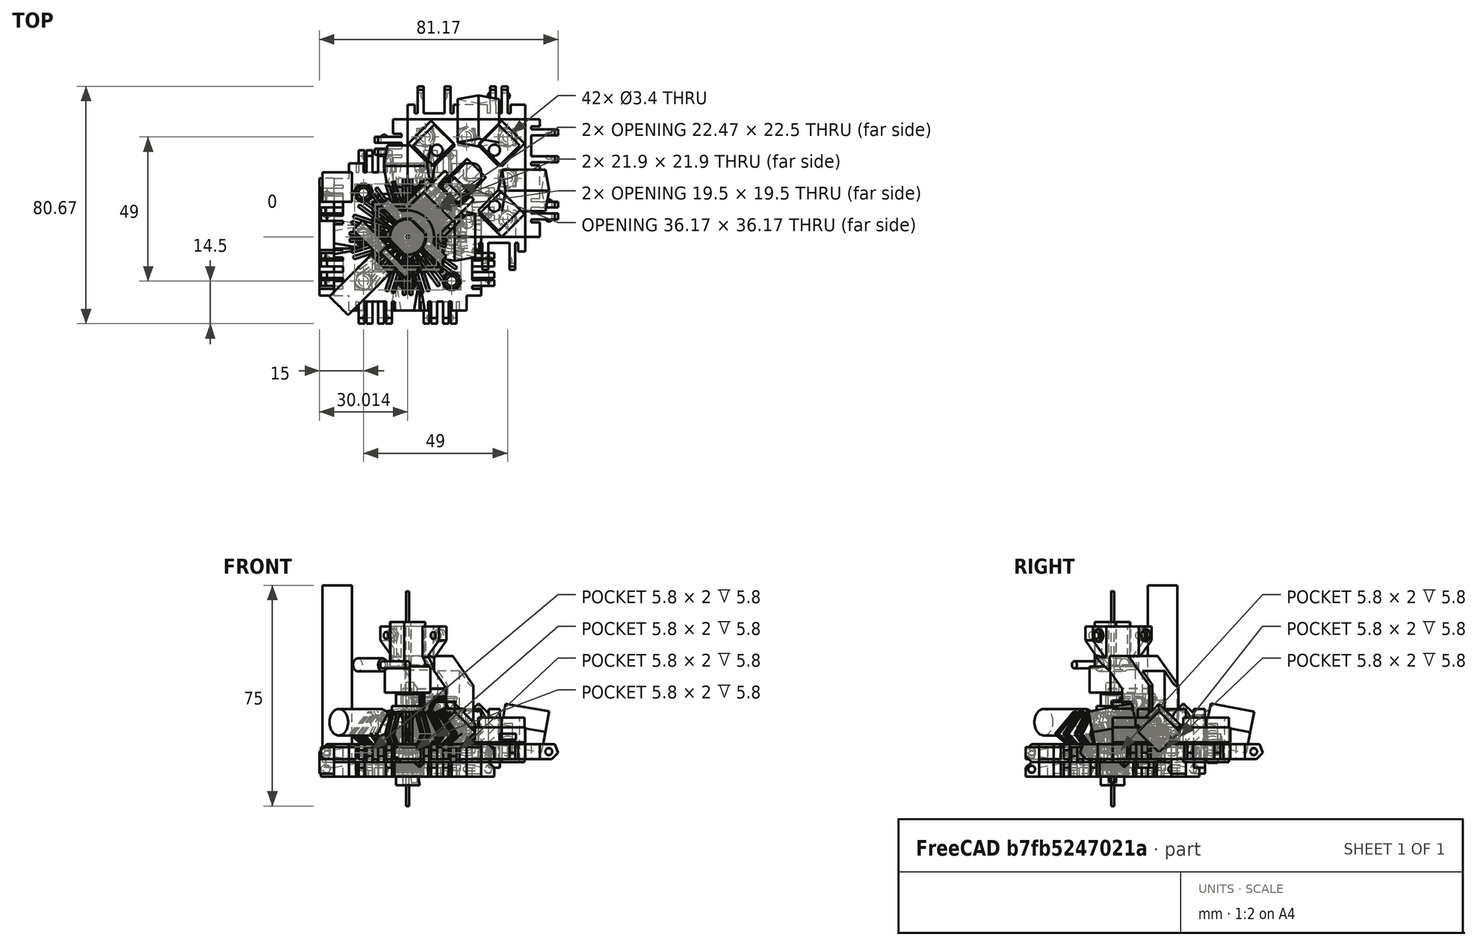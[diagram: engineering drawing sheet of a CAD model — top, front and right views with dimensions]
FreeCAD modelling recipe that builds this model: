
FCSTD DOCUMENT  (FreeCAD 0.18.4R)
Label: Robot-0.6
License: All rights reserved
LicenseURL: http://en.wikipedia.org/wiki/All_rights_reserved
objects: Part::Box×364, Part::Cut×152, Part::Sphere×107, Part::MultiFuse×104, Part::Cylinder×93, Part::Fuse×47, Part::Feature×40, Part::Chamfer×31, Drawing::FeatureViewAnnotation×17, App::DocumentObjectGroup×6, Part::Cone×6, Part::MultiCommon×6, Part::Fillet×5, Part::FeaturePython×4, Part::Mirroring×2, Drawing::FeaturePage×2
note: 961 computed .brp shape members not serialized (recipe doc carries the construction recipe); baked Part::Feature solids carry a one-line shape summary decoded from their .brp

FEATURE [Part::Box] Box  label="Cube"
  AttacherType = Attacher::AttachEngine3D
  Height = 5
  Length = 40
  Placement = pos=(-20,-20,-2) rot=(0,0,1;0rad)
  Width = 40
FEATURE [Part::Sphere] Sphere003  label="Mag Hole 3"
  Angle1 = -90
  Angle2 = 90
  Angle3 = 360
  AttacherType = Attacher::AttachEngine3D
  Placement = pos=(-15,15,1.7) rot=(0,0,1;0rad)
  Radius = 2.83
FEATURE [Part::Sphere] Sphere005  label="Mag Hole 2"
  Angle1 = -90
  Angle2 = 90
  Angle3 = 360
  AttacherType = Attacher::AttachEngine3D
  Placement = pos=(15,0,1.7) rot=(0,0,1;0rad)
  Radius = 2.825
FEATURE [Part::Sphere] Sphere  label="Mag Hole"
  Angle1 = -90
  Angle2 = 90
  Angle3 = 360
  AttacherType = Attacher::AttachEngine3D
  Placement = pos=(-15,-15,1.7) rot=(0,0,1;0rad)
  Radius = 2.83
FEATURE [Part::MultiFuse] Fusion004  label="Ball Holes"
  Shapes = -> [Sphere,Sphere005,Sphere003]
FEATURE [Part::Cut] Cut003
  Base = -> Box
  Tool = -> Fusion004
FEATURE [Part::Box] Box001  label="Cube001"
  AttacherType = Attacher::AttachEngine3D
  Height = 7
  Length = 5
  Placement = pos=(-5,0,-2) rot=(0,0,1;0rad)
  Width = 40
FEATURE [Part::Box] Box002  label="Cube002"
  AttacherType = Attacher::AttachEngine3D
  Height = 7
  Length = 10
  Placement = pos=(-15,6,-2) rot=(0,0,1;0rad)
  Width = 2
FEATURE [Part::Box] Box003  label="Cube003"
  AttacherType = Attacher::AttachEngine3D
  Height = 7
  Length = 10
  Placement = pos=(-15,10,-2) rot=(0,0,1;0rad)
  Width = 2
FEATURE [Part::Box] Box004  label="Cube004"
  AttacherType = Attacher::AttachEngine3D
  Height = 7
  Length = 10
  Placement = pos=(-15,25.4,-2) rot=(0,0,1;0rad)
  Width = 2
FEATURE [Part::Box] Box005  label="Cube005"
  AttacherType = Attacher::AttachEngine3D
  Height = 7
  Length = 10
  Placement = pos=(-15,34.6,-2) rot=(0,0,1;0rad)
  Width = 2
FEATURE [Part::Sphere] Sphere008
  Angle1 = -90
  Angle2 = 90
  Angle3 = 360
  AttacherType = Attacher::AttachEngine3D
  Placement = pos=(-7.5,6.5,0.5) rot=(0,0,1;0rad)
  Radius = 1.25
FEATURE [Part::Box] Box006  label="Chamfer Cube"
  AttacherType = Attacher::AttachEngine3D
  Height = 10
  Length = 13
  Placement = pos=(-11.69,0,-1.19) rot=(0,-1,0;0.785398rad)
  Width = 40
FEATURE [Part::Sphere] Sphere009
  Angle1 = -90
  Angle2 = 90
  Angle3 = 360
  AttacherType = Attacher::AttachEngine3D
  Placement = pos=(-7.5,11.5,0.5) rot=(0,0,1;0rad)
  Radius = 1.25
FEATURE [Part::Sphere] Sphere010
  Angle1 = -90
  Angle2 = 90
  Angle3 = 360
  AttacherType = Attacher::AttachEngine3D
  Placement = pos=(-7.5,28,0.5) rot=(0,0,1;0rad)
  Radius = 1.5
FEATURE [Part::Sphere] Sphere011
  Angle1 = -90
  Angle2 = 90
  Angle3 = 360
  AttacherType = Attacher::AttachEngine3D
  Placement = pos=(-7.5,34,0.5) rot=(0,0,1;0rad)
  Radius = 1.5
FEATURE [Part::Box] Box007  label="Cube007"
  AttacherType = Attacher::AttachEngine3D
  Height = 7
  Length = 4
  Placement = pos=(-6,5,-2) rot=(0,0,1;0rad)
  Width = 1
FEATURE [Part::Box] Box008  label="Cube008"
  AttacherType = Attacher::AttachEngine3D
  Height = 7
  Length = 4
  Placement = pos=(-6,8,-2) rot=(0,0,1;0rad)
  Width = 2
FEATURE [Part::Box] Box009  label="Cube009"
  AttacherType = Attacher::AttachEngine3D
  Height = 7
  Length = 4
  Placement = pos=(-6,12,-2) rot=(0,0,1;0rad)
  Width = 1
FEATURE [Part::Box] Box010  label="Cube010"
  AttacherType = Attacher::AttachEngine3D
  Height = 7
  Length = 4
  Placement = pos=(-6,24.4,-2) rot=(0,0,1;0rad)
  Width = 1
FEATURE [Part::Box] Box011  label="Cube011"
  AttacherType = Attacher::AttachEngine3D
  Height = 7
  Length = 4
  Placement = pos=(-6,36.6,-2) rot=(0,0,1;0rad)
  Width = 1
FEATURE [Part::Box] Box012  label="Cube012"
  AttacherType = Attacher::AttachEngine3D
  Height = 7
  Length = 4
  Placement = pos=(-6,27.4,-2) rot=(0,0,1;0rad)
  Width = 7.2
FEATURE [Part::MultiFuse] Fusion003  label="Extra Holes for Clips"
  Shapes = -> [Box012,Box009,Box011,Box008,Box010,Box007]
FEATURE [Part::Box] Box013  label="Re-level Edge Clip Block"
  AttacherType = Attacher::AttachEngine3D
  Height = 10
  Length = 20
  Placement = pos=(-19,-2,3) rot=(0,0,1;0rad)
  Width = 44
FEATURE [Part::Box] Box014  label="Cube014"
  AttacherType = Attacher::AttachEngine3D
  Height = 7
  Length = 10
  Placement = pos=(-10,34.6,0) rot=(0,0,1;0rad)
  Width = 2
FEATURE [Part::Box] Box015  label="Cube015"
  AttacherType = Attacher::AttachEngine3D
  Height = 7
  Length = 5
  Width = 40
FEATURE [Part::Box] Box016  label="Cube016"
  AttacherType = Attacher::AttachEngine3D
  Height = 7
  Length = 10
  Placement = pos=(-10,25.4,0) rot=(0,0,1;0rad)
  Width = 2
FEATURE [Part::Box] Box017  label="Cube017"
  AttacherType = Attacher::AttachEngine3D
  Height = 7
  Length = 10
  Placement = pos=(-10,10,0) rot=(0,0,1;0rad)
  Width = 2
FEATURE [Part::Box] Box018  label="Cube018"
  AttacherType = Attacher::AttachEngine3D
  Height = 7
  Length = 10
  Placement = pos=(-10,6,0) rot=(0,0,1;0rad)
  Width = 2
FEATURE [Part::Sphere] Sphere012
  Angle1 = -90
  Angle2 = 90
  Angle3 = 360
  AttacherType = Attacher::AttachEngine3D
  Placement = pos=(-3,6.5,2.5) rot=(0,0,1;0rad)
  Radius = 1.25
FEATURE [Part::Box] Box019  label="Cube019"
  AttacherType = Attacher::AttachEngine3D
  Height = 10
  Length = 13
  Placement = pos=(-10.19,0,-1.19) rot=(0,-1,0;0.785398rad)
  Width = 40
FEATURE [Part::Sphere] Sphere013
  Angle1 = -90
  Angle2 = 90
  Angle3 = 360
  AttacherType = Attacher::AttachEngine3D
  Placement = pos=(-3,11.5,2.5) rot=(0,0,1;0rad)
  Radius = 1.25
FEATURE [Part::Sphere] Sphere014
  Angle1 = -90
  Angle2 = 90
  Angle3 = 360
  AttacherType = Attacher::AttachEngine3D
  Placement = pos=(-3,28,2.5) rot=(0,0,1;0rad)
  Radius = 1.5
FEATURE [Part::Sphere] Sphere015
  Angle1 = -90
  Angle2 = 90
  Angle3 = 360
  AttacherType = Attacher::AttachEngine3D
  Placement = pos=(-3,34,2.5) rot=(0,0,1;0rad)
  Radius = 1.5
FEATURE [Part::MultiFuse] Fusion005
  Shapes = -> [Box015,Box018,Box017,Box016,Box014]
FEATURE [Part::Cut] Cut005
  Base = -> Fusion005
  Tool = -> Box019
FEATURE [Part::MultiFuse] Fusion006
  Shapes = -> [Sphere012,Sphere013,Cut005]
FEATURE [Part::MultiFuse] Fusion007
  Shapes = -> [Sphere015,Sphere014]
FEATURE [Part::Cut] Cut006
  Base = -> Fusion006
  Tool = -> Fusion007
FEATURE [Part::Chamfer] Chamfer002
  Base = -> Cut006
  Edges = 4 edges r=4: [Edge31,Edge37,Edge43,Edge46]
FEATURE [Part::Box] Box020  label="Cube020"
  AttacherType = Attacher::AttachEngine3D
  Height = 7
  Length = 4
  Placement = pos=(-1,5,0) rot=(0,0,1;0rad)
  Width = 1
FEATURE [Part::Box] Box021  label="Cube021"
  AttacherType = Attacher::AttachEngine3D
  Height = 7
  Length = 4
  Placement = pos=(-1,8,0) rot=(0,0,1;0rad)
  Width = 2
FEATURE [Part::Box] Box022  label="Cube022"
  AttacherType = Attacher::AttachEngine3D
  Height = 7
  Length = 4
  Placement = pos=(-1,12,0) rot=(0,0,1;0rad)
  Width = 1
FEATURE [Part::Box] Box023  label="Cube023"
  AttacherType = Attacher::AttachEngine3D
  Height = 7
  Length = 4
  Placement = pos=(-1,24.4,0) rot=(0,0,1;0rad)
  Width = 1
FEATURE [Part::Box] Box024  label="Cube024"
  AttacherType = Attacher::AttachEngine3D
  Height = 7
  Length = 4
  Placement = pos=(-1,36.6,0) rot=(0,0,1;0rad)
  Width = 1
FEATURE [Part::Box] Box025  label="Cube025"
  AttacherType = Attacher::AttachEngine3D
  Height = 7
  Length = 4
  Placement = pos=(-1,27.4,0) rot=(0,0,1;0rad)
  Width = 7.2
FEATURE [Part::MultiFuse] Fusion008
  Shapes = -> [Box025,Box022,Box024,Box021,Box023,Box020]
FEATURE [Part::Cut] Cut007
  Base = -> Chamfer002
  Placement = pos=(-5,40,3) rot=(1,0,0;3.14159rad)
  Tool = -> Fusion008
FEATURE [Part::Box] Box026  label="Cube026"
  AttacherType = Attacher::AttachEngine3D
  Height = 10
  Length = 12
  Placement = pos=(-11,-2,-12) rot=(0,0,1;0rad)
  Width = 44
FEATURE [Part::Cut] Cut008
  Base = -> Cut007
  Placement = pos=(40,0,0) rot=(0,0,1;1.5708rad)
  Tool = -> Box026
FEATURE [Part::Box] Box027  label="Cube027"
  AttacherType = Attacher::AttachEngine3D
  Height = 7
  Length = 4
  Placement = pos=(-1,12,0) rot=(0,0,1;0rad)
  Width = 1
FEATURE [Part::Box] Box028  label="Cube028"
  AttacherType = Attacher::AttachEngine3D
  Height = 10
  Length = 13
  Placement = pos=(-10.19,0,-1.19) rot=(0,-1,0;0.785398rad)
  Width = 40
FEATURE [Part::Box] Box029  label="Cube029"
  AttacherType = Attacher::AttachEngine3D
  Height = 7
  Length = 4
  Placement = pos=(-1,27.4,0) rot=(0,0,1;0rad)
  Width = 7.2
FEATURE [Part::Box] Box030  label="Cube030"
  AttacherType = Attacher::AttachEngine3D
  Height = 7
  Length = 4
  Placement = pos=(-1,5,0) rot=(0,0,1;0rad)
  Width = 1
FEATURE [Part::Box] Box031  label="Cube031"
  AttacherType = Attacher::AttachEngine3D
  Height = 7
  Length = 10
  Placement = pos=(-10,6,0) rot=(0,0,1;0rad)
  Width = 2
FEATURE [Part::Box] Box032  label="Cube032"
  AttacherType = Attacher::AttachEngine3D
  Height = 10
  Length = 12
  Placement = pos=(-11,-2,-12) rot=(0,0,1;0rad)
  Width = 44
FEATURE [Part::Sphere] Sphere016
  Angle1 = -90
  Angle2 = 90
  Angle3 = 360
  AttacherType = Attacher::AttachEngine3D
  Placement = pos=(-3,6.5,2.5) rot=(0,0,1;0rad)
  Radius = 1.25
FEATURE [Part::Box] Box033  label="Cube033"
  AttacherType = Attacher::AttachEngine3D
  Height = 7
  Length = 10
  Placement = pos=(-10,25.4,0) rot=(0,0,1;0rad)
  Width = 2
FEATURE [Part::Box] Box034  label="Cube034"
  AttacherType = Attacher::AttachEngine3D
  Height = 7
  Length = 10
  Placement = pos=(-10,10,0) rot=(0,0,1;0rad)
  Width = 2
FEATURE [Part::Sphere] Sphere017
  Angle1 = -90
  Angle2 = 90
  Angle3 = 360
  AttacherType = Attacher::AttachEngine3D
  Placement = pos=(-3,28,2.5) rot=(0,0,1;0rad)
  Radius = 1.5
FEATURE [Part::Sphere] Sphere018
  Angle1 = -90
  Angle2 = 90
  Angle3 = 360
  AttacherType = Attacher::AttachEngine3D
  Placement = pos=(-3,11.5,2.5) rot=(0,0,1;0rad)
  Radius = 1.25
FEATURE [Part::Box] Box035  label="Cube035"
  AttacherType = Attacher::AttachEngine3D
  Height = 7
  Length = 4
  Placement = pos=(-1,36.6,0) rot=(0,0,1;0rad)
  Width = 1
FEATURE [Part::Sphere] Sphere019
  Angle1 = -90
  Angle2 = 90
  Angle3 = 360
  AttacherType = Attacher::AttachEngine3D
  Placement = pos=(-3,34,2.5) rot=(0,0,1;0rad)
  Radius = 1.5
FEATURE [Part::MultiFuse] Fusion011
  Shapes = -> [Sphere019,Sphere017]
FEATURE [Part::Box] Box036  label="Cube036"
  AttacherType = Attacher::AttachEngine3D
  Height = 7
  Length = 4
  Placement = pos=(-1,8,0) rot=(0,0,1;0rad)
  Width = 2
FEATURE [Part::Box] Box037  label="Cube037"
  AttacherType = Attacher::AttachEngine3D
  Height = 7
  Length = 10
  Placement = pos=(-10,34.6,0) rot=(0,0,1;0rad)
  Width = 2
FEATURE [Part::Box] Box038  label="Cube038"
  AttacherType = Attacher::AttachEngine3D
  Height = 7
  Length = 4
  Placement = pos=(-1,24.4,0) rot=(0,0,1;0rad)
  Width = 1
FEATURE [Part::MultiFuse] Fusion009
  Shapes = -> [Box029,Box027,Box035,Box036,Box038,Box030]
FEATURE [Part::Box] Box039  label="Cube039"
  AttacherType = Attacher::AttachEngine3D
  Height = 7
  Length = 5
  Width = 40
FEATURE [Part::MultiFuse] Fusion012
  Shapes = -> [Box039,Box031,Box034,Box033,Box037]
FEATURE [Part::Cut] Cut011
  Base = -> Fusion012
  Tool = -> Box028
FEATURE [Part::MultiFuse] Fusion010
  Shapes = -> [Sphere016,Sphere018,Cut011]
FEATURE [Part::Cut] Cut012
  Base = -> Fusion010
  Tool = -> Fusion011
FEATURE [Part::Chamfer] Chamfer003
  Base = -> Cut012
  Edges = 4 edges r=4: [Edge31,Edge37,Edge43,Edge46]
FEATURE [Part::Cut] Cut010
  Base = -> Chamfer003
  Placement = pos=(-5,40,3) rot=(1,0,0;3.14159rad)
  Tool = -> Fusion009
FEATURE [Part::Cut] Cut009
  Base = -> Cut010
  Placement = pos=(40,40,0) rot=(0,0,1;3.14159rad)
  Tool = -> Box032
FEATURE [Part::Sphere] Sphere020
  Angle1 = -90
  Angle2 = 90
  Angle3 = 360
  AttacherType = Attacher::AttachEngine3D
  Placement = pos=(-3,11.5,2.5) rot=(0,0,1;0rad)
  Radius = 1.25
FEATURE [Part::Box] Box040  label="Cube040"
  AttacherType = Attacher::AttachEngine3D
  Height = 7
  Length = 10
  Placement = pos=(-10,6,0) rot=(0,0,1;0rad)
  Width = 2
FEATURE [Part::Box] Box041  label="Cube041"
  AttacherType = Attacher::AttachEngine3D
  Height = 7
  Length = 4
  Placement = pos=(-1,8,0) rot=(0,0,1;0rad)
  Width = 2
FEATURE [Part::Box] Box042  label="Cube042"
  AttacherType = Attacher::AttachEngine3D
  Height = 7
  Length = 10
  Placement = pos=(-10,10,0) rot=(0,0,1;0rad)
  Width = 2
FEATURE [Part::Box] Box043  label="Cube043"
  AttacherType = Attacher::AttachEngine3D
  Height = 10
  Length = 12
  Placement = pos=(-11,-2,-12) rot=(0,0,1;0rad)
  Width = 44
FEATURE [Part::Box] Box044  label="Cube044"
  AttacherType = Attacher::AttachEngine3D
  Height = 7
  Length = 4
  Placement = pos=(-1,5,0) rot=(0,0,1;0rad)
  Width = 1
FEATURE [Part::Sphere] Sphere021
  Angle1 = -90
  Angle2 = 90
  Angle3 = 360
  AttacherType = Attacher::AttachEngine3D
  Placement = pos=(-3,28,2.5) rot=(0,0,1;0rad)
  Radius = 1.5
FEATURE [Part::Sphere] Sphere022
  Angle1 = -90
  Angle2 = 90
  Angle3 = 360
  AttacherType = Attacher::AttachEngine3D
  Placement = pos=(-3,6.5,2.5) rot=(0,0,1;0rad)
  Radius = 1.25
FEATURE [Part::Sphere] Sphere023
  Angle1 = -90
  Angle2 = 90
  Angle3 = 360
  AttacherType = Attacher::AttachEngine3D
  Placement = pos=(-3,34,2.5) rot=(0,0,1;0rad)
  Radius = 1.5
FEATURE [Part::Box] Box045  label="Cube045"
  AttacherType = Attacher::AttachEngine3D
  Height = 7
  Length = 4
  Placement = pos=(-1,12,0) rot=(0,0,1;0rad)
  Width = 1
FEATURE [Part::Box] Box046  label="Cube046"
  AttacherType = Attacher::AttachEngine3D
  Height = 7
  Length = 5
  Width = 40
FEATURE [Part::Box] Box047  label="Cube047"
  AttacherType = Attacher::AttachEngine3D
  Height = 7
  Length = 4
  Placement = pos=(-1,36.6,0) rot=(0,0,1;0rad)
  Width = 1
FEATURE [Part::Box] Box048  label="Cube048"
  AttacherType = Attacher::AttachEngine3D
  Height = 7
  Length = 4
  Placement = pos=(-1,24.4,0) rot=(0,0,1;0rad)
  Width = 1
FEATURE [Part::Box] Box049  label="Cube049"
  AttacherType = Attacher::AttachEngine3D
  Height = 7
  Length = 10
  Placement = pos=(-10,25.4,0) rot=(0,0,1;0rad)
  Width = 2
FEATURE [Part::Box] Box050  label="Cube050"
  AttacherType = Attacher::AttachEngine3D
  Height = 10
  Length = 13
  Placement = pos=(-10.19,0,-1.19) rot=(0,-1,0;0.785398rad)
  Width = 40
FEATURE [Part::Box] Box051  label="Cube051"
  AttacherType = Attacher::AttachEngine3D
  Height = 7
  Length = 10
  Placement = pos=(-10,34.6,0) rot=(0,0,1;0rad)
  Width = 2
FEATURE [Part::MultiFuse] Fusion015
  Shapes = -> [Box046,Box040,Box042,Box049,Box051]
FEATURE [Part::Cut] Cut013
  Base = -> Fusion015
  Tool = -> Box050
FEATURE [Part::MultiFuse] Fusion013
  Shapes = -> [Sphere022,Sphere020,Cut013]
FEATURE [Part::MultiFuse] Fusion016
  Shapes = -> [Sphere023,Sphere021]
FEATURE [Part::Cut] Cut014
  Base = -> Fusion013
  Tool = -> Fusion016
FEATURE [Part::Chamfer] Chamfer004
  Base = -> Cut014
  Edges = 4 edges r=4: [Edge31,Edge37,Edge43,Edge46]
FEATURE [Part::Box] Box052  label="Cube052"
  AttacherType = Attacher::AttachEngine3D
  Height = 7
  Length = 4
  Placement = pos=(-1,27.4,0) rot=(0,0,1;0rad)
  Width = 7.2
FEATURE [Part::MultiFuse] Fusion014
  Shapes = -> [Box052,Box045,Box047,Box041,Box048,Box044]
FEATURE [Part::Cut] Cut016
  Base = -> Chamfer004
  Placement = pos=(-5,40,3) rot=(1,0,0;3.14159rad)
  Tool = -> Fusion014
FEATURE [Part::Cut] Cut015
  Base = -> Cut016
  Placement = pos=(0,40,0) rot=(0,0,-1;1.5708rad)
  Tool = -> Box043
FEATURE [Part::Box] Box054  label="Cube054"
  AttacherType = Attacher::AttachEngine3D
  Height = 15
  Length = 10
  Placement = pos=(9,2,-3) rot=(0,0,1;0.785398rad)
  Width = 10
FEATURE [Part::Box] Box055  label="Cube055"
  AttacherType = Attacher::AttachEngine3D
  Height = 15
  Length = 10
  Placement = pos=(31,24,-3) rot=(0,0,1;0.785398rad)
  Width = 10
FEATURE [Part::Box] Box056  label="Cube056"
  AttacherType = Attacher::AttachEngine3D
  Height = 15
  Length = 10
  Placement = pos=(31,2,-3) rot=(0,0,1;0.785398rad)
  Width = 10
FEATURE [Part::Box] Box057  label="Cube057"
  AttacherType = Attacher::AttachEngine3D
  Height = 15
  Length = 10
  Placement = pos=(9,24,-3) rot=(0,0,1;0.785398rad)
  Width = 10
FEATURE [Part::MultiFuse] Fusion017
  Shapes = -> [Box054,Box057,Box056,Box055]
FEATURE [Part::Box] Box058  label="Cube058"
  AttacherType = Attacher::AttachEngine3D
  Height = 5
  Length = 40
  Placement = pos=(0,0,3.7) rot=(0,0,1;0rad)
  Width = 40
FEATURE [Part::Box] Box059  label="Square Nut Hole 008"
  AttacherType = Attacher::AttachEngine3D
  Height = 2
  Length = 5.6
  Placement = pos=(17.2,31.2,4.6) rot=(0,0,1;0rad)
  Width = 5.6
FEATURE [Part::Box] Box060  label="Square Nut Hole 009"
  AttacherType = Attacher::AttachEngine3D
  Height = 2
  Length = 5.6
  Placement = pos=(17.2,-0.85,4.6) rot=(0,0,1;0rad)
  Width = 10
FEATURE [Part::Box] Box061  label="Square Nut Hole 010"
  AttacherType = Attacher::AttachEngine3D
  Height = 2
  Length = 5.6
  Placement = pos=(31.2,-0.85,4.6) rot=(0,0,1;0rad)
  Width = 10
FEATURE [Part::Box] Box062  label="Square Nut Hole 011"
  AttacherType = Attacher::AttachEngine3D
  Height = 2
  Length = 5.4
  Placement = pos=(31.3,17.3,4.6) rot=(0,0,1;0rad)
  Width = 5.4
FEATURE [Part::Box] Box063  label="Square Nut Hole 012"
  AttacherType = Attacher::AttachEngine3D
  Height = 2
  Length = 5.7
  Placement = pos=(3.15,31.15,4.6) rot=(0,0,1;0rad)
  Width = 5.7
FEATURE [Part::Box] Box064  label="Square Nut Hole 013"
  AttacherType = Attacher::AttachEngine3D
  Height = 2
  Length = 5.5
  Placement = pos=(31.25,31.25,4.6) rot=(0,0,1;0rad)
  Width = 5.5
FEATURE [Part::Box] Box065  label="Square Nut Hole 014"
  AttacherType = Attacher::AttachEngine3D
  Height = 2
  Length = 5.8
  Placement = pos=(3.1,17.1,4.6) rot=(0,0,1;0rad)
  Width = 5.8
FEATURE [Part::Box] Box066  label="Square Nut Hole 015"
  AttacherType = Attacher::AttachEngine3D
  Height = 2
  Length = 5.6
  Placement = pos=(3.2,-0.85,4.6) rot=(0,0,1;0rad)
  Width = 10
FEATURE [Part::Sphere] Sphere006  label="Nut Clearence1"
  Angle1 = -90
  Angle2 = 90
  Angle3 = 360
  AttacherType = Attacher::AttachEngine3D
  Placement = pos=(6,6,2.4) rot=(0,0,1;0rad)
  Radius = 3.35
FEATURE [Part::Sphere] Sphere024
  Angle1 = -90
  Angle2 = 90
  Angle3 = 360
  AttacherType = Attacher::AttachEngine3D
  Placement = pos=(6,34,2.4) rot=(0,0,1;0rad)
  Radius = 3.35
FEATURE [Part::Sphere] Sphere007
  Angle1 = -90
  Angle2 = 90
  Angle3 = 360
  AttacherType = Attacher::AttachEngine3D
  Placement = pos=(34,20,2.4) rot=(0,0,1;0rad)
  Radius = 3.35
FEATURE [Part::Sphere] Sphere001
  Angle1 = -90
  Angle2 = 90
  Angle3 = 360
  AttacherType = Attacher::AttachEngine3D
  Placement = pos=(34,6,2.4) rot=(0,0,1;0rad)
  Radius = 3.35
FEATURE [Part::Sphere] Sphere025
  Angle1 = -90
  Angle2 = 90
  Angle3 = 360
  AttacherType = Attacher::AttachEngine3D
  Placement = pos=(20,6,2.4) rot=(0,0,1;0rad)
  Radius = 3.35
FEATURE [Part::Sphere] Sphere026
  Angle1 = -90
  Angle2 = 90
  Angle3 = 360
  AttacherType = Attacher::AttachEngine3D
  Placement = pos=(20,34,2.4) rot=(0,0,1;0rad)
  Radius = 3.35
FEATURE [Part::Sphere] Sphere004
  Angle1 = -90
  Angle2 = 90
  Angle3 = 360
  AttacherType = Attacher::AttachEngine3D
  Placement = pos=(6,20,2.4) rot=(0,0,1;0rad)
  Radius = 3.35
FEATURE [Part::Sphere] Sphere002
  Angle1 = -90
  Angle2 = 90
  Angle3 = 360
  AttacherType = Attacher::AttachEngine3D
  Placement = pos=(34,34,2.4) rot=(0,0,1;0rad)
  Radius = 3.35
FEATURE [Part::Cylinder] Cylinder
  Angle = 360
  AttacherType = Attacher::AttachEngine3D
  Height = 10
  Placement = pos=(6,6,0) rot=(0,0,1;0rad)
  Radius = 1.7
FEATURE [Part::Cylinder] Cylinder002
  Angle = 360
  AttacherType = Attacher::AttachEngine3D
  Height = 10
  Placement = pos=(34,6,0) rot=(0,0,1;0rad)
  Radius = 1.7
FEATURE [Part::Cylinder] Cylinder001
  Angle = 360
  AttacherType = Attacher::AttachEngine3D
  Height = 10
  Placement = pos=(20,6,0) rot=(0,0,1;0rad)
  Radius = 1.7
FEATURE [Part::Cylinder] Cylinder003
  Angle = 360
  AttacherType = Attacher::AttachEngine3D
  Height = 10
  Placement = pos=(34,34,0) rot=(0,0,1;0rad)
  Radius = 1.7
FEATURE [Part::Cylinder] Cylinder004
  Angle = 360
  AttacherType = Attacher::AttachEngine3D
  Height = 10
  Placement = pos=(20,34,0) rot=(0,0,1;0rad)
  Radius = 1.7
FEATURE [Part::Cylinder] Cylinder005
  Angle = 360
  AttacherType = Attacher::AttachEngine3D
  Height = 10
  Placement = pos=(6,34,0) rot=(0,0,1;0rad)
  Radius = 1.7
FEATURE [Part::Cylinder] Cylinder006
  Angle = 360
  AttacherType = Attacher::AttachEngine3D
  Height = 10
  Placement = pos=(6,20,0) rot=(0,0,1;0rad)
  Radius = 1.7
FEATURE [Part::Cylinder] Cylinder007
  Angle = 360
  AttacherType = Attacher::AttachEngine3D
  Height = 10
  Placement = pos=(34,20,0) rot=(0,0,1;0rad)
  Radius = 1.7
FEATURE [Part::MultiFuse] Fusion018
  Shapes = -> [Cylinder,Cylinder004,Cylinder007,Cylinder005,Cylinder006,Cylinder001,Cylinder002,Cylinder003]
FEATURE [Part::MultiFuse] Fusion019
  Shapes = -> [Sphere007,Sphere024,Sphere006,Sphere025,Sphere001,Sphere026,Sphere004,Sphere002]
FEATURE [Part::MultiFuse] Fusion020
  Shapes = -> [Box061,Box065,Box062,Box063,Box064,Box066,Box059,Box060]
FEATURE [Part::Cut] Cut017
  Base = -> Box058
  Tool = -> Fusion020
FEATURE [Part::Cut] Cut019
  Base = -> Cut017
  Tool = -> Fusion019
FEATURE [Part::Cut] Cut018
  Base = -> Cut019
  Tool = -> Fusion018
FEATURE [Part::Cylinder] Cylinder008
  Angle = 360
  AttacherType = Attacher::AttachEngine3D
  Height = 20
  Placement = pos=(10,10.5,-5) rot=(0,0,1;0rad)
  Radius = 1.9
FEATURE [Part::Cylinder] Cylinder009
  Angle = 360
  AttacherType = Attacher::AttachEngine3D
  Height = 20
  Placement = pos=(29.5,10.5,-5) rot=(0,0,1;0rad)
  Radius = 1.9
FEATURE [Part::Cylinder] Cylinder010
  Angle = 360
  AttacherType = Attacher::AttachEngine3D
  Height = 20
  Placement = pos=(29.5,29.5,-5) rot=(0,0,1;0rad)
  Radius = 1.9
FEATURE [Part::Cylinder] Cylinder011
  Angle = 360
  AttacherType = Attacher::AttachEngine3D
  Height = 20
  Placement = pos=(10,29.5,-7) rot=(0,0,1;0rad)
  Radius = 1.9
FEATURE [Part::MultiFuse] Fusion021  label="M2 Screw holes"
  Shapes = -> [Cylinder008,Cylinder009,Cylinder011,Cylinder010]
FEATURE [Part::Box] Box067  label="Square Nut Hole 016"
  AttacherType = Attacher::AttachEngine3D
  Height = 2
  Length = 5.8
  Placement = pos=(31.1,17.1,4.6) rot=(0,0,1;0rad)
  Width = 5.8
FEATURE [Part::Box] Box068  label="Square Nut Hole 017"
  AttacherType = Attacher::AttachEngine3D
  Height = 2
  Length = 5.8
  Placement = pos=(17.1,36.9,2.1) rot=(1,0,0;3.14159rad)
  Width = 5.8
FEATURE [Part::Box] Box069  label="Square Nut Hole 018"
  AttacherType = Attacher::AttachEngine3D
  Height = 2
  Length = 5.8
  Placement = pos=(-2.9,2.9,2.1) rot=(1,0,0;3.14159rad)
  Width = 5.8
FEATURE [Part::Box] Box070  label="Square Nut Hole 019"
  AttacherType = Attacher::AttachEngine3D
  Height = 2
  Length = 5.8
  Placement = pos=(3.1,3.1,4.6) rot=(0,0,1;0rad)
  Width = 5.8
FEATURE [Part::Box] Box071  label="Square Nut Hole 020"
  AttacherType = Attacher::AttachEngine3D
  Height = 2
  Length = 5.8
  Placement = pos=(3.1,31.1,4.6) rot=(0,0,1;0rad)
  Width = 5.8
FEATURE [Part::Box] Box072  label="Square Nut Hole 021"
  AttacherType = Attacher::AttachEngine3D
  Height = 2
  Length = 5.8
  Placement = pos=(17.1,31.1,4.6) rot=(0,0,1;0rad)
  Width = 5.8
FEATURE [Part::Box] Box073  label="Square Nut Hole 022"
  AttacherType = Attacher::AttachEngine3D
  Height = 2
  Length = 5.8
  Placement = pos=(31.1,31.1,4.6) rot=(0,0,1;0rad)
  Width = 5.8
FEATURE [Part::Box] Box074  label="Square Nut Hole 023"
  AttacherType = Attacher::AttachEngine3D
  Height = 2
  Length = 5.8
  Placement = pos=(3.1,17.1,4.6) rot=(0,0,1;0rad)
  Width = 5.8
FEATURE [Part::Cylinder] Cylinder012
  Angle = 360
  AttacherType = Attacher::AttachEngine3D
  Height = 10
  Placement = pos=(6,6,0) rot=(0,0,1;0rad)
  Radius = 1.7
FEATURE [Part::Cylinder] Cylinder013
  Angle = 360
  AttacherType = Attacher::AttachEngine3D
  Height = 10
  Placement = pos=(34,34,0) rot=(0,0,1;0rad)
  Radius = 1.7
FEATURE [Part::Cylinder] Cylinder014
  Angle = 360
  AttacherType = Attacher::AttachEngine3D
  Height = 10
  Placement = pos=(20,34,0) rot=(0,0,1;0rad)
  Radius = 1.7
FEATURE [Part::Cylinder] Cylinder015
  Angle = 360
  AttacherType = Attacher::AttachEngine3D
  Height = 10
  Placement = pos=(6,34,0) rot=(0,0,1;0rad)
  Radius = 1.7
FEATURE [Part::Cylinder] Cylinder016
  Angle = 360
  AttacherType = Attacher::AttachEngine3D
  Height = 10
  Placement = pos=(6,20,0) rot=(0,0,1;0rad)
  Radius = 1.7
FEATURE [Part::Cylinder] Cylinder017
  Angle = 360
  AttacherType = Attacher::AttachEngine3D
  Height = 10
  Placement = pos=(34,20,0) rot=(0,0,1;0rad)
  Radius = 1.7
FEATURE [Part::Cylinder] Cylinder018
  Angle = 360
  AttacherType = Attacher::AttachEngine3D
  Height = 10
  Placement = pos=(0,0,6.7) rot=(1,0,0;3.14159rad)
  Radius = 1.7
FEATURE [Part::Cylinder] Cylinder019
  Angle = 360
  AttacherType = Attacher::AttachEngine3D
  Height = 10
  Placement = pos=(20,34,6.7) rot=(1,0,0;3.14159rad)
  Radius = 1.7
FEATURE [Part::Box] Box075  label="Cube059"
  AttacherType = Attacher::AttachEngine3D
  Height = 5
  Length = 40
  Placement = pos=(-20,-20,-2) rot=(0,0,1;0rad)
  Width = 40
FEATURE [Part::Sphere] Sphere027
  Angle1 = -90
  Angle2 = 90
  Angle3 = 360
  AttacherType = Attacher::AttachEngine3D
  Placement = pos=(34,20,2.4) rot=(0,0,1;0rad)
  Radius = 3.35
FEATURE [Part::Sphere] Sphere028  label="Nut Clearence002"
  Angle1 = -90
  Angle2 = 90
  Angle3 = 360
  AttacherType = Attacher::AttachEngine3D
  Placement = pos=(6,6,2.4) rot=(0,0,1;0rad)
  Radius = 3.35
FEATURE [Part::Sphere] Sphere029
  Angle1 = -90
  Angle2 = 90
  Angle3 = 360
  AttacherType = Attacher::AttachEngine3D
  Placement = pos=(34,34,2.4) rot=(0,0,1;0rad)
  Radius = 3.35
FEATURE [Part::Sphere] Sphere030
  Angle1 = -90
  Angle2 = 90
  Angle3 = 360
  AttacherType = Attacher::AttachEngine3D
  Placement = pos=(0,0,4.3) rot=(1,0,0;3.14159rad)
  Radius = 3.35
FEATURE [Part::Sphere] Sphere031
  Angle1 = -90
  Angle2 = 90
  Angle3 = 360
  AttacherType = Attacher::AttachEngine3D
  Placement = pos=(20,34,4.3) rot=(1,0,0;3.14159rad)
  Radius = 3.35
FEATURE [Part::Sphere] Sphere032
  Angle1 = -90
  Angle2 = 90
  Angle3 = 360
  AttacherType = Attacher::AttachEngine3D
  Placement = pos=(6,34,2.4) rot=(0,0,1;0rad)
  Radius = 3.35
FEATURE [Part::Sphere] Sphere033
  Angle1 = -90
  Angle2 = 90
  Angle3 = 360
  AttacherType = Attacher::AttachEngine3D
  Placement = pos=(6,20,2.4) rot=(0,0,1;0rad)
  Radius = 3.35
FEATURE [Part::Sphere] Sphere034
  Angle1 = -90
  Angle2 = 90
  Angle3 = 360
  AttacherType = Attacher::AttachEngine3D
  Placement = pos=(20,34,2.4) rot=(0,0,1;0rad)
  Radius = 3.35
FEATURE [Part::Box] Box076  label="Cube060"
  AttacherType = Attacher::AttachEngine3D
  Height = 15
  Length = 19.5
  Placement = pos=(-9.75,-9.75,-3) rot=(0,0,1;0rad)
  Width = 19.5
FEATURE [Part::Box] Box077  label="Cube061"
  AttacherType = Attacher::AttachEngine3D
  Height = 15
  Length = 11
  Placement = pos=(8,24,-3) rot=(0,0,1;0.785398rad)
  Width = 11
FEATURE [Part::Box] Box078  label="Cube062"
  AttacherType = Attacher::AttachEngine3D
  Height = 15
  Length = 11
  Placement = pos=(8,0,-3) rot=(0,0,1;0.785398rad)
  Width = 11
FEATURE [Part::Box] Box079  label="Cube063"
  AttacherType = Attacher::AttachEngine3D
  Height = 15
  Length = 11
  Placement = pos=(32,0,-3) rot=(0,0,1;0.785398rad)
  Width = 11
FEATURE [Part::Box] Box080  label="Cube064"
  AttacherType = Attacher::AttachEngine3D
  Height = 15
  Length = 11
  Placement = pos=(32,24,-3) rot=(0,0,1;0.785398rad)
  Width = 11
FEATURE [Part::MultiFuse] Fusion022
  Shapes = -> [Box078,Box077,Box079,Box080]
FEATURE [Part::Cylinder] Cylinder020
  Angle = 360
  AttacherType = Attacher::AttachEngine3D
  Height = 20
  Placement = pos=(29.5,10.5,-5) rot=(0,0,1;0rad)
  Radius = 1.9
FEATURE [Part::Cylinder] Cylinder021
  Angle = 360
  AttacherType = Attacher::AttachEngine3D
  Height = 20
  Placement = pos=(10,29.5,-7) rot=(0,0,1;0rad)
  Radius = 1.9
FEATURE [Part::Cylinder] Cylinder022
  Angle = 360
  AttacherType = Attacher::AttachEngine3D
  Height = 20
  Placement = pos=(10,10.5,-5) rot=(0,0,1;0rad)
  Radius = 1.9
FEATURE [Part::Cylinder] Cylinder023
  Angle = 360
  AttacherType = Attacher::AttachEngine3D
  Height = 20
  Placement = pos=(29.5,29.5,-5) rot=(0,0,1;0rad)
  Radius = 1.9
FEATURE [Part::MultiFuse] Fusion023  label="M2 Screw holes001"
  Shapes = -> [Cylinder022,Cylinder020,Cylinder021,Cylinder023]
FEATURE [App::DocumentObjectGroup] Group  label="Cubes"
  Group = -> [Fusion017,Fusion022]
FEATURE [Part::Box] Box083  label="Cube067"
  AttacherType = Attacher::AttachEngine3D
  Height = 10
  Length = 24
  Placement = pos=(-12,-12,2.1) rot=(0,0,1;0rad)
  Width = 24
FEATURE [Part::Box] Box084  label="Cube068"
  AttacherType = Attacher::AttachEngine3D
  Height = 14
  Length = 20
  Placement = pos=(-10,-10,0) rot=(0,0,1;0rad)
  Width = 20
FEATURE [Part::Cut] Cut020
  Base = -> Box083
  Tool = -> Box084
FEATURE [Part::Chamfer] Chamfer007  label="Glue Channel Ball"
  Base = -> Cut020
  Edges = 8 edges r=0.95: [Edge4,Edge5,Edge14,Edge16,Edge17,Edge18,Edge19,Edge20]
FEATURE [Part::Chamfer] Chamfer008  label="Octogon Ball"
  Base = -> Box076
  Edges = 4 edges r=4: [Edge1,Edge3,Edge5,Edge7]
FEATURE [Part::Box] Box085  label="Cube069"
  AttacherType = Attacher::AttachEngine3D
  Height = 15
  Length = 19.5
  Placement = pos=(-9.75,-9.75,-14) rot=(0,0,1;0rad)
  Width = 19.5
FEATURE [Part::Box] Box086  label="Cube070"
  AttacherType = Attacher::AttachEngine3D
  Height = 10
  Length = 10
  Placement = pos=(4,-26,1) rot=(0.205904,-0.974848,-0.085288;0.803573rad)
  Width = 15
FEATURE [Part::Box] Box089  label="Cube073"
  AttacherType = Attacher::AttachEngine3D
  Height = 10
  Length = 10
  Placement = pos=(17,32.0919,9.95) rot=(-0.225436,0.969773,-0.093378;0.807337rad)
  Width = 15
FEATURE [Part::Box] Box090  label="Cube074"
  AttacherType = Attacher::AttachEngine3D
  Height = 10
  Length = 15
  Placement = pos=(30.8481,15.8,2.86019) rot=(0.974848,0.205904,-0.085288;0.803573rad)
  Width = 10
FEATURE [Part::Box] Box091  label="Cube075"
  AttacherType = Attacher::AttachEngine3D
  Height = 10
  Length = 10
  Placement = pos=(7.9081,17,9.95) rot=(-0.450607,0.280623,0.847469;1.65638rad)
  Width = 15
FEATURE [Part::Box] Box092  label="Cube076"
  AttacherType = Attacher::AttachEngine3D
  Height = 10
  Length = 10
  Placement = pos=(23,7.9081,9.95) rot=(-0.381178,-0.08861,0.920245;3.06822rad)
  Width = 15
FEATURE [Part::Box] Box093  label="Cube077"
  AttacherType = Attacher::AttachEngine3D
  Height = 7
  Length = 5
  Width = 40
FEATURE [Part::Box] Box094  label="Cube078"
  AttacherType = Attacher::AttachEngine3D
  Height = 7
  Length = 10
  Placement = pos=(-10,6,0) rot=(0,0,1;0rad)
  Width = 2
FEATURE [Part::Box] Box095  label="Cube079"
  AttacherType = Attacher::AttachEngine3D
  Height = 7
  Length = 10
  Placement = pos=(-10,10,0) rot=(0,0,1;0rad)
  Width = 2
FEATURE [Part::Box] Box096  label="Cube080"
  AttacherType = Attacher::AttachEngine3D
  Height = 7
  Length = 10
  Placement = pos=(-10,25.4,0) rot=(0,0,1;0rad)
  Width = 2
FEATURE [Part::Box] Box097  label="Cube081"
  AttacherType = Attacher::AttachEngine3D
  Height = 7
  Length = 10
  Placement = pos=(-10,34.6,0) rot=(0,0,1;0rad)
  Width = 2
FEATURE [Part::Sphere] Sphere035
  Angle1 = -90
  Angle2 = 90
  Angle3 = 360
  AttacherType = Attacher::AttachEngine3D
  Placement = pos=(-3,6.5,2.5) rot=(0,0,1;0rad)
  Radius = 1.25
FEATURE [Part::Box] Box098  label="Cube082"
  AttacherType = Attacher::AttachEngine3D
  Height = 10
  Length = 13
  Placement = pos=(-10.19,0,-1.19) rot=(0,-1,0;0.785398rad)
  Width = 40
FEATURE [Part::Sphere] Sphere036
  Angle1 = -90
  Angle2 = 90
  Angle3 = 360
  AttacherType = Attacher::AttachEngine3D
  Placement = pos=(-3,11.5,2.5) rot=(0,0,1;0rad)
  Radius = 1.25
FEATURE [Part::Sphere] Sphere037
  Angle1 = -90
  Angle2 = 90
  Angle3 = 360
  AttacherType = Attacher::AttachEngine3D
  Placement = pos=(-3,28,2.5) rot=(0,0,1;0rad)
  Radius = 1.5
FEATURE [Part::Sphere] Sphere038
  Angle1 = -90
  Angle2 = 90
  Angle3 = 360
  AttacherType = Attacher::AttachEngine3D
  Placement = pos=(-3,34,2.5) rot=(0,0,1;0rad)
  Radius = 1.5
FEATURE [Part::MultiFuse] Fusion030
  Shapes = -> [Box093,Box094,Box095,Box096,Box097]
FEATURE [Part::Cut] Cut025
  Base = -> Fusion030
  Tool = -> Box098
FEATURE [Part::MultiFuse] Fusion031
  Shapes = -> [Sphere035,Sphere036,Cut025]
FEATURE [Part::MultiFuse] Fusion032
  Shapes = -> [Sphere038,Sphere037]
FEATURE [Part::Cut] Cut026
  Base = -> Fusion031
  Tool = -> Fusion032
FEATURE [Part::Chamfer] Chamfer009
  Base = -> Cut026
  Edges = 4 edges r=4: [Edge31,Edge37,Edge43,Edge46]
FEATURE [Part::Box] Box099  label="Cube083"
  AttacherType = Attacher::AttachEngine3D
  Height = 7
  Length = 4
  Placement = pos=(-1,5,0) rot=(0,0,1;0rad)
  Width = 1
FEATURE [Part::Box] Box100  label="Cube084"
  AttacherType = Attacher::AttachEngine3D
  Height = 7
  Length = 4
  Placement = pos=(-1,8,0) rot=(0,0,1;0rad)
  Width = 2
FEATURE [Part::Box] Box101  label="Cube085"
  AttacherType = Attacher::AttachEngine3D
  Height = 7
  Length = 4
  Placement = pos=(-1,12,0) rot=(0,0,1;0rad)
  Width = 1
FEATURE [Part::Box] Box102  label="Cube086"
  AttacherType = Attacher::AttachEngine3D
  Height = 7
  Length = 4
  Placement = pos=(-1,24.4,0) rot=(0,0,1;0rad)
  Width = 1
FEATURE [Part::Box] Box103  label="Cube087"
  AttacherType = Attacher::AttachEngine3D
  Height = 7
  Length = 4
  Placement = pos=(-1,36.6,0) rot=(0,0,1;0rad)
  Width = 1
FEATURE [Part::Box] Box104  label="Cube088"
  AttacherType = Attacher::AttachEngine3D
  Height = 7
  Length = 4
  Placement = pos=(-1,27.4,0) rot=(0,0,1;0rad)
  Width = 7.2
FEATURE [Part::MultiFuse] Fusion033
  Shapes = -> [Box104,Box101,Box103,Box100,Box102,Box099]
FEATURE [Part::Cut] Cut027
  Base = -> Chamfer009
  Placement = pos=(-5,40,3) rot=(1,0,0;3.14159rad)
  Tool = -> Fusion033
FEATURE [Part::Box] Box105  label="Cube089"
  AttacherType = Attacher::AttachEngine3D
  Height = 10
  Length = 12
  Placement = pos=(-11,-2,-12) rot=(0,0,1;0rad)
  Width = 44
FEATURE [Part::Cut] Cut028
  Base = -> Cut027
  Tool = -> Box105
FEATURE [Part::Box] Box106  label="Cube090"
  AttacherType = Attacher::AttachEngine3D
  Height = 7
  Length = 10
  Placement = pos=(-10,34.6,0) rot=(0,0,1;0rad)
  Width = 2
FEATURE [Part::Box] Box107  label="Cube091"
  AttacherType = Attacher::AttachEngine3D
  Height = 7
  Length = 5
  Width = 40
FEATURE [Part::Box] Box108  label="Cube092"
  AttacherType = Attacher::AttachEngine3D
  Height = 7
  Length = 10
  Placement = pos=(-10,25.4,0) rot=(0,0,1;0rad)
  Width = 2
FEATURE [Part::Box] Box109  label="Cube093"
  AttacherType = Attacher::AttachEngine3D
  Height = 7
  Length = 10
  Placement = pos=(-10,10,0) rot=(0,0,1;0rad)
  Width = 2
FEATURE [Part::Box] Box110  label="Cube094"
  AttacherType = Attacher::AttachEngine3D
  Height = 7
  Length = 10
  Placement = pos=(-10,6,0) rot=(0,0,1;0rad)
  Width = 2
FEATURE [Part::Sphere] Sphere039
  Angle1 = -90
  Angle2 = 90
  Angle3 = 360
  AttacherType = Attacher::AttachEngine3D
  Placement = pos=(-3,6.5,2.5) rot=(0,0,1;0rad)
  Radius = 1.25
FEATURE [Part::Box] Box111  label="Cube095"
  AttacherType = Attacher::AttachEngine3D
  Height = 10
  Length = 13
  Placement = pos=(-10.19,0,-1.19) rot=(0,-1,0;0.785398rad)
  Width = 40
FEATURE [Part::Sphere] Sphere040
  Angle1 = -90
  Angle2 = 90
  Angle3 = 360
  AttacherType = Attacher::AttachEngine3D
  Placement = pos=(-3,11.5,2.5) rot=(0,0,1;0rad)
  Radius = 1.25
FEATURE [Part::Sphere] Sphere041
  Angle1 = -90
  Angle2 = 90
  Angle3 = 360
  AttacherType = Attacher::AttachEngine3D
  Placement = pos=(-3,28,2.5) rot=(0,0,1;0rad)
  Radius = 1.5
FEATURE [Part::Sphere] Sphere042
  Angle1 = -90
  Angle2 = 90
  Angle3 = 360
  AttacherType = Attacher::AttachEngine3D
  Placement = pos=(-3,34,2.5) rot=(0,0,1;0rad)
  Radius = 1.5
FEATURE [Part::MultiFuse] Fusion034
  Shapes = -> [Box107,Box110,Box109,Box108,Box106]
FEATURE [Part::Cut] Cut029
  Base = -> Fusion034
  Tool = -> Box111
FEATURE [Part::MultiFuse] Fusion035
  Shapes = -> [Sphere039,Sphere040,Cut029]
FEATURE [Part::MultiFuse] Fusion036
  Shapes = -> [Sphere042,Sphere041]
FEATURE [Part::Cut] Cut030
  Base = -> Fusion035
  Tool = -> Fusion036
FEATURE [Part::Chamfer] Chamfer010
  Base = -> Cut030
  Edges = 4 edges r=4: [Edge31,Edge37,Edge43,Edge46]
FEATURE [Part::Box] Box112  label="Cube096"
  AttacherType = Attacher::AttachEngine3D
  Height = 7
  Length = 4
  Placement = pos=(-1,5,0) rot=(0,0,1;0rad)
  Width = 1
FEATURE [Part::Box] Box113  label="Cube097"
  AttacherType = Attacher::AttachEngine3D
  Height = 7
  Length = 4
  Placement = pos=(-1,8,0) rot=(0,0,1;0rad)
  Width = 2
FEATURE [Part::Box] Box114  label="Cube098"
  AttacherType = Attacher::AttachEngine3D
  Height = 7
  Length = 4
  Placement = pos=(-1,12,0) rot=(0,0,1;0rad)
  Width = 1
FEATURE [Part::Box] Box115  label="Cube099"
  AttacherType = Attacher::AttachEngine3D
  Height = 7
  Length = 4
  Placement = pos=(-1,24.4,0) rot=(0,0,1;0rad)
  Width = 1
FEATURE [Part::Box] Box116  label="Cube100"
  AttacherType = Attacher::AttachEngine3D
  Height = 7
  Length = 4
  Placement = pos=(-1,36.6,0) rot=(0,0,1;0rad)
  Width = 1
FEATURE [Part::Box] Box117  label="Cube101"
  AttacherType = Attacher::AttachEngine3D
  Height = 7
  Length = 4
  Placement = pos=(-1,27.4,0) rot=(0,0,1;0rad)
  Width = 7.2
FEATURE [Part::MultiFuse] Fusion037
  Shapes = -> [Box117,Box114,Box116,Box113,Box115,Box112]
FEATURE [Part::Cut] Cut031
  Base = -> Chamfer010
  Placement = pos=(-5,40,3) rot=(1,0,0;3.14159rad)
  Tool = -> Fusion037
FEATURE [Part::Box] Box118  label="Cube102"
  AttacherType = Attacher::AttachEngine3D
  Height = 10
  Length = 12
  Placement = pos=(-11,-2,-12) rot=(0,0,1;0rad)
  Width = 44
FEATURE [Part::Cut] Cut032
  Base = -> Cut031
  Placement = pos=(40,0,0) rot=(0,0,1;1.5708rad)
  Tool = -> Box118
FEATURE [Part::Box] Box119  label="Cube103"
  AttacherType = Attacher::AttachEngine3D
  Height = 7
  Length = 4
  Placement = pos=(-1,12,0) rot=(0,0,1;0rad)
  Width = 1
FEATURE [Part::Box] Box120  label="Cube104"
  AttacherType = Attacher::AttachEngine3D
  Height = 10
  Length = 13
  Placement = pos=(-10.19,0,-1.19) rot=(0,-1,0;0.785398rad)
  Width = 40
FEATURE [Part::Box] Box121  label="Cube105"
  AttacherType = Attacher::AttachEngine3D
  Height = 7
  Length = 4
  Placement = pos=(-1,27.4,0) rot=(0,0,1;0rad)
  Width = 7.2
FEATURE [Part::Box] Box122  label="Cube106"
  AttacherType = Attacher::AttachEngine3D
  Height = 7
  Length = 4
  Placement = pos=(-1,5,0) rot=(0,0,1;0rad)
  Width = 1
FEATURE [Part::Box] Box123  label="Cube107"
  AttacherType = Attacher::AttachEngine3D
  Height = 7
  Length = 10
  Placement = pos=(-10,6,0) rot=(0,0,1;0rad)
  Width = 2
FEATURE [Part::Box] Box124  label="Cube108"
  AttacherType = Attacher::AttachEngine3D
  Height = 10
  Length = 12
  Placement = pos=(-11,-2,-12) rot=(0,0,1;0rad)
  Width = 44
FEATURE [Part::Sphere] Sphere043
  Angle1 = -90
  Angle2 = 90
  Angle3 = 360
  AttacherType = Attacher::AttachEngine3D
  Placement = pos=(-3,6.5,2.5) rot=(0,0,1;0rad)
  Radius = 1.25
FEATURE [Part::Box] Box125  label="Cube109"
  AttacherType = Attacher::AttachEngine3D
  Height = 7
  Length = 10
  Placement = pos=(-10,25.4,0) rot=(0,0,1;0rad)
  Width = 2
FEATURE [Part::Box] Box126  label="Cube110"
  AttacherType = Attacher::AttachEngine3D
  Height = 7
  Length = 10
  Placement = pos=(-10,10,0) rot=(0,0,1;0rad)
  Width = 2
FEATURE [Part::Sphere] Sphere044
  Angle1 = -90
  Angle2 = 90
  Angle3 = 360
  AttacherType = Attacher::AttachEngine3D
  Placement = pos=(-3,28,2.5) rot=(0,0,1;0rad)
  Radius = 1.5
FEATURE [Part::Sphere] Sphere045
  Angle1 = -90
  Angle2 = 90
  Angle3 = 360
  AttacherType = Attacher::AttachEngine3D
  Placement = pos=(-3,11.5,2.5) rot=(0,0,1;0rad)
  Radius = 1.25
FEATURE [Part::Box] Box127  label="Cube111"
  AttacherType = Attacher::AttachEngine3D
  Height = 7
  Length = 4
  Placement = pos=(-1,36.6,0) rot=(0,0,1;0rad)
  Width = 1
FEATURE [Part::Sphere] Sphere046
  Angle1 = -90
  Angle2 = 90
  Angle3 = 360
  AttacherType = Attacher::AttachEngine3D
  Placement = pos=(-3,34,2.5) rot=(0,0,1;0rad)
  Radius = 1.5
FEATURE [Part::MultiFuse] Fusion040
  Shapes = -> [Sphere046,Sphere044]
FEATURE [Part::Box] Box128  label="Cube112"
  AttacherType = Attacher::AttachEngine3D
  Height = 7
  Length = 4
  Placement = pos=(-1,8,0) rot=(0,0,1;0rad)
  Width = 2
FEATURE [Part::Box] Box129  label="Cube113"
  AttacherType = Attacher::AttachEngine3D
  Height = 7
  Length = 10
  Placement = pos=(-10,34.6,0) rot=(0,0,1;0rad)
  Width = 2
FEATURE [Part::Box] Box130  label="Cube114"
  AttacherType = Attacher::AttachEngine3D
  Height = 7
  Length = 4
  Placement = pos=(-1,24.4,0) rot=(0,0,1;0rad)
  Width = 1
FEATURE [Part::MultiFuse] Fusion038
  Shapes = -> [Box121,Box119,Box127,Box128,Box130,Box122]
FEATURE [Part::Box] Box131  label="Cube115"
  AttacherType = Attacher::AttachEngine3D
  Height = 7
  Length = 5
  Width = 40
FEATURE [Part::MultiFuse] Fusion041
  Shapes = -> [Box131,Box123,Box126,Box125,Box129]
FEATURE [Part::Cut] Cut035
  Base = -> Fusion041
  Tool = -> Box120
FEATURE [Part::MultiFuse] Fusion039
  Shapes = -> [Sphere043,Sphere045,Cut035]
FEATURE [Part::Cut] Cut036
  Base = -> Fusion039
  Tool = -> Fusion040
FEATURE [Part::Chamfer] Chamfer011
  Base = -> Cut036
  Edges = 4 edges r=4: [Edge31,Edge37,Edge43,Edge46]
FEATURE [Part::Cut] Cut034
  Base = -> Chamfer011
  Placement = pos=(-5,40,3) rot=(1,0,0;3.14159rad)
  Tool = -> Fusion038
FEATURE [Part::Cut] Cut033
  Base = -> Cut034
  Placement = pos=(40,40,0) rot=(0,0,1;3.14159rad)
  Tool = -> Box124
FEATURE [Part::Sphere] Sphere047
  Angle1 = -90
  Angle2 = 90
  Angle3 = 360
  AttacherType = Attacher::AttachEngine3D
  Placement = pos=(-3,11.5,2.5) rot=(0,0,1;0rad)
  Radius = 1.25
FEATURE [Part::Box] Box132  label="Cube116"
  AttacherType = Attacher::AttachEngine3D
  Height = 7
  Length = 10
  Placement = pos=(-10,6,0) rot=(0,0,1;0rad)
  Width = 2
FEATURE [Part::Box] Box133  label="Cube117"
  AttacherType = Attacher::AttachEngine3D
  Height = 7
  Length = 4
  Placement = pos=(-1,8,0) rot=(0,0,1;0rad)
  Width = 2
FEATURE [Part::Box] Box134  label="Cube118"
  AttacherType = Attacher::AttachEngine3D
  Height = 7
  Length = 10
  Placement = pos=(-10,10,0) rot=(0,0,1;0rad)
  Width = 2
FEATURE [Part::Box] Box135  label="Cube119"
  AttacherType = Attacher::AttachEngine3D
  Height = 10
  Length = 12
  Placement = pos=(-11,-2,-12) rot=(0,0,1;0rad)
  Width = 44
FEATURE [Part::Box] Box136  label="Cube120"
  AttacherType = Attacher::AttachEngine3D
  Height = 7
  Length = 4
  Placement = pos=(-1,5,0) rot=(0,0,1;0rad)
  Width = 1
FEATURE [Part::Sphere] Sphere048
  Angle1 = -90
  Angle2 = 90
  Angle3 = 360
  AttacherType = Attacher::AttachEngine3D
  Placement = pos=(-3,28,2.5) rot=(0,0,1;0rad)
  Radius = 1.5
FEATURE [Part::Sphere] Sphere049
  Angle1 = -90
  Angle2 = 90
  Angle3 = 360
  AttacherType = Attacher::AttachEngine3D
  Placement = pos=(-3,6.5,2.5) rot=(0,0,1;0rad)
  Radius = 1.25
FEATURE [Part::Sphere] Sphere050
  Angle1 = -90
  Angle2 = 90
  Angle3 = 360
  AttacherType = Attacher::AttachEngine3D
  Placement = pos=(-3,34,2.5) rot=(0,0,1;0rad)
  Radius = 1.5
FEATURE [Part::Box] Box137  label="Cube121"
  AttacherType = Attacher::AttachEngine3D
  Height = 7
  Length = 4
  Placement = pos=(-1,12,0) rot=(0,0,1;0rad)
  Width = 1
FEATURE [Part::Box] Box138  label="Cube122"
  AttacherType = Attacher::AttachEngine3D
  Height = 7
  Length = 5
  Width = 40
FEATURE [Part::Box] Box139  label="Cube123"
  AttacherType = Attacher::AttachEngine3D
  Height = 7
  Length = 4
  Placement = pos=(-1,36.6,0) rot=(0,0,1;0rad)
  Width = 1
FEATURE [Part::Box] Box140  label="Cube124"
  AttacherType = Attacher::AttachEngine3D
  Height = 7
  Length = 4
  Placement = pos=(-1,24.4,0) rot=(0,0,1;0rad)
  Width = 1
FEATURE [Part::Box] Box141  label="Cube125"
  AttacherType = Attacher::AttachEngine3D
  Height = 7
  Length = 10
  Placement = pos=(-10,25.4,0) rot=(0,0,1;0rad)
  Width = 2
FEATURE [Part::Box] Box142  label="Cube126"
  AttacherType = Attacher::AttachEngine3D
  Height = 10
  Length = 13
  Placement = pos=(-10.19,0,-1.19) rot=(0,-1,0;0.785398rad)
  Width = 40
FEATURE [Part::Box] Box143  label="Cube127"
  AttacherType = Attacher::AttachEngine3D
  Height = 7
  Length = 10
  Placement = pos=(-10,34.6,0) rot=(0,0,1;0rad)
  Width = 2
FEATURE [Part::MultiFuse] Fusion044
  Shapes = -> [Box138,Box132,Box134,Box141,Box143]
FEATURE [Part::Cut] Cut037
  Base = -> Fusion044
  Tool = -> Box142
FEATURE [Part::MultiFuse] Fusion042
  Shapes = -> [Sphere049,Sphere047,Cut037]
FEATURE [Part::MultiFuse] Fusion045
  Shapes = -> [Sphere050,Sphere048]
FEATURE [Part::Cut] Cut038
  Base = -> Fusion042
  Tool = -> Fusion045
FEATURE [Part::Chamfer] Chamfer012
  Base = -> Cut038
  Edges = 4 edges r=4: [Edge31,Edge37,Edge43,Edge46]
FEATURE [Part::Box] Box144  label="Cube128"
  AttacherType = Attacher::AttachEngine3D
  Height = 7
  Length = 4
  Placement = pos=(-1,27.4,0) rot=(0,0,1;0rad)
  Width = 7.2
FEATURE [Part::MultiFuse] Fusion043
  Shapes = -> [Box144,Box137,Box139,Box133,Box140,Box136]
FEATURE [Part::Cut] Cut040
  Base = -> Chamfer012
  Placement = pos=(-5,40,3) rot=(1,0,0;3.14159rad)
  Tool = -> Fusion043
FEATURE [Part::Cut] Cut039
  Base = -> Cut040
  Placement = pos=(0,40,0) rot=(0,0,-1;1.5708rad)
  Tool = -> Box135
FEATURE [Part::MultiFuse] Fusion048
  Shapes = -> [Box089,Box091,Box090,Box092]
FEATURE [Part::Box] Box145  label="Cube129"
  AttacherType = Attacher::AttachEngine3D
  Height = 15
  Length = 19.5
  Placement = pos=(-9.75,-9.75,-14) rot=(0,0,1;0rad)
  Width = 19.5
FEATURE [Part::Box] Box146  label="Cube130"
  AttacherType = Attacher::AttachEngine3D
  Height = 15
  Length = 19.5
  Placement = pos=(-9.75,-9.75,-3) rot=(0,0,1;0rad)
  Width = 19.5
FEATURE [Part::Chamfer] Chamfer013  label="Octagon"
  Base = -> Box146
  Edges = 4 edges r=4: [Edge1,Edge3,Edge5,Edge7]
FEATURE [Part::Box] Box147  label="Cube131"
  AttacherType = Attacher::AttachEngine3D
  Height = 10
  Length = 24
  Placement = pos=(-12,-12,2.1) rot=(0,0,1;0rad)
  Width = 24
FEATURE [Part::Box] Box148  label="Cube132"
  AttacherType = Attacher::AttachEngine3D
  Height = 14
  Length = 20
  Placement = pos=(-10,-10,0) rot=(0,0,1;0rad)
  Width = 20
FEATURE [Part::Cut] Cut043
  Base = -> Box147
  Tool = -> Box148
FEATURE [Part::Chamfer] Chamfer014  label="Glue Channel"
  Base = -> Cut043
  Edges = 8 edges r=0.95: [Edge4,Edge5,Edge14,Edge16,Edge17,Edge18,Edge19,Edge20]
FEATURE [Part::Cut] Cut047
  Base = -> Cut003
  Tool = -> Chamfer007
FEATURE [Part::Cylinder] Cylinder024
  Angle = 360
  AttacherType = Attacher::AttachEngine3D
  Height = 10
  Placement = pos=(-15,-15,-5) rot=(0,0,1;0rad)
  Radius = 1.7
FEATURE [Part::Cylinder] Cylinder025
  Angle = 360
  AttacherType = Attacher::AttachEngine3D
  Height = 10
  Placement = pos=(15,0,-5) rot=(0,0,1;0rad)
  Radius = 1.7
FEATURE [Part::Cylinder] Cylinder026
  Angle = 360
  AttacherType = Attacher::AttachEngine3D
  Height = 10
  Placement = pos=(-15,15,-5) rot=(0,0,1;0rad)
  Radius = 1.7
FEATURE [Part::MultiFuse] Fusion052  label="Screw Holes to remove ball mags"
  Shapes = -> [Cylinder024,Cylinder025,Cylinder026]
FEATURE [Drawing::FeatureViewAnnotation] Annotation
  Font = Sans
  Rotation = 0
  Scale = 7
  Text = 0.4Added in Holes to Mag plate for removal of magnet
  ViewResult = <g transform="translate(14,23) rotate(0)">\n<text id="Annotation"\n font-family="Sans"\n font-size="7"\n fill="#000000">\n<tspan x="0" dy="1em">0.4Added in Holes to Mag plate for removal of magnet</tspan>\n</text>\n</g>
  Visible = false
  X = 14
  Y = 23
FEATURE [Part::Box] Box149  label="Re-level Edge Clip Block001"
  AttacherType = Attacher::AttachEngine3D
  Height = 10
  Length = 12
  Placement = pos=(-21.5,-2,-7) rot=(0,0,1;0rad)
  Width = 44
FEATURE [Part::Fuse] Fusion  label="Bumps"
  Base = -> Sphere008
  Tool = -> Sphere009
FEATURE [Part::Fuse] Fusion053  label="Holes"
  Base = -> Sphere010
  Tool = -> Sphere011
FEATURE [Part::MultiFuse] Fusion054
  Shapes = -> [Box001,Box002,Box003,Box004,Box005]
FEATURE [Part::Fuse] Fusion055
  Base = -> Fusion
  Tool = -> Fusion054
FEATURE [Part::Cut] Cut
  Base = -> Fusion055
  Tool = -> Fusion053
FEATURE [Part::Cut] Cut056
  Base = -> Cut
  Tool = -> Fusion003
FEATURE [Part::Cut] Cut057
  Base = -> Cut056
  Tool = -> Box013
FEATURE [Part::Cut] Cut058
  Base = -> Cut057
  Tool = -> Box149
FEATURE [Part::Cut] Cut059  label="Edge Clips Master"
  Base = -> Cut058
  Placement = pos=(-20,-20,0) rot=(0,0,1;0rad)
  Tool = -> Box006
FEATURE [Part::Box] Box150  label="Cube133"
  AttacherType = Attacher::AttachEngine3D
  Height = 7
  Length = 5
  Placement = pos=(-5,0,-2) rot=(0,0,1;0rad)
  Width = 40
FEATURE [Part::Box] Box151  label="Cube134"
  AttacherType = Attacher::AttachEngine3D
  Height = 7
  Length = 10
  Placement = pos=(-15,6,-2) rot=(0,0,1;0rad)
  Width = 2
FEATURE [Part::Box] Box152  label="Cube135"
  AttacherType = Attacher::AttachEngine3D
  Height = 7
  Length = 10
  Placement = pos=(-15,10,-2) rot=(0,0,1;0rad)
  Width = 2
FEATURE [Part::Box] Box153  label="Cube136"
  AttacherType = Attacher::AttachEngine3D
  Height = 7
  Length = 10
  Placement = pos=(-15,25.4,-2) rot=(0,0,1;0rad)
  Width = 2
FEATURE [Part::Box] Box154  label="Cube137"
  AttacherType = Attacher::AttachEngine3D
  Height = 7
  Length = 10
  Placement = pos=(-15,34.6,-2) rot=(0,0,1;0rad)
  Width = 2
FEATURE [Part::Sphere] Sphere051
  Angle1 = -90
  Angle2 = 90
  Angle3 = 360
  AttacherType = Attacher::AttachEngine3D
  Placement = pos=(-7.5,6.5,0.5) rot=(0,0,1;0rad)
  Radius = 1.25
FEATURE [Part::Box] Box155  label="Chamfer Cube001"
  AttacherType = Attacher::AttachEngine3D
  Height = 10
  Length = 13
  Placement = pos=(-11.69,0,-1.19) rot=(0,-1,0;0.785398rad)
  Width = 40
FEATURE [Part::Sphere] Sphere052
  Angle1 = -90
  Angle2 = 90
  Angle3 = 360
  AttacherType = Attacher::AttachEngine3D
  Placement = pos=(-7.5,11.5,0.5) rot=(0,0,1;0rad)
  Radius = 1.25
FEATURE [Part::Sphere] Sphere053
  Angle1 = -90
  Angle2 = 90
  Angle3 = 360
  AttacherType = Attacher::AttachEngine3D
  Placement = pos=(-7.5,28,0.5) rot=(0,0,1;0rad)
  Radius = 1.5
FEATURE [Part::Sphere] Sphere054
  Angle1 = -90
  Angle2 = 90
  Angle3 = 360
  AttacherType = Attacher::AttachEngine3D
  Placement = pos=(-7.5,34,0.5) rot=(0,0,1;0rad)
  Radius = 1.5
FEATURE [Part::Box] Box156  label="Cube138"
  AttacherType = Attacher::AttachEngine3D
  Height = 7
  Length = 4
  Placement = pos=(-6,5,-2) rot=(0,0,1;0rad)
  Width = 1
FEATURE [Part::Box] Box157  label="Cube139"
  AttacherType = Attacher::AttachEngine3D
  Height = 7
  Length = 4
  Placement = pos=(-6,8,-2) rot=(0,0,1;0rad)
  Width = 2
FEATURE [Part::Box] Box158  label="Cube140"
  AttacherType = Attacher::AttachEngine3D
  Height = 7
  Length = 4
  Placement = pos=(-6,12,-2) rot=(0,0,1;0rad)
  Width = 1
FEATURE [Part::Box] Box159  label="Cube141"
  AttacherType = Attacher::AttachEngine3D
  Height = 7
  Length = 4
  Placement = pos=(-6,24.4,-2) rot=(0,0,1;0rad)
  Width = 1
FEATURE [Part::Box] Box160  label="Cube142"
  AttacherType = Attacher::AttachEngine3D
  Height = 7
  Length = 4
  Placement = pos=(-6,36.6,-2) rot=(0,0,1;0rad)
  Width = 1
FEATURE [Part::Box] Box161  label="Cube143"
  AttacherType = Attacher::AttachEngine3D
  Height = 7
  Length = 4
  Placement = pos=(-6,27.4,-2) rot=(0,0,1;0rad)
  Width = 7.2
FEATURE [Part::MultiFuse] Fusion056  label="Extra Holes for Clips001"
  Shapes = -> [Box161,Box158,Box160,Box157,Box159,Box156]
FEATURE [Part::Box] Box162  label="Re-level Edge Clip Block002"
  AttacherType = Attacher::AttachEngine3D
  Height = 10
  Length = 20
  Placement = pos=(-19,-2,3) rot=(0,0,1;0rad)
  Width = 44
FEATURE [Part::Box] Box163  label="Re-level Edge Clip Block003"
  AttacherType = Attacher::AttachEngine3D
  Height = 10
  Length = 12
  Placement = pos=(-21.5,-2,-7) rot=(0,0,1;0rad)
  Width = 44
FEATURE [Part::Fuse] Fusion057  label="Bumps001"
  Base = -> Sphere051
  Tool = -> Sphere052
FEATURE [Part::Fuse] Fusion058  label="Holes001"
  Base = -> Sphere053
  Tool = -> Sphere054
FEATURE [Part::MultiFuse] Fusion059
  Shapes = -> [Box150,Box151,Box152,Box153,Box154]
FEATURE [Part::Fuse] Fusion060
  Base = -> Fusion057
  Tool = -> Fusion059
FEATURE [Part::Cut] Cut060
  Base = -> Fusion060
  Tool = -> Fusion058
FEATURE [Part::Cut] Cut061
  Base = -> Cut060
  Tool = -> Fusion056
FEATURE [Part::Cut] Cut062
  Base = -> Cut061
  Tool = -> Box162
FEATURE [Part::Cut] Cut063
  Base = -> Cut062
  Tool = -> Box163
FEATURE [Part::Cut] Cut064  label="Copy Edge Clip"
  Base = -> Cut063
  Placement = pos=(-27,20,-7) rot=(0.707107,0,-0.707107;3.14159rad)
  Tool = -> Box155
FEATURE [Part::Box] Box164  label="Cube144"
  AttacherType = Attacher::AttachEngine3D
  Height = 7
  Length = 5
  Placement = pos=(-5,0,-2) rot=(0,0,1;0rad)
  Width = 40
FEATURE [Part::Box] Box165  label="Cube145"
  AttacherType = Attacher::AttachEngine3D
  Height = 7
  Length = 10
  Placement = pos=(-15,6,-2) rot=(0,0,1;0rad)
  Width = 2
FEATURE [Part::Box] Box166  label="Cube146"
  AttacherType = Attacher::AttachEngine3D
  Height = 7
  Length = 10
  Placement = pos=(-15,10,-2) rot=(0,0,1;0rad)
  Width = 2
FEATURE [Part::Box] Box167  label="Cube147"
  AttacherType = Attacher::AttachEngine3D
  Height = 7
  Length = 10
  Placement = pos=(-15,25.4,-2) rot=(0,0,1;0rad)
  Width = 2
FEATURE [Part::Box] Box168  label="Cube148"
  AttacherType = Attacher::AttachEngine3D
  Height = 7
  Length = 10
  Placement = pos=(-15,34.6,-2) rot=(0,0,1;0rad)
  Width = 2
FEATURE [Part::Sphere] Sphere055
  Angle1 = -90
  Angle2 = 90
  Angle3 = 360
  AttacherType = Attacher::AttachEngine3D
  Placement = pos=(-7.5,6.5,0.5) rot=(0,0,1;0rad)
  Radius = 1.25
FEATURE [Part::Box] Box169  label="Chamfer Cube002"
  AttacherType = Attacher::AttachEngine3D
  Height = 10
  Length = 13
  Placement = pos=(-11.69,0,-1.19) rot=(0,-1,0;0.785398rad)
  Width = 40
FEATURE [Part::Sphere] Sphere056
  Angle1 = -90
  Angle2 = 90
  Angle3 = 360
  AttacherType = Attacher::AttachEngine3D
  Placement = pos=(-7.5,11.5,0.5) rot=(0,0,1;0rad)
  Radius = 1.25
FEATURE [Part::Sphere] Sphere057
  Angle1 = -90
  Angle2 = 90
  Angle3 = 360
  AttacherType = Attacher::AttachEngine3D
  Placement = pos=(-7.5,28,0.5) rot=(0,0,1;0rad)
  Radius = 1.5
FEATURE [Part::Sphere] Sphere058
  Angle1 = -90
  Angle2 = 90
  Angle3 = 360
  AttacherType = Attacher::AttachEngine3D
  Placement = pos=(-7.5,34,0.5) rot=(0,0,1;0rad)
  Radius = 1.5
FEATURE [Part::Box] Box170  label="Cube149"
  AttacherType = Attacher::AttachEngine3D
  Height = 7
  Length = 4
  Placement = pos=(-6,5,-2) rot=(0,0,1;0rad)
  Width = 1
FEATURE [Part::Box] Box171  label="Cube150"
  AttacherType = Attacher::AttachEngine3D
  Height = 7
  Length = 4
  Placement = pos=(-6,8,-2) rot=(0,0,1;0rad)
  Width = 2
FEATURE [Part::Box] Box172  label="Cube151"
  AttacherType = Attacher::AttachEngine3D
  Height = 7
  Length = 4
  Placement = pos=(-6,12,-2) rot=(0,0,1;0rad)
  Width = 1
FEATURE [Part::Box] Box173  label="Cube152"
  AttacherType = Attacher::AttachEngine3D
  Height = 7
  Length = 4
  Placement = pos=(-6,24.4,-2) rot=(0,0,1;0rad)
  Width = 1
FEATURE [Part::Box] Box174  label="Cube153"
  AttacherType = Attacher::AttachEngine3D
  Height = 7
  Length = 4
  Placement = pos=(-6,36.6,-2) rot=(0,0,1;0rad)
  Width = 1
FEATURE [Part::Box] Box175  label="Cube154"
  AttacherType = Attacher::AttachEngine3D
  Height = 7
  Length = 4
  Placement = pos=(-6,27.4,-2) rot=(0,0,1;0rad)
  Width = 7.2
FEATURE [Part::MultiFuse] Fusion061  label="Extra Holes for Clips002"
  Shapes = -> [Box175,Box172,Box174,Box171,Box173,Box170]
FEATURE [Part::Box] Box176  label="Re-level Edge Clip Block004"
  AttacherType = Attacher::AttachEngine3D
  Height = 10
  Length = 20
  Placement = pos=(-19,-2,3) rot=(0,0,1;0rad)
  Width = 44
FEATURE [Part::Box] Box177  label="Re-level Edge Clip Block005"
  AttacherType = Attacher::AttachEngine3D
  Height = 10
  Length = 12
  Placement = pos=(-21.5,-2,-7) rot=(0,0,1;0rad)
  Width = 44
FEATURE [Part::Fuse] Fusion062  label="Bumps002"
  Base = -> Sphere055
  Tool = -> Sphere056
FEATURE [Part::Fuse] Fusion063  label="Holes002"
  Base = -> Sphere057
  Tool = -> Sphere058
FEATURE [Part::MultiFuse] Fusion064
  Shapes = -> [Box164,Box165,Box166,Box167,Box168]
FEATURE [Part::Fuse] Fusion065
  Base = -> Fusion062
  Tool = -> Fusion064
FEATURE [Part::Cut] Cut065
  Base = -> Fusion065
  Tool = -> Fusion063
FEATURE [Part::Cut] Cut066
  Base = -> Cut065
  Tool = -> Fusion061
FEATURE [Part::Cut] Cut067
  Base = -> Cut066
  Tool = -> Box176
FEATURE [Part::Cut] Cut068
  Base = -> Cut067
  Tool = -> Box177
FEATURE [Part::Cut] Cut069  label="Edge Clips001"
  Base = -> Cut068
  Placement = pos=(20,-20,0) rot=(0,0,1;1.5708rad)
  Tool = -> Box169
FEATURE [Part::Box] Box178  label="Cube155"
  AttacherType = Attacher::AttachEngine3D
  Height = 7
  Length = 5
  Placement = pos=(-5,0,-2) rot=(0,0,1;0rad)
  Width = 40
FEATURE [Part::Box] Box179  label="Cube156"
  AttacherType = Attacher::AttachEngine3D
  Height = 7
  Length = 10
  Placement = pos=(-15,10,-2) rot=(0,0,1;0rad)
  Width = 2
FEATURE [Part::Box] Box180  label="Re-level Edge Clip Block006"
  AttacherType = Attacher::AttachEngine3D
  Height = 10
  Length = 20
  Placement = pos=(-19,-2,3) rot=(0,0,1;0rad)
  Width = 44
FEATURE [Part::Box] Box181  label="Cube157"
  AttacherType = Attacher::AttachEngine3D
  Height = 7
  Length = 4
  Placement = pos=(-6,27.4,-2) rot=(0,0,1;0rad)
  Width = 7.2
FEATURE [Part::Box] Box182  label="Cube158"
  AttacherType = Attacher::AttachEngine3D
  Height = 7
  Length = 4
  Placement = pos=(-6,12,-2) rot=(0,0,1;0rad)
  Width = 1
FEATURE [Part::Sphere] Sphere059
  Angle1 = -90
  Angle2 = 90
  Angle3 = 360
  AttacherType = Attacher::AttachEngine3D
  Placement = pos=(-7.5,6.5,0.5) rot=(0,0,1;0rad)
  Radius = 1.25
FEATURE [Part::Box] Box183  label="Cube159"
  AttacherType = Attacher::AttachEngine3D
  Height = 7
  Length = 10
  Placement = pos=(-15,25.4,-2) rot=(0,0,1;0rad)
  Width = 2
FEATURE [Part::Box] Box184  label="Cube160"
  AttacherType = Attacher::AttachEngine3D
  Height = 7
  Length = 4
  Placement = pos=(-6,36.6,-2) rot=(0,0,1;0rad)
  Width = 1
FEATURE [Part::Sphere] Sphere060
  Angle1 = -90
  Angle2 = 90
  Angle3 = 360
  AttacherType = Attacher::AttachEngine3D
  Placement = pos=(-7.5,34,0.5) rot=(0,0,1;0rad)
  Radius = 1.5
FEATURE [Part::Box] Box185  label="Cube161"
  AttacherType = Attacher::AttachEngine3D
  Height = 7
  Length = 4
  Placement = pos=(-6,24.4,-2) rot=(0,0,1;0rad)
  Width = 1
FEATURE [Part::Box] Box186  label="Cube162"
  AttacherType = Attacher::AttachEngine3D
  Height = 7
  Length = 4
  Placement = pos=(-6,8,-2) rot=(0,0,1;0rad)
  Width = 2
FEATURE [Part::Box] Box187  label="Re-level Edge Clip Block007"
  AttacherType = Attacher::AttachEngine3D
  Height = 10
  Length = 12
  Placement = pos=(-21.5,-2,-7) rot=(0,0,1;0rad)
  Width = 44
FEATURE [Part::Sphere] Sphere061
  Angle1 = -90
  Angle2 = 90
  Angle3 = 360
  AttacherType = Attacher::AttachEngine3D
  Placement = pos=(-7.5,11.5,0.5) rot=(0,0,1;0rad)
  Radius = 1.25
FEATURE [Part::Sphere] Sphere062
  Angle1 = -90
  Angle2 = 90
  Angle3 = 360
  AttacherType = Attacher::AttachEngine3D
  Placement = pos=(-7.5,28,0.5) rot=(0,0,1;0rad)
  Radius = 1.5
FEATURE [Part::Fuse] Fusion066  label="Holes003"
  Base = -> Sphere062
  Tool = -> Sphere060
FEATURE [Part::Box] Box188  label="Cube163"
  AttacherType = Attacher::AttachEngine3D
  Height = 7
  Length = 10
  Placement = pos=(-15,34.6,-2) rot=(0,0,1;0rad)
  Width = 2
FEATURE [Part::Box] Box189  label="Cube164"
  AttacherType = Attacher::AttachEngine3D
  Height = 7
  Length = 4
  Placement = pos=(-6,5,-2) rot=(0,0,1;0rad)
  Width = 1
FEATURE [Part::MultiFuse] Fusion067  label="Extra Holes for Clips003"
  Shapes = -> [Box181,Box182,Box184,Box186,Box185,Box189]
FEATURE [Part::Box] Box190  label="Cube165"
  AttacherType = Attacher::AttachEngine3D
  Height = 7
  Length = 10
  Placement = pos=(-15,6,-2) rot=(0,0,1;0rad)
  Width = 2
FEATURE [Part::MultiFuse] Fusion069
  Shapes = -> [Box178,Box190,Box179,Box183,Box188]
FEATURE [Part::Fuse] Fusion070  label="Bumps003"
  Base = -> Sphere059
  Tool = -> Sphere061
FEATURE [Part::Fuse] Fusion068
  Base = -> Fusion070
  Tool = -> Fusion069
FEATURE [Part::Cut] Cut073
  Base = -> Fusion068
  Tool = -> Fusion066
FEATURE [Part::Cut] Cut070
  Base = -> Cut073
  Tool = -> Fusion067
FEATURE [Part::Cut] Cut071
  Base = -> Cut070
  Tool = -> Box180
FEATURE [Part::Cut] Cut072
  Base = -> Cut071
  Tool = -> Box187
FEATURE [Part::Box] Box191  label="Chamfer Cube003"
  AttacherType = Attacher::AttachEngine3D
  Height = 10
  Length = 13
  Placement = pos=(-11.69,0,-1.19) rot=(0,-1,0;0.785398rad)
  Width = 40
FEATURE [Part::Cut] Cut074  label="Edge Clips002"
  Base = -> Cut072
  Placement = pos=(20,20,0) rot=(0,0,1;3.14159rad)
  Tool = -> Box191
FEATURE [Part::Box] Box192  label="Cube166"
  AttacherType = Attacher::AttachEngine3D
  Height = 7
  Length = 10
  Placement = pos=(-15,6,-2) rot=(0,0,1;0rad)
  Width = 2
FEATURE [Part::Box] Box193  label="Chamfer Cube004"
  AttacherType = Attacher::AttachEngine3D
  Height = 10
  Length = 13
  Placement = pos=(-11.69,0,-1.19) rot=(0,-1,0;0.785398rad)
  Width = 40
FEATURE [Part::Box] Box194  label="Re-level Edge Clip Block008"
  AttacherType = Attacher::AttachEngine3D
  Height = 10
  Length = 20
  Placement = pos=(-19,-2,3) rot=(0,0,1;0rad)
  Width = 44
FEATURE [Part::Box] Box195  label="Cube167"
  AttacherType = Attacher::AttachEngine3D
  Height = 7
  Length = 10
  Placement = pos=(-15,10,-2) rot=(0,0,1;0rad)
  Width = 2
FEATURE [Part::Box] Box196  label="Cube168"
  AttacherType = Attacher::AttachEngine3D
  Height = 7
  Length = 5
  Placement = pos=(-5,0,-2) rot=(0,0,1;0rad)
  Width = 40
FEATURE [Part::Box] Box197  label="Cube169"
  AttacherType = Attacher::AttachEngine3D
  Height = 7
  Length = 4
  Placement = pos=(-6,5,-2) rot=(0,0,1;0rad)
  Width = 1
FEATURE [Part::Box] Box198  label="Cube170"
  AttacherType = Attacher::AttachEngine3D
  Height = 7
  Length = 4
  Placement = pos=(-6,12,-2) rot=(0,0,1;0rad)
  Width = 1
FEATURE [Part::Box] Box199  label="Cube171"
  AttacherType = Attacher::AttachEngine3D
  Height = 7
  Length = 4
  Placement = pos=(-6,27.4,-2) rot=(0,0,1;0rad)
  Width = 7.2
FEATURE [Part::Box] Box200  label="Cube172"
  AttacherType = Attacher::AttachEngine3D
  Height = 7
  Length = 4
  Placement = pos=(-6,24.4,-2) rot=(0,0,1;0rad)
  Width = 1
FEATURE [Part::Sphere] Sphere063
  Angle1 = -90
  Angle2 = 90
  Angle3 = 360
  AttacherType = Attacher::AttachEngine3D
  Placement = pos=(-7.5,28,0.5) rot=(0,0,1;0rad)
  Radius = 1.5
FEATURE [Part::Sphere] Sphere064
  Angle1 = -90
  Angle2 = 90
  Angle3 = 360
  AttacherType = Attacher::AttachEngine3D
  Placement = pos=(-7.5,11.5,0.5) rot=(0,0,1;0rad)
  Radius = 1.25
FEATURE [Part::Box] Box201  label="Cube173"
  AttacherType = Attacher::AttachEngine3D
  Height = 7
  Length = 4
  Placement = pos=(-6,8,-2) rot=(0,0,1;0rad)
  Width = 2
FEATURE [Part::Box] Box202  label="Cube174"
  AttacherType = Attacher::AttachEngine3D
  Height = 7
  Length = 10
  Placement = pos=(-15,25.4,-2) rot=(0,0,1;0rad)
  Width = 2
FEATURE [Part::Sphere] Sphere065
  Angle1 = -90
  Angle2 = 90
  Angle3 = 360
  AttacherType = Attacher::AttachEngine3D
  Placement = pos=(-7.5,6.5,0.5) rot=(0,0,1;0rad)
  Radius = 1.25
FEATURE [Part::Fuse] Fusion073  label="Bumps004"
  Base = -> Sphere065
  Tool = -> Sphere064
FEATURE [Part::Sphere] Sphere066
  Angle1 = -90
  Angle2 = 90
  Angle3 = 360
  AttacherType = Attacher::AttachEngine3D
  Placement = pos=(-7.5,34,0.5) rot=(0,0,1;0rad)
  Radius = 1.5
FEATURE [Part::Fuse] Fusion071  label="Holes004"
  Base = -> Sphere063
  Tool = -> Sphere066
FEATURE [Part::Box] Box203  label="Re-level Edge Clip Block009"
  AttacherType = Attacher::AttachEngine3D
  Height = 10
  Length = 12
  Placement = pos=(-21.5,-2,-7) rot=(0,0,1;0rad)
  Width = 44
FEATURE [Part::Box] Box204  label="Cube175"
  AttacherType = Attacher::AttachEngine3D
  Height = 7
  Length = 4
  Placement = pos=(-6,36.6,-2) rot=(0,0,1;0rad)
  Width = 1
FEATURE [Part::MultiFuse] Fusion074  label="Extra Holes for Clips004"
  Shapes = -> [Box199,Box198,Box204,Box201,Box200,Box197]
FEATURE [Part::Box] Box205  label="Cube176"
  AttacherType = Attacher::AttachEngine3D
  Height = 7
  Length = 10
  Placement = pos=(-15,34.6,-2) rot=(0,0,1;0rad)
  Width = 2
FEATURE [Part::MultiFuse] Fusion072
  Shapes = -> [Box196,Box192,Box195,Box202,Box205]
FEATURE [Part::Fuse] Fusion075
  Base = -> Fusion073
  Tool = -> Fusion072
FEATURE [Part::Cut] Cut075
  Base = -> Fusion075
  Tool = -> Fusion071
FEATURE [Part::Cut] Cut076
  Base = -> Cut075
  Tool = -> Fusion074
FEATURE [Part::Cut] Cut078
  Base = -> Cut076
  Tool = -> Box194
FEATURE [Part::Cut] Cut077
  Base = -> Cut078
  Tool = -> Box203
FEATURE [Part::Cut] Cut079  label="Edge Clips003"
  Base = -> Cut077
  Placement = pos=(-20,20,0) rot=(0,0,-1;1.5708rad)
  Tool = -> Box193
FEATURE [Part::MultiFuse] Fusion076  label="Edge Clips Fusion"
  Shapes = -> [Cut059,Cut069,Cut074,Cut079]
FEATURE [Part::Box] Box206  label="Cube177"
  AttacherType = Attacher::AttachEngine3D
  Height = 10
  Length = 10
  Placement = pos=(26,4,1) rot=(0.442189,-0.287968,0.849437;1.66134rad)
  Width = 15
FEATURE [Part::Box] Box207  label="Cube178"
  AttacherType = Attacher::AttachEngine3D
  Height = 10
  Length = 10
  Placement = pos=(-4,26,1) rot=(0.381439,0.080566,0.920876;3.07487rad)
  Width = 15
FEATURE [Part::Box] Box208  label="Cube179"
  AttacherType = Attacher::AttachEngine3D
  Height = 10
  Length = 10
  Placement = pos=(-26,-4,1) rot=(-0.273007,-0.419215,-0.865867;1.78566rad)
  Width = 15
FEATURE [Part::MultiFuse] Fusion078  label="Glue Dents"
  Shapes = -> [Box086,Box208,Box207,Box206]
FEATURE [Part::Box] Box209  label="Cube180"
  AttacherType = Attacher::AttachEngine3D
  Height = 7
  Length = 5
  Placement = pos=(-5,0,-2) rot=(0,0,1;0rad)
  Width = 40
FEATURE [Part::Box] Box210  label="Cube181"
  AttacherType = Attacher::AttachEngine3D
  Height = 7
  Length = 10
  Placement = pos=(-15,6,-2) rot=(0,0,1;0rad)
  Width = 2
FEATURE [Part::Box] Box211  label="Cube182"
  AttacherType = Attacher::AttachEngine3D
  Height = 7
  Length = 10
  Placement = pos=(-15,10,-2) rot=(0,0,1;0rad)
  Width = 2
FEATURE [Part::Box] Box212  label="Cube183"
  AttacherType = Attacher::AttachEngine3D
  Height = 7
  Length = 10
  Placement = pos=(-15,25.4,-2) rot=(0,0,1;0rad)
  Width = 2
FEATURE [Part::Box] Box213  label="Cube184"
  AttacherType = Attacher::AttachEngine3D
  Height = 7
  Length = 10
  Placement = pos=(-15,34.6,-2) rot=(0,0,1;0rad)
  Width = 2
FEATURE [Part::Sphere] Sphere067
  Angle1 = -90
  Angle2 = 90
  Angle3 = 360
  AttacherType = Attacher::AttachEngine3D
  Placement = pos=(-7.5,6.5,0.5) rot=(0,0,1;0rad)
  Radius = 1.25
FEATURE [Part::Box] Box214  label="Chamfer Cube005"
  AttacherType = Attacher::AttachEngine3D
  Height = 10
  Length = 13
  Placement = pos=(-11.69,0,-1.19) rot=(0,-1,0;0.785398rad)
  Width = 40
FEATURE [Part::Sphere] Sphere068
  Angle1 = -90
  Angle2 = 90
  Angle3 = 360
  AttacherType = Attacher::AttachEngine3D
  Placement = pos=(-7.5,11.5,0.5) rot=(0,0,1;0rad)
  Radius = 1.25
FEATURE [Part::Sphere] Sphere069
  Angle1 = -90
  Angle2 = 90
  Angle3 = 360
  AttacherType = Attacher::AttachEngine3D
  Placement = pos=(-7.5,28,0.5) rot=(0,0,1;0rad)
  Radius = 1.5
FEATURE [Part::Sphere] Sphere070
  Angle1 = -90
  Angle2 = 90
  Angle3 = 360
  AttacherType = Attacher::AttachEngine3D
  Placement = pos=(-7.5,34,0.5) rot=(0,0,1;0rad)
  Radius = 1.5
FEATURE [Part::Box] Box215  label="Cube185"
  AttacherType = Attacher::AttachEngine3D
  Height = 7
  Length = 4
  Placement = pos=(-6,5,-2) rot=(0,0,1;0rad)
  Width = 1
FEATURE [Part::Box] Box216  label="Cube186"
  AttacherType = Attacher::AttachEngine3D
  Height = 7
  Length = 4
  Placement = pos=(-6,8,-2) rot=(0,0,1;0rad)
  Width = 2
FEATURE [Part::Box] Box217  label="Cube187"
  AttacherType = Attacher::AttachEngine3D
  Height = 7
  Length = 4
  Placement = pos=(-6,12,-2) rot=(0,0,1;0rad)
  Width = 1
FEATURE [Part::Box] Box218  label="Cube188"
  AttacherType = Attacher::AttachEngine3D
  Height = 7
  Length = 4
  Placement = pos=(-6,24.4,-2) rot=(0,0,1;0rad)
  Width = 1
FEATURE [Part::Box] Box219  label="Cube189"
  AttacherType = Attacher::AttachEngine3D
  Height = 7
  Length = 4
  Placement = pos=(-6,36.6,-2) rot=(0,0,1;0rad)
  Width = 1
FEATURE [Part::Box] Box220  label="Cube190"
  AttacherType = Attacher::AttachEngine3D
  Height = 7
  Length = 4
  Placement = pos=(-6,27.4,-2) rot=(0,0,1;0rad)
  Width = 7.2
FEATURE [Part::MultiFuse] Fusion079  label="Extra Holes for Clips005"
  Shapes = -> [Box220,Box217,Box219,Box216,Box218,Box215]
FEATURE [Part::Box] Box221  label="Re-level Edge Clip Block010"
  AttacherType = Attacher::AttachEngine3D
  Height = 10
  Length = 20
  Placement = pos=(-19,-2,3) rot=(0,0,1;0rad)
  Width = 44
FEATURE [Part::Box] Box222  label="Re-level Edge Clip Block011"
  AttacherType = Attacher::AttachEngine3D
  Height = 10
  Length = 12
  Placement = pos=(-21.5,-2,-7) rot=(0,0,1;0rad)
  Width = 44
FEATURE [Part::Fuse] Fusion080  label="Bumps005"
  Base = -> Sphere067
  Tool = -> Sphere068
FEATURE [Part::Fuse] Fusion081  label="Holes005"
  Base = -> Sphere069
  Tool = -> Sphere070
FEATURE [Part::MultiFuse] Fusion082
  Shapes = -> [Box209,Box210,Box211,Box212,Box213]
FEATURE [Part::Fuse] Fusion083
  Base = -> Fusion080
  Tool = -> Fusion082
FEATURE [Part::Cut] Cut082
  Base = -> Fusion083
  Tool = -> Fusion081
FEATURE [Part::Cut] Cut083
  Base = -> Cut082
  Tool = -> Fusion079
FEATURE [Part::Cut] Cut084
  Base = -> Cut083
  Tool = -> Box221
FEATURE [Part::Cut] Cut085
  Base = -> Cut084
  Tool = -> Box222
FEATURE [Part::Cut] Cut086  label="Edge Clips Master001"
  Base = -> Cut085
  Placement = pos=(-20,-20,0) rot=(0,0,1;0rad)
  Tool = -> Box214
FEATURE [Part::Box] Box223  label="Cube191"
  AttacherType = Attacher::AttachEngine3D
  Height = 7
  Length = 5
  Placement = pos=(-5,0,-2) rot=(0,0,1;0rad)
  Width = 40
FEATURE [Part::Box] Box224  label="Cube192"
  AttacherType = Attacher::AttachEngine3D
  Height = 7
  Length = 4
  Placement = pos=(-6,8,-2) rot=(0,0,1;0rad)
  Width = 2
FEATURE [Part::Box] Box225  label="Chamfer Cube006"
  AttacherType = Attacher::AttachEngine3D
  Height = 10
  Length = 13
  Placement = pos=(-11.69,0,-1.19) rot=(0,-1,0;0.785398rad)
  Width = 40
FEATURE [Part::Box] Box226  label="Cube193"
  AttacherType = Attacher::AttachEngine3D
  Height = 7
  Length = 10
  Placement = pos=(-15,6,-2) rot=(0,0,1;0rad)
  Width = 2
FEATURE [Part::Sphere] Sphere071
  Angle1 = -90
  Angle2 = 90
  Angle3 = 360
  AttacherType = Attacher::AttachEngine3D
  Placement = pos=(-7.5,11.5,0.5) rot=(0,0,1;0rad)
  Radius = 1.25
FEATURE [Part::Box] Box227  label="Cube194"
  AttacherType = Attacher::AttachEngine3D
  Height = 7
  Length = 4
  Placement = pos=(-6,27.4,-2) rot=(0,0,1;0rad)
  Width = 7.2
FEATURE [Part::Box] Box228  label="Cube195"
  AttacherType = Attacher::AttachEngine3D
  Height = 7
  Length = 4
  Placement = pos=(-6,12,-2) rot=(0,0,1;0rad)
  Width = 1
FEATURE [Part::Box] Box229  label="Cube196"
  AttacherType = Attacher::AttachEngine3D
  Height = 7
  Length = 4
  Placement = pos=(-6,24.4,-2) rot=(0,0,1;0rad)
  Width = 1
FEATURE [Part::Sphere] Sphere072
  Angle1 = -90
  Angle2 = 90
  Angle3 = 360
  AttacherType = Attacher::AttachEngine3D
  Placement = pos=(-7.5,6.5,0.5) rot=(0,0,1;0rad)
  Radius = 1.25
FEATURE [Part::Box] Box230  label="Cube197"
  AttacherType = Attacher::AttachEngine3D
  Height = 7
  Length = 4
  Placement = pos=(-6,36.6,-2) rot=(0,0,1;0rad)
  Width = 1
FEATURE [Part::Box] Box231  label="Cube198"
  AttacherType = Attacher::AttachEngine3D
  Height = 7
  Length = 10
  Placement = pos=(-15,10,-2) rot=(0,0,1;0rad)
  Width = 2
FEATURE [Part::Sphere] Sphere073
  Angle1 = -90
  Angle2 = 90
  Angle3 = 360
  AttacherType = Attacher::AttachEngine3D
  Placement = pos=(-7.5,34,0.5) rot=(0,0,1;0rad)
  Radius = 1.5
FEATURE [Part::Box] Box232  label="Cube199"
  AttacherType = Attacher::AttachEngine3D
  Height = 7
  Length = 4
  Placement = pos=(-6,5,-2) rot=(0,0,1;0rad)
  Width = 1
FEATURE [Part::MultiFuse] Fusion085  label="Extra Holes for Clips006"
  Shapes = -> [Box227,Box228,Box230,Box224,Box229,Box232]
FEATURE [Part::Box] Box233  label="Re-level Edge Clip Block012"
  AttacherType = Attacher::AttachEngine3D
  Height = 10
  Length = 20
  Placement = pos=(-19,-2,3) rot=(0,0,1;0rad)
  Width = 44
FEATURE [Part::Box] Box234  label="Cube200"
  AttacherType = Attacher::AttachEngine3D
  Height = 7
  Length = 10
  Placement = pos=(-15,34.6,-2) rot=(0,0,1;0rad)
  Width = 2
FEATURE [Part::Box] Box235  label="Cube201"
  AttacherType = Attacher::AttachEngine3D
  Height = 7
  Length = 10
  Placement = pos=(-15,25.4,-2) rot=(0,0,1;0rad)
  Width = 2
FEATURE [Part::MultiFuse] Fusion086
  Shapes = -> [Box223,Box226,Box231,Box235,Box234]
FEATURE [Part::Fuse] Fusion087  label="Bumps006"
  Base = -> Sphere072
  Tool = -> Sphere071
FEATURE [Part::Fuse] Fusion084
  Base = -> Fusion087
  Tool = -> Fusion086
FEATURE [Part::Sphere] Sphere074
  Angle1 = -90
  Angle2 = 90
  Angle3 = 360
  AttacherType = Attacher::AttachEngine3D
  Placement = pos=(-7.5,28,0.5) rot=(0,0,1;0rad)
  Radius = 1.5
FEATURE [Part::Fuse] Fusion088  label="Holes006"
  Base = -> Sphere074
  Tool = -> Sphere073
FEATURE [Part::Box] Box236  label="Re-level Edge Clip Block013"
  AttacherType = Attacher::AttachEngine3D
  Height = 10
  Length = 12
  Placement = pos=(-21.5,-2,-7) rot=(0,0,1;0rad)
  Width = 44
FEATURE [Part::Cut] Cut087
  Base = -> Fusion084
  Tool = -> Fusion088
FEATURE [Part::Cut] Cut088
  Base = -> Cut087
  Tool = -> Fusion085
FEATURE [Part::Cut] Cut089
  Base = -> Cut088
  Tool = -> Box233
FEATURE [Part::Cut] Cut090
  Base = -> Cut089
  Tool = -> Box236
FEATURE [Part::Cut] Cut091  label="Edge Clips004"
  Base = -> Cut090
  Placement = pos=(20,-20,0) rot=(0,0,1;1.5708rad)
  Tool = -> Box225
FEATURE [Part::Box] Box237  label="Re-level Edge Clip Block014"
  AttacherType = Attacher::AttachEngine3D
  Height = 10
  Length = 12
  Placement = pos=(-21.5,-2,-7) rot=(0,0,1;0rad)
  Width = 44
FEATURE [Part::Box] Box238  label="Cube202"
  AttacherType = Attacher::AttachEngine3D
  Height = 7
  Length = 4
  Placement = pos=(-6,36.6,-2) rot=(0,0,1;0rad)
  Width = 1
FEATURE [Part::Box] Box239  label="Cube203"
  AttacherType = Attacher::AttachEngine3D
  Height = 7
  Length = 10
  Placement = pos=(-15,10,-2) rot=(0,0,1;0rad)
  Width = 2
FEATURE [Part::Box] Box240  label="Cube204"
  AttacherType = Attacher::AttachEngine3D
  Height = 7
  Length = 10
  Placement = pos=(-15,25.4,-2) rot=(0,0,1;0rad)
  Width = 2
FEATURE [Part::Box] Box241  label="Re-level Edge Clip Block015"
  AttacherType = Attacher::AttachEngine3D
  Height = 10
  Length = 20
  Placement = pos=(-19,-2,3) rot=(0,0,1;0rad)
  Width = 44
FEATURE [Part::Box] Box242  label="Cube205"
  AttacherType = Attacher::AttachEngine3D
  Height = 7
  Length = 10
  Placement = pos=(-15,34.6,-2) rot=(0,0,1;0rad)
  Width = 2
FEATURE [Part::Sphere] Sphere075
  Angle1 = -90
  Angle2 = 90
  Angle3 = 360
  AttacherType = Attacher::AttachEngine3D
  Placement = pos=(-7.5,34,0.5) rot=(0,0,1;0rad)
  Radius = 1.5
FEATURE [Part::Sphere] Sphere076
  Angle1 = -90
  Angle2 = 90
  Angle3 = 360
  AttacherType = Attacher::AttachEngine3D
  Placement = pos=(-7.5,28,0.5) rot=(0,0,1;0rad)
  Radius = 1.5
FEATURE [Part::Fuse] Fusion089  label="Holes007"
  Base = -> Sphere076
  Tool = -> Sphere075
FEATURE [Part::Box] Box243  label="Cube206"
  AttacherType = Attacher::AttachEngine3D
  Height = 7
  Length = 4
  Placement = pos=(-6,5,-2) rot=(0,0,1;0rad)
  Width = 1
FEATURE [Part::Box] Box244  label="Cube207"
  AttacherType = Attacher::AttachEngine3D
  Height = 7
  Length = 4
  Placement = pos=(-6,24.4,-2) rot=(0,0,1;0rad)
  Width = 1
FEATURE [Part::Sphere] Sphere077
  Angle1 = -90
  Angle2 = 90
  Angle3 = 360
  AttacherType = Attacher::AttachEngine3D
  Placement = pos=(-7.5,11.5,0.5) rot=(0,0,1;0rad)
  Radius = 1.25
FEATURE [Part::Box] Box245  label="Cube208"
  AttacherType = Attacher::AttachEngine3D
  Height = 7
  Length = 4
  Placement = pos=(-6,12,-2) rot=(0,0,1;0rad)
  Width = 1
FEATURE [Part::Box] Box246  label="Chamfer Cube007"
  AttacherType = Attacher::AttachEngine3D
  Height = 10
  Length = 13
  Placement = pos=(-11.69,0,-1.19) rot=(0,-1,0;0.785398rad)
  Width = 40
FEATURE [Part::Sphere] Sphere078
  Angle1 = -90
  Angle2 = 90
  Angle3 = 360
  AttacherType = Attacher::AttachEngine3D
  Placement = pos=(-7.5,6.5,0.5) rot=(0,0,1;0rad)
  Radius = 1.25
FEATURE [Part::Fuse] Fusion090  label="Bumps007"
  Base = -> Sphere078
  Tool = -> Sphere077
FEATURE [Part::Box] Box247  label="Cube209"
  AttacherType = Attacher::AttachEngine3D
  Height = 7
  Length = 5
  Placement = pos=(-5,0,-2) rot=(0,0,1;0rad)
  Width = 40
FEATURE [Part::Box] Box248  label="Cube210"
  AttacherType = Attacher::AttachEngine3D
  Height = 7
  Length = 4
  Placement = pos=(-6,27.4,-2) rot=(0,0,1;0rad)
  Width = 7.2
FEATURE [Part::Box] Box249  label="Cube211"
  AttacherType = Attacher::AttachEngine3D
  Height = 7
  Length = 4
  Placement = pos=(-6,8,-2) rot=(0,0,1;0rad)
  Width = 2
FEATURE [Part::MultiFuse] Fusion091  label="Extra Holes for Clips007"
  Shapes = -> [Box248,Box245,Box238,Box249,Box244,Box243]
FEATURE [Part::Box] Box250  label="Cube212"
  AttacherType = Attacher::AttachEngine3D
  Height = 7
  Length = 10
  Placement = pos=(-15,6,-2) rot=(0,0,1;0rad)
  Width = 2
FEATURE [Part::MultiFuse] Fusion092
  Shapes = -> [Box247,Box250,Box239,Box240,Box242]
FEATURE [Part::Fuse] Fusion093
  Base = -> Fusion090
  Tool = -> Fusion092
FEATURE [Part::Cut] Cut093
  Base = -> Fusion093
  Tool = -> Fusion089
FEATURE [Part::Cut] Cut094
  Base = -> Cut093
  Tool = -> Fusion091
FEATURE [Part::Cut] Cut095
  Base = -> Cut094
  Tool = -> Box241
FEATURE [Part::Cut] Cut096
  Base = -> Cut095
  Tool = -> Box237
FEATURE [Part::Cut] Cut092  label="Edge Clips005"
  Base = -> Cut096
  Placement = pos=(20,20,0) rot=(0,0,1;3.14159rad)
  Tool = -> Box246
FEATURE [Part::Box] Box251  label="Re-level Edge Clip Block016"
  AttacherType = Attacher::AttachEngine3D
  Height = 10
  Length = 12
  Placement = pos=(-21.5,-2,-7) rot=(0,0,1;0rad)
  Width = 44
FEATURE [Part::Box] Box252  label="Cube213"
  AttacherType = Attacher::AttachEngine3D
  Height = 7
  Length = 10
  Placement = pos=(-15,10,-2) rot=(0,0,1;0rad)
  Width = 2
FEATURE [Part::Box] Box253  label="Cube214"
  AttacherType = Attacher::AttachEngine3D
  Height = 7
  Length = 4
  Placement = pos=(-6,12,-2) rot=(0,0,1;0rad)
  Width = 1
FEATURE [Part::Box] Box254  label="Chamfer Cube008"
  AttacherType = Attacher::AttachEngine3D
  Height = 10
  Length = 13
  Placement = pos=(-11.69,0,-1.19) rot=(0,-1,0;0.785398rad)
  Width = 40
FEATURE [Part::Sphere] Sphere079
  Angle1 = -90
  Angle2 = 90
  Angle3 = 360
  AttacherType = Attacher::AttachEngine3D
  Placement = pos=(-7.5,6.5,0.5) rot=(0,0,1;0rad)
  Radius = 1.25
FEATURE [Part::Box] Box255  label="Cube215"
  AttacherType = Attacher::AttachEngine3D
  Height = 7
  Length = 5
  Placement = pos=(-5,0,-2) rot=(0,0,1;0rad)
  Width = 40
FEATURE [Part::Box] Box256  label="Cube216"
  AttacherType = Attacher::AttachEngine3D
  Height = 7
  Length = 4
  Placement = pos=(-6,27.4,-2) rot=(0,0,1;0rad)
  Width = 7.2
FEATURE [Part::Box] Box257  label="Cube217"
  AttacherType = Attacher::AttachEngine3D
  Height = 7
  Length = 4
  Placement = pos=(-6,8,-2) rot=(0,0,1;0rad)
  Width = 2
FEATURE [Part::Box] Box258  label="Cube218"
  AttacherType = Attacher::AttachEngine3D
  Height = 7
  Length = 10
  Placement = pos=(-15,6,-2) rot=(0,0,1;0rad)
  Width = 2
FEATURE [Part::Sphere] Sphere080
  Angle1 = -90
  Angle2 = 90
  Angle3 = 360
  AttacherType = Attacher::AttachEngine3D
  Placement = pos=(-7.5,28,0.5) rot=(0,0,1;0rad)
  Radius = 1.5
FEATURE [Part::Box] Box259  label="Cube219"
  AttacherType = Attacher::AttachEngine3D
  Height = 7
  Length = 4
  Placement = pos=(-6,5,-2) rot=(0,0,1;0rad)
  Width = 1
FEATURE [Part::Box] Box260  label="Cube220"
  AttacherType = Attacher::AttachEngine3D
  Height = 7
  Length = 4
  Placement = pos=(-6,24.4,-2) rot=(0,0,1;0rad)
  Width = 1
FEATURE [Part::Sphere] Sphere081
  Angle1 = -90
  Angle2 = 90
  Angle3 = 360
  AttacherType = Attacher::AttachEngine3D
  Placement = pos=(-7.5,11.5,0.5) rot=(0,0,1;0rad)
  Radius = 1.25
FEATURE [Part::Box] Box261  label="Re-level Edge Clip Block017"
  AttacherType = Attacher::AttachEngine3D
  Height = 10
  Length = 20
  Placement = pos=(-19,-2,3) rot=(0,0,1;0rad)
  Width = 44
FEATURE [Part::Box] Box262  label="Cube221"
  AttacherType = Attacher::AttachEngine3D
  Height = 7
  Length = 10
  Placement = pos=(-15,34.6,-2) rot=(0,0,1;0rad)
  Width = 2
FEATURE [Part::Box] Box263  label="Cube222"
  AttacherType = Attacher::AttachEngine3D
  Height = 7
  Length = 10
  Placement = pos=(-15,25.4,-2) rot=(0,0,1;0rad)
  Width = 2
FEATURE [Part::MultiFuse] Fusion096
  Shapes = -> [Box255,Box258,Box252,Box263,Box262]
FEATURE [Part::Box] Box264  label="Cube223"
  AttacherType = Attacher::AttachEngine3D
  Height = 7
  Length = 4
  Placement = pos=(-6,36.6,-2) rot=(0,0,1;0rad)
  Width = 1
FEATURE [Part::MultiFuse] Fusion095  label="Extra Holes for Clips008"
  Shapes = -> [Box256,Box253,Box264,Box257,Box260,Box259]
FEATURE [Part::Fuse] Fusion098  label="Bumps008"
  Base = -> Sphere079
  Tool = -> Sphere081
FEATURE [Part::Fuse] Fusion094
  Base = -> Fusion098
  Tool = -> Fusion096
FEATURE [Part::Sphere] Sphere082
  Angle1 = -90
  Angle2 = 90
  Angle3 = 360
  AttacherType = Attacher::AttachEngine3D
  Placement = pos=(-7.5,34,0.5) rot=(0,0,1;0rad)
  Radius = 1.5
FEATURE [Part::Fuse] Fusion097  label="Holes008"
  Base = -> Sphere080
  Tool = -> Sphere082
FEATURE [Part::Cut] Cut101
  Base = -> Fusion094
  Tool = -> Fusion097
FEATURE [Part::Cut] Cut097
  Base = -> Cut101
  Tool = -> Fusion095
FEATURE [Part::Cut] Cut098
  Base = -> Cut097
  Tool = -> Box261
FEATURE [Part::Cut] Cut099
  Base = -> Cut098
  Tool = -> Box251
FEATURE [Part::Cut] Cut100  label="Edge Clips006"
  Base = -> Cut099
  Placement = pos=(-20,20,0) rot=(0,0,-1;1.5708rad)
  Tool = -> Box254
FEATURE [Part::Box] Box265  label="Cube224"
  AttacherType = Attacher::AttachEngine3D
  Height = 10
  Length = 10
  Placement = pos=(4,-26,1) rot=(0.205904,-0.974848,-0.085288;0.803573rad)
  Width = 15
FEATURE [Part::Box] Box266  label="Cube225"
  AttacherType = Attacher::AttachEngine3D
  Height = 10
  Length = 10
  Placement = pos=(-26,-4,1) rot=(-0.273007,-0.419215,-0.865867;1.78566rad)
  Width = 15
FEATURE [Part::Box] Box267  label="Cube226"
  AttacherType = Attacher::AttachEngine3D
  Height = 10
  Length = 10
  Placement = pos=(-4,26,1) rot=(0.381439,0.080566,0.920876;3.07487rad)
  Width = 15
FEATURE [Part::Box] Box268  label="Cube227"
  AttacherType = Attacher::AttachEngine3D
  Height = 10
  Length = 10
  Placement = pos=(26,4,1) rot=(0.442189,-0.287968,0.849437;1.66134rad)
  Width = 15
FEATURE [Part::MultiFuse] Fusion099  label="Glue Dents001"
  Shapes = -> [Box265,Box266,Box267,Box268]
FEATURE [Part::MultiFuse] Fusion100  label="Edge Clips Fusion001"
  Shapes = -> [Cut100,Cut086,Cut091,Cut092]
FEATURE [Drawing::FeatureViewAnnotation] Annotation001
  Font = Sans
  Rotation = 0
  Scale = 7
  Text = 0.5 rejigged whole thing, stopped clips overhang and moved bump and holes back 0.5
  ViewResult = <g transform="translate(14,30) rotate(0)">\n<text id="Annotation001"\n font-family="Sans"\n font-size="7"\n fill="#000000">\n<tspan x="0" dy="1em">0.5 rejigged whole thing, stopped clips overhang and moved bump and holes back 0.5</tspan>\n</text>\n</g>
  Visible = false
  X = 14
  Y = 30
FEATURE [Part::Cylinder] Cylinder027  label="z-axis"
  Angle = 360
  AttacherType = Attacher::AttachEngine3D
  Height = 73
  Placement = pos=(0,0,-18) rot=(0,0,1;0rad)
  Radius = 0.5
FEATURE [Part::MultiFuse] Fusion101
  Placement = pos=(-15,-15,0) rot=(0,0,1;0rad)
  Shapes = -> [Box069,Cylinder018,Sphere030]
FEATURE [Part::Box] Box269  label="Square Nut Hole 024"
  AttacherType = Attacher::AttachEngine3D
  Height = 2
  Length = 5.8
  Placement = pos=(-2.9,2.9,2.1) rot=(1,0,0;3.14159rad)
  Width = 5.8
FEATURE [Part::Cylinder] Cylinder028
  Angle = 360
  AttacherType = Attacher::AttachEngine3D
  Height = 10
  Placement = pos=(0,0,6.7) rot=(1,0,0;3.14159rad)
  Radius = 1.7
FEATURE [Part::Sphere] Sphere083
  Angle1 = -90
  Angle2 = 90
  Angle3 = 360
  AttacherType = Attacher::AttachEngine3D
  Placement = pos=(0,0,4.3) rot=(1,0,0;3.14159rad)
  Radius = 3.35
FEATURE [Part::MultiFuse] Fusion102
  Placement = pos=(-15,0,0) rot=(0,0,1;0rad)
  Shapes = -> [Box269,Cylinder028,Sphere083]
FEATURE [Part::Fuse] Fusion103
  Base = -> Fusion101
  Tool = -> Fusion102
FEATURE [Part::Feature] Fusion103001
  Placement = pos=(0,0,0) rot=(0,0,1;1.5708rad)
  shape: bbox 21.7 x 6.7 x 10.95 mm, 18 faces, 2 solids (baked)
FEATURE [Part::Feature] Fusion103002
  Placement = pos=(0,0,0) rot=(0,0,1;3.14159rad)
  shape: bbox 6.7 x 21.7 x 10.95 mm, 18 faces, 2 solids (baked)
FEATURE [Part::Feature] Fusion103003
  Placement = pos=(0,0,0) rot=(0,0,-1;1.5708rad)
  shape: bbox 21.7 x 6.7 x 10.95 mm, 18 faces, 2 solids (baked)
FEATURE [Part::MultiFuse] Fusion103004  label="Nut Holes"
  Shapes = -> [Fusion103,Fusion103001,Fusion103002,Fusion103003]
FEATURE [Part::Fuse] Fusion103005  label="Cube with Edge Clips"
  Base = -> Box075
  Tool = -> Fusion100
FEATURE [Part::Cut] Cut102
  Base = -> Fusion103005
  Tool = -> Fusion099
FEATURE [Part::Cut] Cut103
  Base = -> Cut102
  Tool = -> Fusion103004
FEATURE [Part::Cut] Cut104
  Base = -> Cut103
  Tool = -> Chamfer014
FEATURE [Part::Cut] Cut105
  Base = -> Cut104
  Tool = -> Chamfer013
FEATURE [Part::Cut] Cut106  label="Nut Plate 1.1"
  Base = -> Cut105
  Tool = -> Box145
FEATURE [Part::Fuse] Fusion103006
  Base = -> Cut047
  Tool = -> Fusion076
FEATURE [Part::Cut] Cut107
  Base = -> Fusion103006
  Tool = -> Fusion052
FEATURE [Part::Cut] Cut108
  Base = -> Cut107
  Tool = -> Chamfer008
FEATURE [Part::Cut] Cut109
  Base = -> Cut108
  Tool = -> Box085
FEATURE [Part::Cut] Cut110  label="Ball Plate 1.1"
  Base = -> Cut109
  Tool = -> Fusion078
FEATURE [Drawing::FeatureViewAnnotation] Annotation002
  Font = Sans
  Rotation = 0
  Scale = 7
  ViewResult = <g transform="translate(10,10) rotate(0)">\n<text id="Annotation002"\n font-family="Sans"\n font-size="7"\n fill="#000000">\n<tspan x="0" dy="1em"></tspan>\n</text>\n</g>
  Visible = true
  X = 10
  Y = 10
FEATURE [Drawing::FeatureViewAnnotation] Annotation003
  Font = Sans
  Rotation = 0
  Scale = 7
  Text = Robot 0.X
  ViewResult = <g transform="translate(14,18) rotate(0)">\n<text id="Annotation003"\n font-family="Sans"\n font-size="7"\n fill="#000000">\n<tspan x="0" dy="1em">Robot 0.X</tspan>\n</text>\n</g>
  Visible = true
  X = 14
  Y = 18
FEATURE [Drawing::FeatureViewAnnotation] Annotation004
  Font = Sans
  Rotation = 0
  Scale = 7
  ViewResult = <g transform="translate(10,10) rotate(0)">\n<text id="Annotation004"\n font-family="Sans"\n font-size="7"\n fill="#000000">\n<tspan x="0" dy="1em"></tspan>\n</text>\n</g>
  Visible = true
  X = 10
  Y = 10
FEATURE [Drawing::FeatureViewAnnotation] Annotation005
  Font = Sans
  Rotation = 0
  Scale = 5
  Text = Robot 0.1 - AB added Gripper Mecanism to SB\'s Plates
  ViewResult = <g transform="translate(10,30) rotate(0)">\n<text id="Annotation005"\n font-family="Sans"\n font-size="5"\n fill="#000000">\n<tspan x="0" dy="1em">Robot 0.1 - AB added Gripper Mecanism to SB\'s Plates</tspan>\n</text>\n</g>
  Visible = true
  X = 10
  Y = 30
FEATURE [Drawing::FeatureViewAnnotation] Annotation006
  Font = Sans
  Rotation = 0
  Scale = 5
  Text = Robot 0.2 - Reduced tooth size on small gear
  ViewResult = <g transform="translate(10,40) rotate(0)">\n<text id="Annotation006"\n font-family="Sans"\n font-size="5"\n fill="#000000">\n<tspan x="0" dy="1em">Robot 0.2 - Reduced tooth size on small gear</tspan>\n<tspan x="0" dy="1em"></tspan>\n</text>\n</g>
  Visible = true
  X = 10
  Y = 40
FEATURE [Part::Cylinder] Cylinder029
  Angle = 360
  AttacherType = Attacher::AttachEngine3D
  Height = 10
  Placement = pos=(15,-15,-5) rot=(0,0,1;1.5708rad)
  Radius = 1.7
FEATURE [Part::Sphere] Sphere084  label="Mag Hole001"
  Angle1 = -90
  Angle2 = 90
  Angle3 = 360
  AttacherType = Attacher::AttachEngine3D
  Placement = pos=(15,-15,1.7) rot=(0,0,1;1.5708rad)
  Radius = 2.83
FEATURE [Part::Sphere] Sphere085  label="Mag Hole002"
  Angle1 = -90
  Angle2 = 90
  Angle3 = 360
  AttacherType = Attacher::AttachEngine3D
  Placement = pos=(15,15,1.7) rot=(0,0,1;3.14159rad)
  Radius = 2.83
FEATURE [Part::Sphere] Sphere086  label="Mag Hole 004"
  Angle1 = -90
  Angle2 = 90
  Angle3 = 360
  AttacherType = Attacher::AttachEngine3D
  Placement = pos=(3e-15,15,1.7) rot=(0,0,1;1.5708rad)
  Radius = 2.825
FEATURE [Part::Sphere] Sphere087  label="Mag Hole 005"
  Angle1 = -90
  Angle2 = 90
  Angle3 = 360
  AttacherType = Attacher::AttachEngine3D
  Placement = pos=(-15,2e-15,1.7) rot=(0,0,1;3.14159rad)
  Radius = 2.825
FEATURE [Part::Sphere] Sphere088  label="Mag Hole 006"
  Angle1 = -90
  Angle2 = 90
  Angle3 = 360
  AttacherType = Attacher::AttachEngine3D
  Placement = pos=(-3e-15,-15,1.7) rot=(0,0,-1;1.5708rad)
  Radius = 2.825
FEATURE [Part::Cylinder] Cylinder030
  Angle = 360
  AttacherType = Attacher::AttachEngine3D
  Height = 10
  Placement = pos=(15,15,-5) rot=(0,0,1;3.14159rad)
  Radius = 1.7
FEATURE [Part::Cylinder] Cylinder031
  Angle = 360
  AttacherType = Attacher::AttachEngine3D
  Height = 10
  Placement = pos=(3e-15,15,-5) rot=(0,0,1;1.5708rad)
  Radius = 1.7
FEATURE [Part::Cylinder] Cylinder032
  Angle = 360
  AttacherType = Attacher::AttachEngine3D
  Height = 10
  Placement = pos=(-15,6e-15,-5) rot=(0,0,1;3.14159rad)
  Radius = 1.7
FEATURE [Part::Cylinder] Cylinder033
  Angle = 360
  AttacherType = Attacher::AttachEngine3D
  Height = 10
  Placement = pos=(-9e-15,-15,-5) rot=(0,0,-1;1.5708rad)
  Radius = 1.7
FEATURE [Part::MultiFuse] Fusion103007
  Shapes = -> [Cylinder029,Sphere087,Sphere084,Sphere086,Sphere088,Cylinder032,Cylinder033,Sphere085,Cylinder031,Cylinder030]
FEATURE [Part::Cut] Cut111  label="Ball Plate with Extra Holes"
  Base = -> Cut110
  Tool = -> Fusion103007
FEATURE [Part::Cylinder] Cylinder034
  Angle = 360
  AttacherType = Attacher::AttachEngine3D
  Height = 4
  Placement = pos=(-9.75,-9.75,-3) rot=(0,0,1;0rad)
  Radius = 1.5
FEATURE [Part::Cylinder] Cylinder035
  Angle = 360
  AttacherType = Attacher::AttachEngine3D
  Height = 4
  Placement = pos=(9.75,9.75,-3) rot=(0,0,1;0rad)
  Radius = 1.5
FEATURE [Part::Cylinder] Cylinder036
  Angle = 360
  AttacherType = Attacher::AttachEngine3D
  Height = 4
  Placement = pos=(-9.75,9.75,-3) rot=(0,0,1;0rad)
  Radius = 1.5
FEATURE [Part::Cylinder] Cylinder037
  Angle = 360
  AttacherType = Attacher::AttachEngine3D
  Height = 4
  Placement = pos=(9.75,-9.75,-3) rot=(0,0,1;0rad)
  Radius = 1.5
FEATURE [Part::MultiFuse] Fusion103008
  Shapes = -> [Cylinder034,Cylinder037,Cylinder036,Cylinder035]
FEATURE [Part::Cut] Cut112  label="Ball Plate 1.2"
  Base = -> Cut111
  Tool = -> Fusion103008
FEATURE [Part::Cylinder] Cylinder038
  Angle = 360
  AttacherType = Attacher::AttachEngine3D
  Height = 4
  Placement = pos=(-9.75,-9.75,-3) rot=(0,0,1;0rad)
  Radius = 1.5
FEATURE [Part::Cylinder] Cylinder039
  Angle = 360
  AttacherType = Attacher::AttachEngine3D
  Height = 4
  Placement = pos=(9.75,-9.75,-3) rot=(0,0,1;0rad)
  Radius = 1.5
FEATURE [Part::Cylinder] Cylinder040
  Angle = 360
  AttacherType = Attacher::AttachEngine3D
  Height = 4
  Placement = pos=(-9.75,9.75,-3) rot=(0,0,1;0rad)
  Radius = 1.5
FEATURE [Part::Cylinder] Cylinder041
  Angle = 360
  AttacherType = Attacher::AttachEngine3D
  Height = 4
  Placement = pos=(9.75,9.75,-3) rot=(0,0,1;0rad)
  Radius = 1.5
FEATURE [Part::MultiFuse] Fusion103009
  Shapes = -> [Cylinder038,Cylinder041,Cylinder039,Cylinder040]
FEATURE [Part::Cut] Cut113  label="Nut Plate 1.2"
  Base = -> Cut106
  Tool = -> Fusion103009
FEATURE [Drawing::FeatureViewAnnotation] Annotation007
  Font = Sans
  Rotation = 0
  Scale = 7
  ViewResult = <g transform="translate(10,10) rotate(0)">\n<text id="Annotation007"\n font-family="Sans"\n font-size="7"\n fill="#000000">\n<tspan x="0" dy="1em"></tspan>\n</text>\n</g>
  Visible = true
  X = 10
  Y = 10
FEATURE [Drawing::FeatureViewAnnotation] Annotation008
  Font = Sans
  Rotation = 0
  Scale = 7
  ViewResult = <g transform="translate(10,10) rotate(0)">\n<text id="Annotation008"\n font-family="Sans"\n font-size="7"\n fill="#000000">\n<tspan x="0" dy="1em"></tspan>\n</text>\n</g>
  Visible = true
  X = 10
  Y = 10
FEATURE [Drawing::FeatureViewAnnotation] Annotation009
  Font = Sans
  Rotation = 0
  Scale = 5
  Text = Robot 0.3 Reduced size of tooth on big gear and added boss. Rotated 180
  ViewResult = <g transform="translate(10,50) rotate(0)">\n<text id="Annotation009"\n font-family="Sans"\n font-size="5"\n fill="#000000">\n<tspan x="0" dy="1em">Robot 0.3 Reduced size of tooth on big gear and added boss. Rotated 180</tspan>\n<tspan x="0" dy="1em"></tspan>\n<tspan x="0" dy="1em"></tspan>\n</text>\n</g>
  Visible = true
  X = 10
  Y = 50
FEATURE [Part::Feature] Fusion103010
  Placement = pos=(0,0,0) rot=(0,0,-1;1.5708rad)
  shape: bbox 21.7 x 6.7 x 10.95 mm, 18 faces, 2 solids (baked)
FEATURE [Part::Feature] Fusion103011
  Placement = pos=(0,0,0) rot=(0,0,1;3.14159rad)
  shape: bbox 6.7 x 21.7 x 10.95 mm, 18 faces, 2 solids (baked)
FEATURE [Part::Feature] Fusion103012
  Placement = pos=(0,0,0) rot=(0,0,1;1.5708rad)
  shape: bbox 21.7 x 6.7 x 10.95 mm, 18 faces, 2 solids (baked)
FEATURE [Part::Box] Box270  label="Square Nut Hole 025"
  AttacherType = Attacher::AttachEngine3D
  Height = 2
  Length = 5.8
  Placement = pos=(-2.9,2.9,2.1) rot=(1,0,0;3.14159rad)
  Width = 5.8
FEATURE [Part::Cylinder] Cylinder042
  Angle = 360
  AttacherType = Attacher::AttachEngine3D
  Height = 10
  Placement = pos=(0,0,6.7) rot=(1,0,0;3.14159rad)
  Radius = 1.7
FEATURE [Part::Box] Box271  label="Cube228"
  AttacherType = Attacher::AttachEngine3D
  Height = 5
  Length = 40
  Placement = pos=(-20,-20,-2) rot=(0,0,1;0rad)
  Width = 40
FEATURE [Part::Sphere] Sphere089
  Angle1 = -90
  Angle2 = 90
  Angle3 = 360
  AttacherType = Attacher::AttachEngine3D
  Placement = pos=(0,0,4.3) rot=(1,0,0;3.14159rad)
  Radius = 3.35
FEATURE [Part::Box] Box272  label="Cube229"
  AttacherType = Attacher::AttachEngine3D
  Height = 15
  Length = 19.5
  Placement = pos=(-9.75,-9.75,-14) rot=(0,0,1;0rad)
  Width = 19.5
FEATURE [Part::Box] Box273  label="Cube230"
  AttacherType = Attacher::AttachEngine3D
  Height = 15
  Length = 19.5
  Placement = pos=(-9.75,-9.75,-3) rot=(0,0,1;0rad)
  Width = 19.5
FEATURE [Part::Chamfer] Chamfer015  label="Octagon001"
  Base = -> Box273
  Edges = 4 edges r=4: [Edge1,Edge3,Edge5,Edge7]
FEATURE [Part::Box] Box274  label="Cube231"
  AttacherType = Attacher::AttachEngine3D
  Height = 10
  Length = 24
  Placement = pos=(-12,-12,2.1) rot=(0,0,1;0rad)
  Width = 24
FEATURE [Part::Box] Box275  label="Cube232"
  AttacherType = Attacher::AttachEngine3D
  Height = 14
  Length = 20
  Placement = pos=(-10,-10,0) rot=(0,0,1;0rad)
  Width = 20
FEATURE [Part::Cut] Cut116
  Base = -> Box274
  Tool = -> Box275
FEATURE [Part::Chamfer] Chamfer016  label="Glue Channel001"
  Base = -> Cut116
  Edges = 8 edges r=0.95: [Edge4,Edge5,Edge14,Edge16,Edge17,Edge18,Edge19,Edge20]
FEATURE [Part::Box] Box276  label="Cube233"
  AttacherType = Attacher::AttachEngine3D
  Height = 7
  Length = 5
  Placement = pos=(-5,0,-2) rot=(0,0,1;0rad)
  Width = 40
FEATURE [Part::Box] Box277  label="Cube234"
  AttacherType = Attacher::AttachEngine3D
  Height = 7
  Length = 10
  Placement = pos=(-15,6,-2) rot=(0,0,1;0rad)
  Width = 2
FEATURE [Part::Box] Box278  label="Cube235"
  AttacherType = Attacher::AttachEngine3D
  Height = 7
  Length = 10
  Placement = pos=(-15,10,-2) rot=(0,0,1;0rad)
  Width = 2
FEATURE [Part::Box] Box279  label="Cube236"
  AttacherType = Attacher::AttachEngine3D
  Height = 7
  Length = 10
  Placement = pos=(-15,25.4,-2) rot=(0,0,1;0rad)
  Width = 2
FEATURE [Part::Box] Box280  label="Cube237"
  AttacherType = Attacher::AttachEngine3D
  Height = 7
  Length = 10
  Placement = pos=(-15,34.6,-2) rot=(0,0,1;0rad)
  Width = 2
FEATURE [Part::Sphere] Sphere090
  Angle1 = -90
  Angle2 = 90
  Angle3 = 360
  AttacherType = Attacher::AttachEngine3D
  Placement = pos=(-7.5,6.5,0.5) rot=(0,0,1;0rad)
  Radius = 1.25
FEATURE [Part::Box] Box281  label="Chamfer Cube009"
  AttacherType = Attacher::AttachEngine3D
  Height = 10
  Length = 13
  Placement = pos=(-11.69,0,-1.19) rot=(0,-1,0;0.785398rad)
  Width = 40
FEATURE [Part::Sphere] Sphere091
  Angle1 = -90
  Angle2 = 90
  Angle3 = 360
  AttacherType = Attacher::AttachEngine3D
  Placement = pos=(-7.5,11.5,0.5) rot=(0,0,1;0rad)
  Radius = 1.25
FEATURE [Part::Sphere] Sphere092
  Angle1 = -90
  Angle2 = 90
  Angle3 = 360
  AttacherType = Attacher::AttachEngine3D
  Placement = pos=(-7.5,28,0.5) rot=(0,0,1;0rad)
  Radius = 1.5
FEATURE [Part::Sphere] Sphere093
  Angle1 = -90
  Angle2 = 90
  Angle3 = 360
  AttacherType = Attacher::AttachEngine3D
  Placement = pos=(-7.5,34,0.5) rot=(0,0,1;0rad)
  Radius = 1.5
FEATURE [Part::Box] Box282  label="Cube238"
  AttacherType = Attacher::AttachEngine3D
  Height = 7
  Length = 4
  Placement = pos=(-6,5,-2) rot=(0,0,1;0rad)
  Width = 1
FEATURE [Part::Box] Box283  label="Cube239"
  AttacherType = Attacher::AttachEngine3D
  Height = 7
  Length = 4
  Placement = pos=(-6,8,-2) rot=(0,0,1;0rad)
  Width = 2
FEATURE [Part::Box] Box284  label="Cube240"
  AttacherType = Attacher::AttachEngine3D
  Height = 7
  Length = 4
  Placement = pos=(-6,12,-2) rot=(0,0,1;0rad)
  Width = 1
FEATURE [Part::Box] Box285  label="Cube241"
  AttacherType = Attacher::AttachEngine3D
  Height = 7
  Length = 4
  Placement = pos=(-6,24.4,-2) rot=(0,0,1;0rad)
  Width = 1
FEATURE [Part::Box] Box286  label="Cube242"
  AttacherType = Attacher::AttachEngine3D
  Height = 7
  Length = 4
  Placement = pos=(-6,36.6,-2) rot=(0,0,1;0rad)
  Width = 1
FEATURE [Part::Box] Box287  label="Cube243"
  AttacherType = Attacher::AttachEngine3D
  Height = 7
  Length = 4
  Placement = pos=(-6,27.4,-2) rot=(0,0,1;0rad)
  Width = 7.2
FEATURE [Part::MultiFuse] Fusion103013  label="Extra Holes for Clips009"
  Shapes = -> [Box287,Box284,Box286,Box283,Box285,Box282]
FEATURE [Part::Box] Box288  label="Re-level Edge Clip Block018"
  AttacherType = Attacher::AttachEngine3D
  Height = 10
  Length = 20
  Placement = pos=(-19,-2,3) rot=(0,0,1;0rad)
  Width = 44
FEATURE [Part::Box] Box289  label="Re-level Edge Clip Block019"
  AttacherType = Attacher::AttachEngine3D
  Height = 10
  Length = 12
  Placement = pos=(-21.5,-2,-7) rot=(0,0,1;0rad)
  Width = 44
FEATURE [Part::Fuse] Fusion103014  label="Bumps009"
  Base = -> Sphere090
  Tool = -> Sphere091
FEATURE [Part::Fuse] Fusion103015  label="Holes009"
  Base = -> Sphere092
  Tool = -> Sphere093
FEATURE [Part::MultiFuse] Fusion103016
  Shapes = -> [Box276,Box277,Box278,Box279,Box280]
FEATURE [Part::Fuse] Fusion103017
  Base = -> Fusion103014
  Tool = -> Fusion103016
FEATURE [Part::Cut] Cut117
  Base = -> Fusion103017
  Tool = -> Fusion103015
FEATURE [Part::Cut] Cut118
  Base = -> Cut117
  Tool = -> Fusion103013
FEATURE [Part::Cut] Cut119
  Base = -> Cut118
  Tool = -> Box288
FEATURE [Part::Cut] Cut120
  Base = -> Cut119
  Tool = -> Box289
FEATURE [Part::Cut] Cut121  label="Edge Clips Master002"
  Base = -> Cut120
  Placement = pos=(-20,-20,0) rot=(0,0,1;0rad)
  Tool = -> Box281
FEATURE [Part::Box] Box290  label="Cube244"
  AttacherType = Attacher::AttachEngine3D
  Height = 7
  Length = 5
  Placement = pos=(-5,0,-2) rot=(0,0,1;0rad)
  Width = 40
FEATURE [Part::Box] Box291  label="Cube245"
  AttacherType = Attacher::AttachEngine3D
  Height = 7
  Length = 4
  Placement = pos=(-6,8,-2) rot=(0,0,1;0rad)
  Width = 2
FEATURE [Part::Box] Box292  label="Chamfer Cube010"
  AttacherType = Attacher::AttachEngine3D
  Height = 10
  Length = 13
  Placement = pos=(-11.69,0,-1.19) rot=(0,-1,0;0.785398rad)
  Width = 40
FEATURE [Part::Box] Box293  label="Cube246"
  AttacherType = Attacher::AttachEngine3D
  Height = 7
  Length = 10
  Placement = pos=(-15,6,-2) rot=(0,0,1;0rad)
  Width = 2
FEATURE [Part::Sphere] Sphere094
  Angle1 = -90
  Angle2 = 90
  Angle3 = 360
  AttacherType = Attacher::AttachEngine3D
  Placement = pos=(-7.5,11.5,0.5) rot=(0,0,1;0rad)
  Radius = 1.25
FEATURE [Part::Box] Box294  label="Cube247"
  AttacherType = Attacher::AttachEngine3D
  Height = 7
  Length = 4
  Placement = pos=(-6,27.4,-2) rot=(0,0,1;0rad)
  Width = 7.2
FEATURE [Part::Box] Box295  label="Cube248"
  AttacherType = Attacher::AttachEngine3D
  Height = 7
  Length = 4
  Placement = pos=(-6,12,-2) rot=(0,0,1;0rad)
  Width = 1
FEATURE [Part::Box] Box296  label="Cube249"
  AttacherType = Attacher::AttachEngine3D
  Height = 7
  Length = 4
  Placement = pos=(-6,24.4,-2) rot=(0,0,1;0rad)
  Width = 1
FEATURE [Part::Sphere] Sphere095
  Angle1 = -90
  Angle2 = 90
  Angle3 = 360
  AttacherType = Attacher::AttachEngine3D
  Placement = pos=(-7.5,6.5,0.5) rot=(0,0,1;0rad)
  Radius = 1.25
FEATURE [Part::Box] Box297  label="Cube250"
  AttacherType = Attacher::AttachEngine3D
  Height = 7
  Length = 4
  Placement = pos=(-6,36.6,-2) rot=(0,0,1;0rad)
  Width = 1
FEATURE [Part::Box] Box298  label="Cube251"
  AttacherType = Attacher::AttachEngine3D
  Height = 7
  Length = 10
  Placement = pos=(-15,10,-2) rot=(0,0,1;0rad)
  Width = 2
FEATURE [Part::Sphere] Sphere096
  Angle1 = -90
  Angle2 = 90
  Angle3 = 360
  AttacherType = Attacher::AttachEngine3D
  Placement = pos=(-7.5,34,0.5) rot=(0,0,1;0rad)
  Radius = 1.5
FEATURE [Part::Box] Box299  label="Cube252"
  AttacherType = Attacher::AttachEngine3D
  Height = 7
  Length = 4
  Placement = pos=(-6,5,-2) rot=(0,0,1;0rad)
  Width = 1
FEATURE [Part::MultiFuse] Fusion103019  label="Extra Holes for Clips010"
  Shapes = -> [Box294,Box295,Box297,Box291,Box296,Box299]
FEATURE [Part::Box] Box300  label="Re-level Edge Clip Block020"
  AttacherType = Attacher::AttachEngine3D
  Height = 10
  Length = 20
  Placement = pos=(-19,-2,3) rot=(0,0,1;0rad)
  Width = 44
FEATURE [Part::Box] Box301  label="Cube253"
  AttacherType = Attacher::AttachEngine3D
  Height = 7
  Length = 10
  Placement = pos=(-15,34.6,-2) rot=(0,0,1;0rad)
  Width = 2
FEATURE [Part::Box] Box302  label="Cube254"
  AttacherType = Attacher::AttachEngine3D
  Height = 7
  Length = 10
  Placement = pos=(-15,25.4,-2) rot=(0,0,1;0rad)
  Width = 2
FEATURE [Part::MultiFuse] Fusion103020
  Shapes = -> [Box290,Box293,Box298,Box302,Box301]
FEATURE [Part::Fuse] Fusion103021  label="Bumps010"
  Base = -> Sphere095
  Tool = -> Sphere094
FEATURE [Part::Fuse] Fusion103018
  Base = -> Fusion103021
  Tool = -> Fusion103020
FEATURE [Part::Sphere] Sphere097
  Angle1 = -90
  Angle2 = 90
  Angle3 = 360
  AttacherType = Attacher::AttachEngine3D
  Placement = pos=(-7.5,28,0.5) rot=(0,0,1;0rad)
  Radius = 1.5
FEATURE [Part::Fuse] Fusion103022  label="Holes010"
  Base = -> Sphere097
  Tool = -> Sphere096
FEATURE [Part::Box] Box303  label="Re-level Edge Clip Block021"
  AttacherType = Attacher::AttachEngine3D
  Height = 10
  Length = 12
  Placement = pos=(-21.5,-2,-7) rot=(0,0,1;0rad)
  Width = 44
FEATURE [Part::Cut] Cut122
  Base = -> Fusion103018
  Tool = -> Fusion103022
FEATURE [Part::Cut] Cut123
  Base = -> Cut122
  Tool = -> Fusion103019
FEATURE [Part::Cut] Cut124
  Base = -> Cut123
  Tool = -> Box300
FEATURE [Part::Cut] Cut125
  Base = -> Cut124
  Tool = -> Box303
FEATURE [Part::Cut] Cut126  label="Edge Clips007"
  Base = -> Cut125
  Placement = pos=(20,-20,0) rot=(0,0,1;1.5708rad)
  Tool = -> Box292
FEATURE [Part::Box] Box304  label="Re-level Edge Clip Block022"
  AttacherType = Attacher::AttachEngine3D
  Height = 10
  Length = 12
  Placement = pos=(-21.5,-2,-7) rot=(0,0,1;0rad)
  Width = 44
FEATURE [Part::Box] Box305  label="Cube255"
  AttacherType = Attacher::AttachEngine3D
  Height = 7
  Length = 4
  Placement = pos=(-6,36.6,-2) rot=(0,0,1;0rad)
  Width = 1
FEATURE [Part::Box] Box306  label="Cube256"
  AttacherType = Attacher::AttachEngine3D
  Height = 7
  Length = 10
  Placement = pos=(-15,10,-2) rot=(0,0,1;0rad)
  Width = 2
FEATURE [Part::Box] Box307  label="Cube257"
  AttacherType = Attacher::AttachEngine3D
  Height = 7
  Length = 10
  Placement = pos=(-15,25.4,-2) rot=(0,0,1;0rad)
  Width = 2
FEATURE [Part::Box] Box308  label="Re-level Edge Clip Block023"
  AttacherType = Attacher::AttachEngine3D
  Height = 10
  Length = 20
  Placement = pos=(-19,-2,3) rot=(0,0,1;0rad)
  Width = 44
FEATURE [Part::Box] Box309  label="Cube258"
  AttacherType = Attacher::AttachEngine3D
  Height = 7
  Length = 10
  Placement = pos=(-15,34.6,-2) rot=(0,0,1;0rad)
  Width = 2
FEATURE [Part::Sphere] Sphere098
  Angle1 = -90
  Angle2 = 90
  Angle3 = 360
  AttacherType = Attacher::AttachEngine3D
  Placement = pos=(-7.5,34,0.5) rot=(0,0,1;0rad)
  Radius = 1.5
FEATURE [Part::Sphere] Sphere099
  Angle1 = -90
  Angle2 = 90
  Angle3 = 360
  AttacherType = Attacher::AttachEngine3D
  Placement = pos=(-7.5,28,0.5) rot=(0,0,1;0rad)
  Radius = 1.5
FEATURE [Part::Fuse] Fusion103023  label="Holes011"
  Base = -> Sphere099
  Tool = -> Sphere098
FEATURE [Part::Box] Box310  label="Cube259"
  AttacherType = Attacher::AttachEngine3D
  Height = 7
  Length = 4
  Placement = pos=(-6,5,-2) rot=(0,0,1;0rad)
  Width = 1
FEATURE [Part::Box] Box311  label="Cube260"
  AttacherType = Attacher::AttachEngine3D
  Height = 7
  Length = 4
  Placement = pos=(-6,24.4,-2) rot=(0,0,1;0rad)
  Width = 1
FEATURE [Part::Sphere] Sphere100
  Angle1 = -90
  Angle2 = 90
  Angle3 = 360
  AttacherType = Attacher::AttachEngine3D
  Placement = pos=(-7.5,11.5,0.5) rot=(0,0,1;0rad)
  Radius = 1.25
FEATURE [Part::Box] Box312  label="Cube261"
  AttacherType = Attacher::AttachEngine3D
  Height = 7
  Length = 4
  Placement = pos=(-6,12,-2) rot=(0,0,1;0rad)
  Width = 1
FEATURE [Part::Box] Box313  label="Chamfer Cube011"
  AttacherType = Attacher::AttachEngine3D
  Height = 10
  Length = 13
  Placement = pos=(-11.69,0,-1.19) rot=(0,-1,0;0.785398rad)
  Width = 40
FEATURE [Part::Sphere] Sphere101
  Angle1 = -90
  Angle2 = 90
  Angle3 = 360
  AttacherType = Attacher::AttachEngine3D
  Placement = pos=(-7.5,6.5,0.5) rot=(0,0,1;0rad)
  Radius = 1.25
FEATURE [Part::Fuse] Fusion103024  label="Bumps011"
  Base = -> Sphere101
  Tool = -> Sphere100
FEATURE [Part::Box] Box314  label="Cube262"
  AttacherType = Attacher::AttachEngine3D
  Height = 7
  Length = 5
  Placement = pos=(-5,0,-2) rot=(0,0,1;0rad)
  Width = 40
FEATURE [Part::Box] Box315  label="Cube263"
  AttacherType = Attacher::AttachEngine3D
  Height = 7
  Length = 4
  Placement = pos=(-6,27.4,-2) rot=(0,0,1;0rad)
  Width = 7.2
FEATURE [Part::Box] Box316  label="Cube264"
  AttacherType = Attacher::AttachEngine3D
  Height = 7
  Length = 4
  Placement = pos=(-6,8,-2) rot=(0,0,1;0rad)
  Width = 2
FEATURE [Part::MultiFuse] Fusion103025  label="Extra Holes for Clips011"
  Shapes = -> [Box315,Box312,Box305,Box316,Box311,Box310]
FEATURE [Part::Box] Box317  label="Cube265"
  AttacherType = Attacher::AttachEngine3D
  Height = 7
  Length = 10
  Placement = pos=(-15,6,-2) rot=(0,0,1;0rad)
  Width = 2
FEATURE [Part::MultiFuse] Fusion103026
  Shapes = -> [Box314,Box317,Box306,Box307,Box309]
FEATURE [Part::Fuse] Fusion103027
  Base = -> Fusion103024
  Tool = -> Fusion103026
FEATURE [Part::Cut] Cut128
  Base = -> Fusion103027
  Tool = -> Fusion103023
FEATURE [Part::Cut] Cut114
  Base = -> Cut128
  Tool = -> Fusion103025
FEATURE [Part::Cut] Cut129
  Base = -> Cut114
  Tool = -> Box308
FEATURE [Part::Cut] Cut115
  Base = -> Cut129
  Tool = -> Box304
FEATURE [Part::Cut] Cut127  label="Edge Clips008"
  Base = -> Cut115
  Placement = pos=(20,20,0) rot=(0,0,1;3.14159rad)
  Tool = -> Box313
FEATURE [Part::Box] Box318  label="Re-level Edge Clip Block024"
  AttacherType = Attacher::AttachEngine3D
  Height = 10
  Length = 12
  Placement = pos=(-21.5,-2,-7) rot=(0,0,1;0rad)
  Width = 44
FEATURE [Part::Box] Box319  label="Cube266"
  AttacherType = Attacher::AttachEngine3D
  Height = 7
  Length = 10
  Placement = pos=(-15,10,-2) rot=(0,0,1;0rad)
  Width = 2
FEATURE [Part::Box] Box320  label="Cube267"
  AttacherType = Attacher::AttachEngine3D
  Height = 7
  Length = 4
  Placement = pos=(-6,12,-2) rot=(0,0,1;0rad)
  Width = 1
FEATURE [Part::Box] Box321  label="Chamfer Cube012"
  AttacherType = Attacher::AttachEngine3D
  Height = 10
  Length = 13
  Placement = pos=(-11.69,0,-1.19) rot=(0,-1,0;0.785398rad)
  Width = 40
FEATURE [Part::Sphere] Sphere102
  Angle1 = -90
  Angle2 = 90
  Angle3 = 360
  AttacherType = Attacher::AttachEngine3D
  Placement = pos=(-7.5,6.5,0.5) rot=(0,0,1;0rad)
  Radius = 1.25
FEATURE [Part::Box] Box322  label="Cube268"
  AttacherType = Attacher::AttachEngine3D
  Height = 7
  Length = 5
  Placement = pos=(-5,0,-2) rot=(0,0,1;0rad)
  Width = 40
FEATURE [Part::Box] Box323  label="Cube269"
  AttacherType = Attacher::AttachEngine3D
  Height = 7
  Length = 4
  Placement = pos=(-6,27.4,-2) rot=(0,0,1;0rad)
  Width = 7.2
FEATURE [Part::Box] Box324  label="Cube270"
  AttacherType = Attacher::AttachEngine3D
  Height = 7
  Length = 4
  Placement = pos=(-6,8,-2) rot=(0,0,1;0rad)
  Width = 2
FEATURE [Part::Box] Box325  label="Cube271"
  AttacherType = Attacher::AttachEngine3D
  Height = 7
  Length = 10
  Placement = pos=(-15,6,-2) rot=(0,0,1;0rad)
  Width = 2
FEATURE [Part::Sphere] Sphere103
  Angle1 = -90
  Angle2 = 90
  Angle3 = 360
  AttacherType = Attacher::AttachEngine3D
  Placement = pos=(-7.5,28,0.5) rot=(0,0,1;0rad)
  Radius = 1.5
FEATURE [Part::Box] Box326  label="Cube272"
  AttacherType = Attacher::AttachEngine3D
  Height = 7
  Length = 4
  Placement = pos=(-6,5,-2) rot=(0,0,1;0rad)
  Width = 1
FEATURE [Part::Box] Box327  label="Cube273"
  AttacherType = Attacher::AttachEngine3D
  Height = 7
  Length = 4
  Placement = pos=(-6,24.4,-2) rot=(0,0,1;0rad)
  Width = 1
FEATURE [Part::Sphere] Sphere104
  Angle1 = -90
  Angle2 = 90
  Angle3 = 360
  AttacherType = Attacher::AttachEngine3D
  Placement = pos=(-7.5,11.5,0.5) rot=(0,0,1;0rad)
  Radius = 1.25
FEATURE [Part::Box] Box328  label="Re-level Edge Clip Block025"
  AttacherType = Attacher::AttachEngine3D
  Height = 10
  Length = 20
  Placement = pos=(-19,-2,3) rot=(0,0,1;0rad)
  Width = 44
FEATURE [Part::Box] Box329  label="Cube274"
  AttacherType = Attacher::AttachEngine3D
  Height = 7
  Length = 10
  Placement = pos=(-15,34.6,-2) rot=(0,0,1;0rad)
  Width = 2
FEATURE [Part::Box] Box330  label="Cube275"
  AttacherType = Attacher::AttachEngine3D
  Height = 7
  Length = 10
  Placement = pos=(-15,25.4,-2) rot=(0,0,1;0rad)
  Width = 2
FEATURE [Part::MultiFuse] Fusion103030
  Shapes = -> [Box322,Box325,Box319,Box330,Box329]
FEATURE [Part::Box] Box331  label="Cube276"
  AttacherType = Attacher::AttachEngine3D
  Height = 7
  Length = 4
  Placement = pos=(-6,36.6,-2) rot=(0,0,1;0rad)
  Width = 1
FEATURE [Part::MultiFuse] Fusion103029  label="Extra Holes for Clips012"
  Shapes = -> [Box323,Box320,Box331,Box324,Box327,Box326]
FEATURE [Part::Fuse] Fusion103032  label="Bumps012"
  Base = -> Sphere102
  Tool = -> Sphere104
FEATURE [Part::Fuse] Fusion103028
  Base = -> Fusion103032
  Tool = -> Fusion103030
FEATURE [Part::Sphere] Sphere105
  Angle1 = -90
  Angle2 = 90
  Angle3 = 360
  AttacherType = Attacher::AttachEngine3D
  Placement = pos=(-7.5,34,0.5) rot=(0,0,1;0rad)
  Radius = 1.5
FEATURE [Part::Fuse] Fusion103031  label="Holes012"
  Base = -> Sphere103
  Tool = -> Sphere105
FEATURE [Part::Cut] Cut134
  Base = -> Fusion103028
  Tool = -> Fusion103031
FEATURE [Part::Cut] Cut130
  Base = -> Cut134
  Tool = -> Fusion103029
FEATURE [Part::Cut] Cut131
  Base = -> Cut130
  Tool = -> Box328
FEATURE [Part::Cut] Cut132
  Base = -> Cut131
  Tool = -> Box318
FEATURE [Part::Cut] Cut133  label="Edge Clips009"
  Base = -> Cut132
  Placement = pos=(-20,20,0) rot=(0,0,-1;1.5708rad)
  Tool = -> Box321
FEATURE [Part::Box] Box332  label="Cube277"
  AttacherType = Attacher::AttachEngine3D
  Height = 10
  Length = 10
  Placement = pos=(4,-26,1) rot=(0.205904,-0.974848,-0.085288;0.803573rad)
  Width = 15
FEATURE [Part::Box] Box333  label="Cube278"
  AttacherType = Attacher::AttachEngine3D
  Height = 10
  Length = 10
  Placement = pos=(-26,-4,1) rot=(-0.273007,-0.419215,-0.865867;1.78566rad)
  Width = 15
FEATURE [Part::Box] Box334  label="Cube279"
  AttacherType = Attacher::AttachEngine3D
  Height = 10
  Length = 10
  Placement = pos=(-4,26,1) rot=(0.381439,0.080566,0.920876;3.07487rad)
  Width = 15
FEATURE [Part::Box] Box335  label="Cube280"
  AttacherType = Attacher::AttachEngine3D
  Height = 10
  Length = 10
  Placement = pos=(26,4,1) rot=(0.442189,-0.287968,0.849437;1.66134rad)
  Width = 15
FEATURE [Part::MultiFuse] Fusion103033  label="Glue Dents002"
  Shapes = -> [Box332,Box333,Box334,Box335]
FEATURE [Part::MultiFuse] Fusion103034  label="Edge Clips Fusion002"
  Shapes = -> [Cut133,Cut121,Cut126,Cut127]
FEATURE [Part::MultiFuse] Fusion103035
  Placement = pos=(-15,-15,0) rot=(0,0,1;0rad)
  Shapes = -> [Box270,Cylinder042,Sphere089]
FEATURE [Part::Box] Box336  label="Square Nut Hole 026"
  AttacherType = Attacher::AttachEngine3D
  Height = 2
  Length = 5.8
  Placement = pos=(-2.9,2.9,2.1) rot=(1,0,0;3.14159rad)
  Width = 5.8
FEATURE [Part::Cylinder] Cylinder043
  Angle = 360
  AttacherType = Attacher::AttachEngine3D
  Height = 10
  Placement = pos=(0,0,6.7) rot=(1,0,0;3.14159rad)
  Radius = 1.7
FEATURE [Part::Sphere] Sphere106
  Angle1 = -90
  Angle2 = 90
  Angle3 = 360
  AttacherType = Attacher::AttachEngine3D
  Placement = pos=(0,0,4.3) rot=(1,0,0;3.14159rad)
  Radius = 3.35
FEATURE [Part::MultiFuse] Fusion103036
  Placement = pos=(-15,0,0) rot=(0,0,1;0rad)
  Shapes = -> [Box336,Cylinder043,Sphere106]
FEATURE [Part::Fuse] Fusion103037
  Base = -> Fusion103035
  Tool = -> Fusion103036
FEATURE [Part::MultiFuse] Fusion103038  label="Nut Holes001"
  Shapes = -> [Fusion103037,Fusion103012,Fusion103011,Fusion103010]
FEATURE [Part::Fuse] Fusion103039  label="Cube with Edge Clips001"
  Base = -> Box271
  Tool = -> Fusion103034
FEATURE [Part::Cut] Cut135
  Base = -> Fusion103039
  Tool = -> Fusion103033
FEATURE [Part::Cut] Cut136
  Base = -> Cut135
  Tool = -> Fusion103038
FEATURE [Part::Cut] Cut137
  Base = -> Cut136
  Tool = -> Chamfer016
FEATURE [Part::Cut] Cut138
  Base = -> Cut137
  Tool = -> Chamfer015
FEATURE [Part::Cut] Cut139  label="Nut Plate 1.003"
  Base = -> Cut138
  Tool = -> Box272
FEATURE [Part::Cylinder] Cylinder044
  Angle = 360
  AttacherType = Attacher::AttachEngine3D
  Height = 4
  Placement = pos=(-9.75,-9.75,-3) rot=(0,0,1;0rad)
  Radius = 1.5
FEATURE [Part::Cylinder] Cylinder045
  Angle = 360
  AttacherType = Attacher::AttachEngine3D
  Height = 4
  Placement = pos=(9.75,-9.75,-3) rot=(0,0,1;0rad)
  Radius = 1.5
FEATURE [Part::Cylinder] Cylinder046
  Angle = 360
  AttacherType = Attacher::AttachEngine3D
  Height = 4
  Placement = pos=(-9.75,9.75,-3) rot=(0,0,1;0rad)
  Radius = 1.5
FEATURE [Part::Cylinder] Cylinder047
  Angle = 360
  AttacherType = Attacher::AttachEngine3D
  Height = 4
  Placement = pos=(9.75,9.75,-3) rot=(0,0,1;0rad)
  Radius = 1.5
FEATURE [Part::MultiFuse] Fusion103040
  Shapes = -> [Cylinder044,Cylinder047,Cylinder045,Cylinder046]
FEATURE [Part::Cut] Cut140  label="Nut Plate 1.004"
  Base = -> Cut139
  Placement = pos=(0,0,-6) rot=(0,0,1;0rad)
  Tool = -> Fusion103040
FEATURE [App::DocumentObjectGroup] Group003  label="Cube-components"
  Group = -> [Cut112,Cut113]
FEATURE [Part::Box] Box404  label="Cube334"
  AttacherType = Attacher::AttachEngine3D
  Height = 14
  Length = 5
  Placement = pos=(20,20,-7) rot=(0,0,1;0rad)
  Width = 5
FEATURE [Part::Box] Box405  label="Cube335"
  AttacherType = Attacher::AttachEngine3D
  Height = 13
  Length = 15
  Placement = pos=(10,10,2) rot=(0,0,1;0rad)
  Width = 15
FEATURE [Part::FeaturePython] BevelGear001  # WARN: FeaturePython — macro-defined, semantics opaque (R4)
  Placement = pos=(7.81,7.81,10.5) rot=(0.862856,-0.357407,-0.357407;1.71775rad)
  backlash = 0
  beta = 0
  clearance = 0.1
  height = 3
  m = 1
  numpoints = 6
  pitch_angle = 30
  pressure_angle = 20
  reset_origin = true
  teeth = 10
FEATURE [Part::Cylinder] Cylinder054
  Angle = 360
  AttacherType = Attacher::AttachEngine3D
  Height = 22
  Radius = 11
FEATURE [Part::Cone] Cone
  Angle = 360
  AttacherType = Attacher::AttachEngine3D
  Height = 9
  Placement = pos=(8.52,8.52,10.5) rot=(0.862856,-0.357407,-0.357407;1.71777rad)
  Radius1 = 8
  Radius2 = 1.5
FEATURE [Part::Box] Box406004  label="Square Nut Hole 029"
  AttacherType = Attacher::AttachEngine3D
  Height = 2
  Length = 5.8
  Placement = pos=(15.7,19.8,5.1) rot=(0.862856,-0.357407,-0.357407;1.71777rad)
  Width = 14.8
FEATURE [Part::Box] Box406005  label="60mm-high"
  AttacherType = Attacher::AttachEngine3D
  Height = 60
  Length = 10
  Placement = pos=(-29,12,-3) rot=(0,0,1;0rad)
  Width = 10
FEATURE [Part::Cylinder] Cylinder057  label="small-gear-hub"
  Angle = 360
  AttacherType = Attacher::AttachEngine3D
  Height = 3
  Placement = pos=(7.5,7.5,10.5) rot=(0.862856,-0.357407,-0.357407;1.71777rad)
  Radius = 3.9
FEATURE [Part::Feature] Shape001  label="M3-hex-cavity"
  Placement = pos=(-0.5,-0.5,10.5) rot=(0.281085,0.678598,0.678598;2.59356rad)
  shape: bbox 11.56 x 11.56 x 5.5 mm, 8 faces (baked)
FEATURE [Part::Cylinder] Cylinder058  label="M3-screw-drive001"
  Angle = 360
  AttacherType = Attacher::AttachEngine3D
  Height = 33
  Placement = pos=(23.37,23.37,10.5) rot=(0.862856,-0.357407,-0.357407;1.71777rad)
  Radius = 1.75
FEATURE [Part::Box] Box406007  label="Cube338"
  AttacherType = Attacher::AttachEngine3D
  Height = 14
  Length = 14
  Placement = pos=(1.78,11.68,2) rot=(0,0,-1;0.785398rad)
  Width = 10
FEATURE [Part::Box] Box406008  label="slot-1"
  AttacherType = Attacher::AttachEngine3D
  Height = 36
  Length = 10.5
  Placement = pos=(10.22,17.65,0) rot=(0,0,-1;0.785398rad)
  Width = 28
FEATURE [Part::Cylinder] Cylinder059  label="M3-screw-drive002"
  Angle = 360
  AttacherType = Attacher::AttachEngine3D
  Height = 80
  Placement = pos=(26.8701,26.8701,8) rot=(0.862856,-0.357407,-0.357407;1.71777rad)
  Radius = 2.15
FEATURE [Part::Cylinder] Cylinder066  label="M3-screw-drive003"
  Angle = 360
  AttacherType = Attacher::AttachEngine3D
  Height = 33
  Placement = pos=(26.8701,26.8701,8) rot=(0.862856,-0.357407,-0.357407;1.71777rad)
  Radius = 1.75
FEATURE [Part::MultiFuse] Fusion103077010  label="finger-cavity"
  Shapes = -> [Cylinder066,Box406004]
FEATURE [Part::Box] Box406015  label="motor-clamp-0"
  AttacherType = Attacher::AttachEngine3D
  Height = 31
  Length = 53.28
  Placement = pos=(-13.8876,-23.7871,2) rot=(0,0,1;0.785398rad)
  Width = 14
FEATURE [Part::Box] Box406016  label="clamp-slot"
  AttacherType = Attacher::AttachEngine3D
  Height = 32
  Length = 49
  Placement = pos=(17.31,-15.9,17) rot=(0,0,1;2.35619rad)
  Width = 2
FEATURE [Part::Cylinder] Cylinder067
  Angle = 360
  AttacherType = Attacher::AttachEngine3D
  Height = 26
  Placement = pos=(0,0,20) rot=(0,0,1;0rad)
  Radius = 6.25
FEATURE [Part::Box] Box406017  label="gearbox001"
  AttacherType = Attacher::AttachEngine3D
  Height = 28
  Length = 16
  Placement = pos=(-8,-5.25,18) rot=(0,0,1;0rad)
  Width = 10.5
FEATURE [Part::MultiCommon] Common004  label="motor-hole"
  Placement = pos=(0,0,0) rot=(0,0,-1;0.785398rad)
  Shapes = -> [Cylinder067,Box406017]
FEATURE [Part::Cylinder] Cylinder068
  Angle = 360
  AttacherType = Attacher::AttachEngine3D
  Height = 12
  Placement = pos=(0,0,40) rot=(0.281085,0.678598,0.678598;2.59356rad)
  Radius = 1.2
FEATURE [Part::Cylinder] Cylinder069
  Angle = 360
  AttacherType = Attacher::AttachEngine3D
  Height = 12
  Placement = pos=(8.48528,8.48528,40) rot=(0.281085,0.678598,0.678598;2.59356rad)
  Radius = 2.2
FEATURE [Part::MultiFuse] Fusion103077013  label="M2-screw001"
  Placement = pos=(2,-14,0) rot=(0,0,1;0rad)
  Shapes = -> [Cylinder068,Cylinder069]
FEATURE [Part::Feature] Fusion103077013001
  Placement = pos=(-2e-15,-13,30) rot=(-0.281085,0.678598,0.678598;3.68962rad)
  shape: bbox 19.37 x 19.37 x 4.4 mm, 5 faces (baked)
FEATURE [Part::Cylinder] Cylinder070
  Angle = 360
  AttacherType = Attacher::AttachEngine3D
  Height = 12
  Placement = pos=(0,0,12) rot=(0,0,1;0rad)
  Radius = 2.2
FEATURE [Part::Cylinder] Cylinder071
  Angle = 360
  AttacherType = Attacher::AttachEngine3D
  Height = 12
  Radius = 1.2
FEATURE [Part::Cylinder] Cylinder072  label="M3-cap-screw-head"
  Angle = 360
  AttacherType = Attacher::AttachEngine3D
  Height = 10
  Placement = pos=(0,15,4) rot=(0,0,1;0rad)
  Radius = 3
FEATURE [Part::FeaturePython] BevelGear002  # WARN: FeaturePython — macro-defined, semantics opaque (R4)
  Placement = pos=(0,0,2.5) rot=(0,0,1;0rad)
  backlash = 0
  beta = 0
  clearance = 0.1
  height = 3
  m = 1
  numpoints = 6
  pitch_angle = 45
  pressure_angle = 20
  reset_origin = true
  teeth = 20
FEATURE [Part::MultiCommon] Common  label="big-gear-a"
  Shapes = -> [BevelGear002,Cylinder054]
FEATURE [Part::MultiCommon] Common005  label="small-gear-1"
  Shapes = -> [Cone,BevelGear001]
FEATURE [Part::MultiFuse] Fusion103077013004005  label="small-gear-2"
  Shapes = -> [Common005,Cylinder057]
FEATURE [Part::MultiFuse] Fusion103077013004006  label="small-gear-cavity"
  Shapes = -> [Cylinder058,Shape001]
FEATURE [Part::Cut] Cut173011005  label="small-gear 0.4"
  Base = -> Fusion103077013004005
  Tool = -> Fusion103077013004006
FEATURE [Part::Cylinder] Cylinder073  label="motor-bulge"
  Angle = 360
  AttacherType = Attacher::AttachEngine3D
  Height = 20
  Placement = pos=(0,0,23) rot=(0,0,1;0rad)
  Radius = 9
FEATURE [Part::Cylinder] Cylinder074  label="big-gear-clearance"
  Angle = 360
  AttacherType = Attacher::AttachEngine3D
  Height = 22
  Radius = 12
FEATURE [Part::Cylinder] Cylinder075  label="M3-cap-screw-head001"
  Angle = 360
  AttacherType = Attacher::AttachEngine3D
  Height = 10
  Placement = pos=(0,15,-6) rot=(0,0,1;0rad)
  Radius = 1.7
FEATURE [Part::MultiFuse] Fusion103077013004011  label="M3-cap-screw"
  Placement = pos=(0,0,5) rot=(0,0,1;0rad)
  Shapes = -> [Cylinder075,Cylinder072]
FEATURE [Part::Box] Box406019  label="motor-clamp-print-45"
  AttacherType = Attacher::AttachEngine3D
  Height = 30
  Length = 16.46
  Placement = pos=(-19.23,2.77,22) rot=(0.707107,0.707107,0;1.5708rad)
  Width = 16.46
FEATURE [Part::Feature] Box406008001  label="slot-2"
  Placement = pos=(-10.22,-17.65,0) rot=(0,0,1;2.35619rad)
  shape: bbox 27.22 x 27.22 x 36 mm, 6 faces (baked)
FEATURE [Part::Box] Box406008002  label="Cube339"
  AttacherType = Attacher::AttachEngine3D
  Height = 24
  Length = 23
  Placement = pos=(-1.06066,-15.2,-2) rot=(0,0,1;0.785398rad)
  Width = 20
FEATURE [Part::MultiFuse] Fusion103077013004013  label="finger-slots"
  Shapes = -> [Box406008,Box406008001]
FEATURE [Part::Chamfer] Chamfer024  label="motor-clamp-1"
  Base = -> Box406015
  Edges = 2 edges r=12: [Edge2,Edge6]
FEATURE [Part::Chamfer] Chamfer025  label="motor-clamp-2"
  Base = -> Chamfer024
  Edges = 4 edges r=2: [Edge1,Edge4,Edge5,Edge14]
FEATURE [Part::MultiFuse] Fusion103077013004016  label="motor-clamp-3"
  Shapes = -> [Chamfer025,Cylinder073]
FEATURE [Part::Box] Box406008003  label="Cube340"
  AttacherType = Attacher::AttachEngine3D
  Height = 6
  Length = 15
  Placement = pos=(-5,10,2) rot=(0,0,1;0rad)
  Width = 10
FEATURE [Part::Cut] Cut173011007  label="screw-land-1"
  Base = -> Box406008003
  Tool = -> Cylinder074
FEATURE [Part::Cone] Cone001
  Angle = 360
  AttacherType = Attacher::AttachEngine3D
  Height = 9
  Placement = pos=(8.52,8.52,10.5) rot=(0.862856,-0.357407,-0.357407;1.71777rad)
  Radius1 = 9
  Radius2 = 2.5
FEATURE [Part::Box] Box406008004  label="gearbox004"
  AttacherType = Attacher::AttachEngine3D
  Height = 9
  Length = 12
  Placement = pos=(-6,-5,0) rot=(0,0,1;0rad)
  Width = 10
FEATURE [Part::Cylinder] Cylinder076  label="boss002"
  Angle = 360
  AttacherType = Attacher::AttachEngine3D
  Height = 1
  Placement = pos=(0,0,-1) rot=(0,0,1;0rad)
  Radius = 2
FEATURE [Part::Cylinder] Cylinder077
  Angle = 360
  AttacherType = Attacher::AttachEngine3D
  Height = 15
  Placement = pos=(0,0,9) rot=(0,0,1;0rad)
  Radius = 6
FEATURE [Part::Box] Box406008005  label="gearbox005"
  AttacherType = Attacher::AttachEngine3D
  Height = 27
  Length = 16
  Placement = pos=(-8,-5,0) rot=(0,0,1;0rad)
  Width = 10
FEATURE [Part::MultiCommon] Common001  label="motor002"
  Shapes = -> [Cylinder077,Box406008005]
FEATURE [Part::Cylinder] Cylinder078  label="shaft-002"
  Angle = 360
  AttacherType = Attacher::AttachEngine3D
  Height = 10
  Placement = pos=(0,0,-10) rot=(0,0,1;0rad)
  Radius = 1.5
FEATURE [Part::Box] Box406008006  label="Cube341"
  AttacherType = Attacher::AttachEngine3D
  Height = 12
  Length = 10
  Placement = pos=(-5,1,-11) rot=(0,0,1;0rad)
  Width = 10
FEATURE [Part::Cut] Cut001  label="shaft002"
  Base = -> Cylinder078
  Tool = -> Box406008006
FEATURE [Part::MultiFuse] Fusion103077013004017004  label="motor-assembled"
  Placement = pos=(0,0,20.5) rot=(0,0,-1;0.785398rad)
  Shapes = -> [Box406008004,Cylinder076,Common001,Cut001]
FEATURE [Part::Cylinder] Cylinder079  label="shaft-003"
  Angle = 360
  AttacherType = Attacher::AttachEngine3D
  Height = 10
  Placement = pos=(0,0,-2) rot=(0,0,1;0rad)
  Radius = 1.75
FEATURE [Part::Box] Box406008007  label="Cube342"
  AttacherType = Attacher::AttachEngine3D
  Height = 12
  Length = 10
  Placement = pos=(-5,1.125,-2) rot=(0,0,1;0rad)
  Width = 10
FEATURE [Part::Cut] Cut173011011  label="motor-shaft"
  Base = -> Cylinder079
  Tool = -> Box406008007
FEATURE [Part::Cut] Cut173011012  label="big-gear-2"
  Base = -> Common
  Tool = -> Cut173011011
FEATURE [Part::Box] Box406008008  label="Cube343"
  AttacherType = Attacher::AttachEngine3D
  Height = 2
  Length = 19
  Placement = pos=(-9.5,-9.5,0) rot=(0,0,1;0rad)
  Width = 19
FEATURE [Part::Cylinder] Cylinder080  label="Cylinder078"
  Angle = 360
  AttacherType = Attacher::AttachEngine3D
  Height = 10
  Placement = pos=(0,0,-4) rot=(0,0,1;0rad)
  Radius = 1.8
FEATURE [Part::Cut] Cut173011013  label="filler-plate-1"
  Base = -> Box406008008
  Tool = -> Cylinder080
FEATURE [Part::Chamfer] Chamfer026  label="filler-plate-2"
  Base = -> Cut173011013
  Edges = 1 edges r=0.5: [Edge10]
FEATURE [Part::Chamfer] Chamfer027  label="filler-plate"
  Base = -> Chamfer026
  Edges = 4 edges r=0.5: [Edge10,Edge11,Edge13,Edge15]
FEATURE [Part::Box] Box406008009  label="Cube344"
  AttacherType = Attacher::AttachEngine3D
  Height = 3
  Length = 6
  Placement = pos=(19,19,-7) rot=(0,0,1;0rad)
  Width = 6
FEATURE [Part::Chamfer] Chamfer029  label="grip-1"
  Base = -> Box406008009
  Edges = 2 edges r=1: [Edge2,Edge10]
FEATURE [Part::Chamfer] Chamfer030  label="grip-2"
  Base = -> Chamfer029
  Edges = 1 edges r=1: [Edge1]
FEATURE [Part::Cut] Cut173011016  label="mounting-plate"
  Base = -> Cut139
  Placement = pos=(0,0,0) rot=(1,0,0;3.14159rad)
  Tool = -> Fusion103040
FEATURE [Part::Chamfer] Chamfer032  label="Old big-gear 0.1"
  Base = -> Cut173011012
  Edges = 3 edges r=0.5: [Edge124,Edge125,Edge126]
FEATURE [Part::Feature] Shape002  label="M3-head-cover"
  Placement = pos=(5,5,10.5) rot=(0.862856,-0.357407,-0.357407;1.71777rad)
  shape: bbox 5.347 x 5.347 x 5.25 mm, 8 faces (baked)
FEATURE [Part::Cylinder] Cylinder081  label="M3-screw-drive004"
  Angle = 360
  AttacherType = Attacher::AttachEngine3D
  Height = 20
  Placement = pos=(23.4,23.4,10.5) rot=(0.862856,-0.357407,-0.357407;1.71777rad)
  Radius = 4.5
FEATURE [Part::Feature] Cylinder081001
  Placement = pos=(-23.4,-23.4,10.5) rot=(0.281085,0.678598,0.678598;2.59356rad)
  shape: bbox 20.51 x 20.51 x 9 mm, 3 faces (baked)
FEATURE [Part::MultiFuse] Fusion103077013004017006  label="nut-cavities"
  Shapes = -> [Cylinder081001,Cylinder081]
FEATURE [App::DocumentObjectGroup] Group001  label="Old"
  Group = -> [Cut008,Cut009,Cut015,Cut018,Fusion021,Fusion023,Group,Cut039,Cut028,Cut032,Cut033,Fusion048,Cylinder068,Cylinder069,Cylinder071,Cylinder070,Fusion103077013004017006]
FEATURE [Part::Chamfer] Chamfer  label="finger-1"
  Base = -> Box405
  Edges = 2 edges r=8.5: [Edge3,Edge5]
FEATURE [Part::Cut] Cut173011017  label="finger-2"
  Base = -> Chamfer
  Tool = -> Box406007
FEATURE [Part::Fillet] Fillet  label="finger-3"
  Base = -> Cut173011017
  Edges = 2 edges r=1.5: [Edge8,Edge14]
FEATURE [Part::Chamfer] Chamfer033  label="grip-3"
  Base = -> Chamfer030
  Edges = 3 edges r=1: [Edge4,Edge10,Edge15]
FEATURE [Part::MultiFuse] Fusion103077013004017007  label="finger-4"
  Shapes = -> [Chamfer033,Box404,Fillet]
FEATURE [Part::Fillet] Fillet006  label="finger-5"
  Base = -> Fusion103077013004017007
  Edges = 4 edges r=3: [Edge33,Edge41,Edge51,Edge59]
FEATURE [Part::Cut] Cut173011018  label="finger-6"
  Base = -> Fillet006
  Tool = -> Fusion103077010
FEATURE [Part::Chamfer] Chamfer034  label="finger-7"
  Base = -> Cut173011018
  Edges = 4 edges r=0.7: [Edge81,Edge82,Edge83,Edge84]
FEATURE [Part::Box] Box406008010  label="Cube345"
  AttacherType = Attacher::AttachEngine3D
  Height = 5
  Length = 10
  Placement = pos=(4,5,0.8) rot=(0,0,1;0.785398rad)
  Width = 1
FEATURE [Part::Box] Box406008011  label="Cube346"
  AttacherType = Attacher::AttachEngine3D
  Height = 5
  Length = 10
  Placement = pos=(7.3,5,0.8) rot=(0,0,1;0.785398rad)
  Width = 1
FEATURE [Part::Fuse] Fusion103077013004017008
  Base = -> Box406008010
  Tool = -> Box406008011
FEATURE [Part::Feature] Fusion103077013004017008001
  Placement = pos=(-4.36408,4.36408,2.00532) rot=(0.707107,0.707107,0;0.628319rad)
  shape: bbox 12.71 x 10.04 x 6.004 mm, 12 faces, 2 solids (baked)
FEATURE [Part::Feature] Fusion103077013004017008002
  Placement = pos=(-7.06123,7.06123,7.25532) rot=(0.707107,0.707107,0;1.25664rad)
  shape: bbox 12.81 x 11.79 x 4.715 mm, 12 faces, 2 solids (baked)
FEATURE [Part::Feature] Fusion103077013004017008003
  Placement = pos=(-7.06123,7.06123,13.7447) rot=(0.707107,0.707107,0;1.88496rad)
  shape: bbox 11.79 x 12.81 x 4.715 mm, 12 faces, 2 solids (baked)
FEATURE [Part::Feature] Fusion103077013004017008004
  Placement = pos=(-4.36408,4.36408,18.9947) rot=(0.707107,0.707107,0;2.51327rad)
  shape: bbox 10.04 x 12.71 x 6.004 mm, 12 faces, 2 solids (baked)
FEATURE [Part::Feature] Fusion103077013004017008005
  Placement = pos=(-1e-15,1e-15,21) rot=(0.707107,0.707107,0;3.14159rad)
  shape: bbox 7.778 x 11.08 x 5 mm, 12 faces, 2 solids (baked)
FEATURE [Part::Feature] Fusion103077013004017008006
  Placement = pos=(4.36408,-4.36408,18.9947) rot=(0.707107,0.707107,0;3.76991rad)
  shape: bbox 10.04 x 12.71 x 6.004 mm, 12 faces, 2 solids (baked)
FEATURE [Part::Feature] Fusion103077013004017008007
  Placement = pos=(7.06123,-7.06123,13.7447) rot=(-0.707107,-0.707107,0;1.88496rad)
  shape: bbox 11.79 x 12.81 x 4.715 mm, 12 faces, 2 solids (baked)
FEATURE [Part::Feature] Fusion103077013004017008008
  Placement = pos=(7.06123,-7.06123,7.25532) rot=(-0.707107,-0.707107,0;1.25664rad)
  shape: bbox 12.81 x 11.79 x 4.715 mm, 12 faces, 2 solids (baked)
FEATURE [Part::Feature] Fusion103077013004017008009
  Placement = pos=(4.36408,-4.36408,2.00532) rot=(-0.707107,-0.707107,0;0.628319rad)
  shape: bbox 12.71 x 10.04 x 6.004 mm, 12 faces, 2 solids (baked)
FEATURE [Part::MultiFuse] Fusion103077013004017008010  label="Cut away for small gear"
  Shapes = -> [Fusion103077013004017008001,Fusion103077013004017008003,Fusion103077013004017008007,Fusion103077013004017008005,Fusion103077013004017008009,Fusion103077013004017008008,Fusion103077013004017008004,Fusion103077013004017008002,Fusion103077013004017008,Fusion103077013004017008006]
FEATURE [Part::Box] Box406008012  label="Cube347"
  AttacherType = Attacher::AttachEngine3D
  Height = 10
  Length = 10
  Placement = pos=(12,0.6,0) rot=(0,-1,0;0.698132rad)
  Width = 1
FEATURE [Part::Box] Box406008013  label="Cube348"
  AttacherType = Attacher::AttachEngine3D
  Height = 10
  Length = 10
  Placement = pos=(12,-1.6,0) rot=(0,-1,0;0.698132rad)
  Width = 1
FEATURE [Part::MultiFuse] Fusion103077013004017008011  label="tooth-thin"
  Shapes = -> [Box406008012,Box406008013]
FEATURE [Part::Feature] Fusion103077013004017008011001
  Placement = pos=(0,0,0) rot=(0,0,1;0.314159rad)
  shape: bbox 14.39 x 7.397 x 14.09 mm, 12 faces, 2 solids (baked)
FEATURE [Part::Feature] Fusion103077013004017008011002
  Placement = pos=(0,0,0) rot=(0,0,1;0.628319rad)
  shape: bbox 13.28 x 10.87 x 14.09 mm, 12 faces, 2 solids (baked)
FEATURE [Part::Feature] Fusion103077013004017008011003
  Placement = pos=(0,0,0) rot=(0,0,1;0.942478rad)
  shape: bbox 10.87 x 13.28 x 14.09 mm, 12 faces, 2 solids (baked)
FEATURE [Part::Feature] Fusion103077013004017008011004
  Placement = pos=(0,0,0) rot=(0,0,1;1.25664rad)
  shape: bbox 7.397 x 14.39 x 14.09 mm, 12 faces, 2 solids (baked)
FEATURE [Part::Feature] Fusion103077013004017008011005
  Placement = pos=(0,0,0) rot=(0,0,1;1.5708rad)
  shape: bbox 3.2 x 14.09 x 14.09 mm, 12 faces, 2 solids (baked)
FEATURE [Part::Feature] Fusion103077013004017008011006
  Placement = pos=(0,0,0) rot=(0,0,1;1.88496rad)
  shape: bbox 7.397 x 14.39 x 14.09 mm, 12 faces, 2 solids (baked)
FEATURE [Part::Feature] Fusion103077013004017008011007
  Placement = pos=(0,0,0) rot=(0,0,1;2.19911rad)
  shape: bbox 10.87 x 13.28 x 14.09 mm, 12 faces, 2 solids (baked)
FEATURE [Part::Feature] Fusion103077013004017008011008
  Placement = pos=(0,0,0) rot=(0,0,1;2.51327rad)
  shape: bbox 13.28 x 10.87 x 14.09 mm, 12 faces, 2 solids (baked)
FEATURE [Part::Feature] Fusion103077013004017008011009
  Placement = pos=(0,0,0) rot=(0,0,1;2.82743rad)
  shape: bbox 14.39 x 7.397 x 14.09 mm, 12 faces, 2 solids (baked)
FEATURE [Part::Feature] Fusion103077013004017008011010
  Placement = pos=(0,0,0) rot=(0,0,1;3.14159rad)
  shape: bbox 14.09 x 3.2 x 14.09 mm, 12 faces, 2 solids (baked)
FEATURE [Part::Feature] Fusion103077013004017008011011
  Placement = pos=(0,0,0) rot=(0,0,1;3.45575rad)
  shape: bbox 14.39 x 7.397 x 14.09 mm, 12 faces, 2 solids (baked)
FEATURE [Part::Feature] Fusion103077013004017008011012
  Placement = pos=(0,0,0) rot=(0,0,1;3.76991rad)
  shape: bbox 13.28 x 10.87 x 14.09 mm, 12 faces, 2 solids (baked)
FEATURE [Part::Feature] Fusion103077013004017008011013
  Placement = pos=(0,0,0) rot=(0,0,1;4.08407rad)
  shape: bbox 10.87 x 13.28 x 14.09 mm, 12 faces, 2 solids (baked)
FEATURE [Part::Feature] Fusion103077013004017008011014
  Placement = pos=(0,0,0) rot=(0,0,-1;1.88496rad)
  shape: bbox 7.397 x 14.39 x 14.09 mm, 12 faces, 2 solids (baked)
FEATURE [Part::Feature] Fusion103077013004017008011015
  Placement = pos=(0,0,0) rot=(0,0,-1;1.5708rad)
  shape: bbox 3.2 x 14.09 x 14.09 mm, 12 faces, 2 solids (baked)
FEATURE [Part::Feature] Fusion103077013004017008011016
  Placement = pos=(0,0,0) rot=(0,0,-1;1.25664rad)
  shape: bbox 7.397 x 14.39 x 14.09 mm, 12 faces, 2 solids (baked)
FEATURE [Part::Feature] Fusion103077013004017008011017
  Placement = pos=(0,0,0) rot=(0,0,-1;0.942478rad)
  shape: bbox 10.87 x 13.28 x 14.09 mm, 12 faces, 2 solids (baked)
FEATURE [Part::Feature] Fusion103077013004017008011018
  Placement = pos=(0,0,0) rot=(0,0,-1;0.628319rad)
  shape: bbox 13.28 x 10.87 x 14.09 mm, 12 faces, 2 solids (baked)
FEATURE [Part::Feature] Fusion103077013004017008011019
  Placement = pos=(0,0,0) rot=(0,0,-1;0.314159rad)
  shape: bbox 14.39 x 7.397 x 14.09 mm, 12 faces, 2 solids (baked)
FEATURE [Part::MultiFuse] Fusion103077013004017008011020  label="Big Gear teeth-thin"
  Shapes = -> [Fusion103077013004017008011,Fusion103077013004017008011015,Fusion103077013004017008011014,Fusion103077013004017008011016,Fusion103077013004017008011017,Fusion103077013004017008011001,Fusion103077013004017008011003,Fusion103077013004017008011005,Fusion103077013004017008011011,Fusion103077013004017008011012,Fusion103077013004017008011013,Fusion103077013004017008011008,Fusion103077013004017008011006,+7 more]
FEATURE [Part::FeaturePython] BevelGear003  # WARN: FeaturePython — macro-defined, semantics opaque (R4)
  Placement = pos=(0,0,2.5) rot=(0,0,1;0rad)
  backlash = 0
  beta = 0
  clearance = 0.1
  height = 3.9
  m = 1
  numpoints = 6
  pitch_angle = 45
  pressure_angle = 20
  reset_origin = true
  teeth = 20
FEATURE [Part::Cylinder] Cylinder081002
  Angle = 360
  AttacherType = Attacher::AttachEngine3D
  Height = 22
  Radius = 11
FEATURE [Part::MultiCommon] Common006  label="big-gear-a001"
  Shapes = -> [BevelGear003,Cylinder081002]
FEATURE [Part::Cylinder] Cylinder081003  label="shaft-004"
  Angle = 360
  AttacherType = Attacher::AttachEngine3D
  Height = 10
  Placement = pos=(0,0,-2) rot=(0,0,1;0rad)
  Radius = 1.75
FEATURE [Part::Box] Box406008014  label="Cube349"
  AttacherType = Attacher::AttachEngine3D
  Height = 12
  Length = 10
  Placement = pos=(-5,1.125,-2) rot=(0,0,1;0rad)
  Width = 10
FEATURE [Part::Cut] Cut173011020  label="motor-shaft001"
  Base = -> Cylinder081003
  Tool = -> Box406008014
FEATURE [Part::Cut] Cut173011021  label="big-gear-003"
  Base = -> Common006
  Tool = -> Cut173011020
FEATURE [Part::Chamfer] Chamfer035  label="big-gear001"
  Base = -> Cut173011021
  Edges = 3 edges r=0.5: [Edge124,Edge125,Edge126]
FEATURE [Part::Cylinder] Cylinder081004  label="Cylinder081003"
  Angle = 360
  AttacherType = Attacher::AttachEngine3D
  Height = 6.5
  Placement = pos=(0,0,4) rot=(0,0,1;0rad)
  Radius = 5
FEATURE [Part::Box] Box406008015  label="Cube350"
  AttacherType = Attacher::AttachEngine3D
  Height = 12
  Length = 10
  Placement = pos=(-5,1.125,0) rot=(0,0,1;0rad)
  Width = 10
FEATURE [Part::Cylinder] Cylinder081005  label="shaft-005"
  Angle = 360
  AttacherType = Attacher::AttachEngine3D
  Height = 10
  Placement = pos=(0,0,1) rot=(0,0,1;0rad)
  Radius = 1.75
FEATURE [Part::Cut] Cut173011023
  Base = -> Cylinder081005
  Tool = -> Box406008015
FEATURE [Part::Fuse] Fusion103077013004017008011022
  Base = -> Box406019
  Tool = -> Box406008002
FEATURE [Part::Box] Box406008016  label="Cube351"
  AttacherType = Attacher::AttachEngine3D
  Height = 10
  Length = 17
  Placement = pos=(1.9,-9.6,-1) rot=(0,0,1;0.785398rad)
  Width = 16
FEATURE [Part::Box] Box406008017  label="gearbox006"
  AttacherType = Attacher::AttachEngine3D
  Height = 9
  Length = 12.5
  Placement = pos=(8.125,-0.625,21) rot=(0,0,1;2.35619rad)
  Width = 10.5
FEATURE [Part::Cut] Cut173011025
  Base = -> Fusion103077013004016
  Tool = -> Fusion103077013004013
FEATURE [Part::Cut] Cut173011026
  Base = -> Cut173011025
  Tool = -> Fusion103077013004017008011022
FEATURE [Part::Cut] Cut173011027
  Base = -> Cut173011026
  Tool = -> Common004
FEATURE [Part::Cut] Cut173011028
  Base = -> Cut173011027
  Tool = -> Box406008017
FEATURE [Part::Cut] Cut173011029
  Base = -> Cut173011028
  Tool = -> Box406016
FEATURE [Part::Cylinder] Cylinder081006
  Angle = 360
  AttacherType = Attacher::AttachEngine3D
  Height = 12
  Placement = pos=(0,0,40) rot=(0.281085,0.678598,0.678598;2.59356rad)
  Radius = 1.2
FEATURE [Part::Cylinder] Cylinder081007
  Angle = 360
  AttacherType = Attacher::AttachEngine3D
  Height = 12
  Placement = pos=(8.48528,8.48528,40) rot=(0.281085,0.678598,0.678598;2.59356rad)
  Radius = 2.2
FEATURE [Part::MultiFuse] Fusion103077013004017008011023  label="M2-screw002"
  Placement = pos=(-2,14,0) rot=(0,0,1;3.14159rad)
  Shapes = -> [Cylinder081006,Cylinder081007]
FEATURE [Part::Box] Box406008018  label="Cube352"
  AttacherType = Attacher::AttachEngine3D
  Height = 10.35
  Length = 3.68
  Placement = pos=(13.02,-11.61,32.65) rot=(0,0,1;0.785398rad)
  Width = 10
FEATURE [Part::Chamfer] Chamfer038
  Base = -> Box406008018
  Edges = 1 edges r=9: [Edge9]
FEATURE [Part::Cut] Cut173011030
  Base = -> Chamfer038
  Tool = -> Fusion103077013
FEATURE [Part::Box] Box406008019  label="Cube353"
  AttacherType = Attacher::AttachEngine3D
  Height = 10
  Length = 10
  Placement = pos=(17,-17,35) rot=(0,0,1;0.785398rad)
  Width = 10
FEATURE [Part::Cut] Cut173011031
  Base = -> Cut173011030
  Tool = -> Box406008019
FEATURE [Part::Box] Box406008020  label="Cube354"
  AttacherType = Attacher::AttachEngine3D
  Height = 10
  Length = 10
  Placement = pos=(-13.7,20.31,35) rot=(0,0,1;3.92699rad)
  Width = 10
FEATURE [Part::Box] Box406008021  label="Cube355"
  AttacherType = Attacher::AttachEngine3D
  Height = 10.35
  Length = 3.68
  Placement = pos=(-9.01,15.62,32.65) rot=(0,0,1;3.92699rad)
  Width = 10
FEATURE [Part::Chamfer] Chamfer039
  Base = -> Box406008021
  Edges = 1 edges r=9: [Edge9]
FEATURE [Part::Cut] Cut173011032
  Base = -> Chamfer039
  Tool = -> Box406008020
FEATURE [Part::Cut] Cut173011033
  Base = -> Cut173011032
  Tool = -> Fusion103077013004017008011023
FEATURE [Part::MultiFuse] Fusion103077013004017008011024
  Shapes = -> [Cut173011029,Cut173011031,Cut173011033]
FEATURE [Part::Fillet] Fillet007
  Base = -> Fusion103077013004017008011024
  Edges = 2 edges r=1: [Edge110,Edge115]
FEATURE [Part::Box] Box406008022  label="Cube356"
  AttacherType = Attacher::AttachEngine3D
  Height = 50
  Length = 50
  Placement = pos=(-21,-50,0) rot=(0,0,1;0.785398rad)
  Width = 50
FEATURE [Part::Cylinder] Cylinder081008  label="big-gear-clearance001"
  Angle = 360
  AttacherType = Attacher::AttachEngine3D
  Height = 22
  Radius = 12
FEATURE [Part::Box] Box406008023  label="Cube357"
  AttacherType = Attacher::AttachEngine3D
  Height = 6
  Length = 15
  Placement = pos=(-5,10,2) rot=(0,0,1;0rad)
  Width = 10
FEATURE [Part::Cut] Cut173011034  label="screw-land-002"
  Base = -> Box406008023
  Placement = pos=(0,0,0) rot=(0,0,1;0.785398rad)
  Tool = -> Cylinder081008
FEATURE [Part::Mirroring] Part__Mirroring  label="screw-land-002 (Mirror #1)"
  Base = (0,0,0)
  Normal = (1,0,0)
  Placement = pos=(0,0,0) rot=(0,0,-1;0.785398rad)
  Source = -> Cut173011034
FEATURE [Part::Cylinder] Cylinder081009  label="M3-cap-screw-head002"
  Angle = 360
  AttacherType = Attacher::AttachEngine3D
  Height = 10
  Placement = pos=(0,15,4) rot=(0,0,1;0rad)
  Radius = 3
FEATURE [Part::Cylinder] Cylinder081010  label="M3-cap-screw-head003"
  Angle = 360
  AttacherType = Attacher::AttachEngine3D
  Height = 10
  Placement = pos=(0,15,-6) rot=(0,0,1;0rad)
  Radius = 1.7
FEATURE [Part::MultiFuse] Fusion103077013004017008011025  label="M3-cap-screw001"
  Placement = pos=(0,0,5) rot=(0,0,1;0.785398rad)
  Shapes = -> [Cylinder081010,Cylinder081009]
FEATURE [Part::Mirroring] Part__Mirroring001  label="M3-cap-screw001 (Mirror #2)"
  Base = (0,0,0)
  Normal = (1,0,0)
  Placement = pos=(0,0,0) rot=(0,0,-1;0.785398rad)
  Source = -> Fusion103077013004017008011025
FEATURE [Part::MultiFuse] Fusion103077013004017008011026
  Shapes = -> [Part__Mirroring,Cut173011007]
FEATURE [Part::MultiFuse] Fusion103077013004017008011027
  Shapes = -> [Part__Mirroring001,Fusion103077013004011,Box406008016]
FEATURE [Part::Cut] Cut173011035
  Base = -> Fusion103077013004017008011026
  Tool = -> Fusion103077013004017008011027
FEATURE [Part::Fillet] Fillet008
  Base = -> Cut173011035
  Edges = 2 edges r=3: [Edge4,Edge50]
FEATURE [Part::Feature] Shape
  Placement = pos=(-3.57,12.43,40) rot=(0,0.816497,-0.57735;4.18879rad)
  shape: bbox 5.276 x 5.276 x 4.461 mm, 8 faces (baked)
FEATURE [Drawing::FeatureViewAnnotation] Annotation010
  Font = Sans
  Rotation = 0
  Scale = 7
  ViewResult = <g transform="translate(10,10) rotate(0)">\n<text id="Annotation010"\n font-family="Sans"\n font-size="7"\n fill="#000000">\n<tspan x="0" dy="1em"></tspan>\n</text>\n</g>
  Visible = true
  X = 10
  Y = 10
FEATURE [Drawing::FeatureViewAnnotation] Annotation011
  Font = Sans
  Rotation = 0
  Scale = 5
  Text = Rotated Slots and amended screw clamp position and added nut recess. Cut in half. Made slots in the screw lands so the gear can freely rotate.
  ViewResult = <g transform="translate(10,60) rotate(0)">\n<text id="Annotation011"\n font-family="Sans"\n font-size="5"\n fill="#000000">\n<tspan x="0" dy="1em">Rotated Slots and amended screw clamp position and added nut recess. Cut in half. Made slots in the screw lands so the gear can freely rotate.</tspan>\n<tspan x="0" dy="1em"></tspan>\n</text>\n</g>
  Visible = true
  X = 10
  Y = 60
FEATURE [Part::Fillet] Fillet009
  Base = -> Fillet008
  Edges = 2 edges r=3: [Edge3,Edge42]
FEATURE [Part::MultiFuse] Fusion103077013004017008011028
  Shapes = -> [Fillet009,Fillet007]
FEATURE [Part::Cut] Cut173011036
  Base = -> Fusion103077013004017008011028
  Tool = -> Box406008022
FEATURE [Part::Cut] Cut173011037
  Base = -> Cut173011036
  Tool = -> Shape
FEATURE [Part::Cut] Cut173011038
  Base = -> Cut173011037
  Tool = -> Cylinder059
FEATURE [Part::Fuse] Fusion103077013004017008011029
  Base = -> Chamfer035
  Tool = -> Cylinder081004
FEATURE [Part::Cut] Cut173011039  label="Big Gear 0.4 a"
  Base = -> Fusion103077013004017008011029
  Tool = -> Cut173011023
FEATURE [Drawing::FeatureViewAnnotation] Annotation012
  Font = Sans
  Rotation = 0
  Scale = 7
  ViewResult = <g transform="translate(10,10) rotate(0)">\n<text id="Annotation012"\n font-family="Sans"\n font-size="7"\n fill="#000000">\n<tspan x="0" dy="1em"></tspan>\n</text>\n</g>
  Visible = true
  X = 10
  Y = 10
FEATURE [Drawing::FeatureViewAnnotation] Annotation013
  Font = Sans
  Rotation = 0
  Scale = 7
  ViewResult = <g transform="translate(10,10) rotate(0)">\n<text id="Annotation013"\n font-family="Sans"\n font-size="7"\n fill="#000000">\n<tspan x="0" dy="1em"></tspan>\n</text>\n</g>
  Visible = true
  X = 10
  Y = 10
FEATURE [Drawing::FeatureViewAnnotation] Annotation014
  Font = Sans
  Rotation = 0
  Scale = 7
  ViewResult = <g transform="translate(10,10) rotate(0)">\n<text id="Annotation014"\n font-family="Sans"\n font-size="7"\n fill="#000000">\n<tspan x="0" dy="1em"></tspan>\n</text>\n</g>
  Visible = true
  X = 10
  Y = 10
FEATURE [Drawing::FeaturePage] Page
  EditableTexts = AUTHOR NAME | CREATION DATE | SUPERVISOR NAME | CHECK DATE | SCALE | WEIGHT | NUMBER | SHEET | TITLE | SUBTITLE
  Group = -> [Annotation,Annotation001,Annotation002,Annotation004,Annotation007,Annotation008,Annotation010,Annotation012,Annotation013,Annotation014]
  Template = <path>
FEATURE [Drawing::FeatureViewAnnotation] Annotation015
  Font = Sans
  Rotation = 0
  Scale = 5
  Text = 0.4 Switched back to thicker teeth on gears
  ViewResult = <g transform="translate(10,70) rotate(0)">\n<text id="Annotation015"\n font-family="Sans"\n font-size="5"\n fill="#000000">\n<tspan x="0" dy="1em">0.4 Switched back to thicker teeth on gears</tspan>\n<tspan x="0" dy="1em"></tspan>\n</text>\n</g>
  Visible = true
  X = 10
  Y = 70
FEATURE [Part::Chamfer] Chamfer040  label="big-gear 0.4 b"
  Base = -> Cut173011039
  Edges = 3 edges r=0.5: [Edge125,Edge126,Edge127]
FEATURE [Part::Chamfer] Chamfer041  label="big gear 0.4 a"
  Base = -> Chamfer040
  Edges = 3 edges r=1: [Edge142,Edge144,Edge145]
FEATURE [Part::Cone] Cone002
  Angle = 360
  AttacherType = Attacher::AttachEngine3D
  Height = 5
  Placement = pos=(0,0,3.6) rot=(0,0,1;0rad)
  Radius1 = 14
  Radius2 = 4
FEATURE [Part::Cylinder] Cylinder081011  label="Cylinder081008"
  Angle = 360
  AttacherType = Attacher::AttachEngine3D
  Height = 10
  Placement = pos=(0,0,4) rot=(0,0,1;0rad)
  Radius = 14
FEATURE [Part::Cut] Cut173011040
  Base = -> Cylinder081011
  Tool = -> Cone002
FEATURE [Part::Cylinder] Cylinder081012  label="Cylinder081009"
  Angle = 360
  AttacherType = Attacher::AttachEngine3D
  Height = 15
  Radius = 8
FEATURE [Part::Cut] Cut173011041
  Base = -> Cut173011040
  Tool = -> Cylinder081012
FEATURE [Part::Cut] Cut173011042  label="big gear 0.4"
  Base = -> Chamfer041
  Tool = -> Cut173011041
FEATURE [App::DocumentObjectGroup] Group004
FEATURE [App::DocumentObjectGroup] Group002  label="Old 0.1"
  Group = -> [Sphere027,Sphere028,Sphere029,Sphere031,Sphere032,Sphere033,Sphere034,Cylinder012,Cylinder016,Cylinder015,Cylinder014,Cylinder013,Cylinder017,Cylinder019,Box067,Box073,Box071,Box068,Box070,Box072,Box074,Group004]
FEATURE [App::DocumentObjectGroup] Group005  label="Old 0.5"
  Group = -> [Cut173011042,Fusion103077013004017008011020,Fusion103077013004017008010,Chamfer032,Shape002,Cut173011005]
FEATURE [Part::Cylinder] Cylinder081013  label="Cylinder081010"
  Angle = 360
  AttacherType = Attacher::AttachEngine3D
  Height = 10
  Placement = pos=(0,0,12) rot=(0,0,1;0rad)
  Radius = 1.5
FEATURE [Part::Cylinder] Cylinder081014  label="Cylinder081011"
  Angle = 360
  AttacherType = Attacher::AttachEngine3D
  Height = 4
  Placement = pos=(0,0,16) rot=(0,0,1;0rad)
  Radius = 4
FEATURE [Part::Cylinder] Cylinder081015  label="Cylinder081012"
  Angle = 360
  AttacherType = Attacher::AttachEngine3D
  Height = 2
  Placement = pos=(0,0,14) rot=(0,0,1;0rad)
  Radius = 5.355
FEATURE [Part::Cone] Cone003
  Angle = 360
  AttacherType = Attacher::AttachEngine3D
  Height = 1.71
  Placement = pos=(0,0,12.3) rot=(0,0,1;0rad)
  Radius1 = 3.6
  Radius2 = 5.31
FEATURE [Part::Cylinder] Cylinder081016  label="Cylinder081013"
  Angle = 360
  AttacherType = Attacher::AttachEngine3D
  Height = 10
  Placement = pos=(0,12,8) rot=(1,0,0;1.5708rad)
  Radius = 1.5
FEATURE [Part::Cylinder] Cylinder081017  label="Cylinder081014"
  Angle = 360
  AttacherType = Attacher::AttachEngine3D
  Height = 4
  Placement = pos=(0,11,8) rot=(1,0,0;1.5708rad)
  Radius = 4
FEATURE [Part::Cylinder] Cylinder081018  label="Cylinder081015"
  Angle = 360
  AttacherType = Attacher::AttachEngine3D
  Height = 2
  Placement = pos=(0,7,8) rot=(1,0,0;1.5708rad)
  Radius = 5.355
FEATURE [Part::Cone] Cone004
  Angle = 360
  AttacherType = Attacher::AttachEngine3D
  Height = 1.71
  Placement = pos=(0,5,8) rot=(1,0,0;1.5708rad)
  Radius1 = 5.31
  Radius2 = 3.6
FEATURE [Drawing::FeatureViewAnnotation] Annotation016
  Font = Sans
  Rotation = 0
  Scale = 5
  Text = 0.5 Modelled RS Gears 521-6036 and moved the M3 Screw drive down by 2.5mm
  ViewResult = <g transform="translate(10,80) rotate(0)">\n<text id="Annotation016"\n font-family="Sans"\n font-size="5"\n fill="#000000">\n<tspan x="0" dy="1em">0.5 Modelled RS Gears 521-6036 and moved the M3 Screw drive down by 2.5mm</tspan>\n<tspan x="0" dy="1em"></tspan>\n</text>\n</g>
  Visible = true
  X = 10
  Y = 80
FEATURE [Drawing::FeaturePage] Page001
  EditableTexts = AUTHOR NAME | CREATION DATE | SUPERVISOR NAME | CHECK DATE | SCALE | WEIGHT | NUMBER | SHEET | TITLE | SUBTITLE
  Group = -> [Annotation003,Annotation005,Annotation006,Annotation009,Annotation011,Annotation015,Annotation016]
  Template = <path>
FEATURE [Part::Cylinder] Cylinder081019  label="nylock-cavity"
  Angle = 360
  AttacherType = Attacher::AttachEngine3D
  Height = 20
  Placement = pos=(23.87,23.87,8) rot=(0.862856,-0.357407,-0.357407;1.71777rad)
  Radius = 4.25
FEATURE [Part::Cut] Cut173011043  label="motor-mount"
  Base = -> Cut173011038
  Tool = -> Cylinder081019
FEATURE [Part::MultiFuse] Fusion103077013004017008011030  label="commercial-gear"
  Placement = pos=(0,0,0) rot=(0,0,-1;0.785398rad)
  Shapes = -> [Cone004,Cylinder081016,Cylinder081017,Cylinder081018]
FEATURE [Part::Chamfer] Chamfer042  label="finger"
  Base = -> Chamfer034
  Edges = 4 edges r=0.5: [Edge15,Edge16,Edge17,Edge18]
FEATURE [Part::Cylinder] Cylinder081020  label="3mm-hole"
  Angle = 360
  AttacherType = Attacher::AttachEngine3D
  Height = 10
  Placement = pos=(0,0,-13) rot=(1,0,0;0rad)
  Radius = 1.5
FEATURE [Part::Cylinder] Cylinder081021  label="hub"
  Angle = 360
  AttacherType = Attacher::AttachEngine3D
  Height = 4
  Placement = pos=(0,0,-11) rot=(1,0,0;0rad)
  Radius = 4
FEATURE [Part::Cylinder] Cylinder081022  label="gear-base"
  Angle = 360
  AttacherType = Attacher::AttachEngine3D
  Height = 0.5
  Placement = pos=(0,0,-7.5) rot=(1,0,0;0rad)
  Radius = 5.355
FEATURE [Part::Cone] Cone005
  Angle = 360
  AttacherType = Attacher::AttachEngine3D
  Height = 1.71
  Placement = pos=(0,0,-5) rot=(1,0,0;0rad)
  Radius1 = 5.31
  Radius2 = 3.6
FEATURE [Part::FeaturePython] BevelGear  # WARN: FeaturePython — macro-defined, semantics opaque (R4)
  Placement = pos=(0,0,-7) rot=(0,0,1;0rad)
  backlash = 0
  beta = 0
  clearance = 0.1
  height = 3.71
  m = 0.46
  numpoints = 6
  pitch_angle = 42
  pressure_angle = 20
  reset_origin = true
  teeth = 21
FEATURE [Part::Cylinder] Cylinder081023  label="Cylinder081019"
  Angle = 360
  AttacherType = Attacher::AttachEngine3D
  Height = 20
  Placement = pos=(0,0,-15) rot=(1,0,0;0rad)
  Radius = 5.355
FEATURE [Part::MultiCommon] Common007  label="chopped-gear"
  Shapes = -> [BevelGear,Cylinder081023]
FEATURE [Part::MultiFuse] Fusion103077013004017008011031  label="blank-gear-1"
  Shapes = -> [Cylinder081022,Common007]
FEATURE [Part::Cylinder] Cylinder081024  label="cap-head"
  Angle = 360
  AttacherType = Attacher::AttachEngine3D
  Height = 4
  Placement = pos=(0,0,-4.3) rot=(1,0,0;0rad)
  Radius = 2.7
FEATURE [Part::MultiFuse] Fusion103077013004017008011032  label="cavity-1"
  Shapes = -> [Cylinder081024,Cylinder081020]
FEATURE [Part::MultiFuse] Fusion103077013004017008011033  label="blank-gear-2"
  Shapes = -> [Fusion103077013004017008011031,Cylinder081021]
FEATURE [Part::Cut] Cut173011044  label="gear-2"
  Base = -> Fusion103077013004017008011033
  Tool = -> Fusion103077013004017008011032
FEATURE [Part::Cylinder] Cylinder081025  label="Cylinder081020"
  Angle = 360
  AttacherType = Attacher::AttachEngine3D
  Height = 10
  Placement = pos=(3.5,0,-9) rot=(0,1,0;1.5708rad)
  Radius = 1.25
FEATURE [Part::Cylinder] Cylinder081026  label="Cylinder081021"
  Angle = 360
  AttacherType = Attacher::AttachEngine3D
  Height = 10
  Placement = pos=(0,0,-9) rot=(0,1,0;1.5708rad)
  Radius = 1
FEATURE [Part::MultiFuse] Fusion103077013004017008011034  label="cavity-2"
  Shapes = -> [Cylinder081025,Cylinder081026]
FEATURE [Part::Cut] Cut173011045  label="gear-3"
  Base = -> Cut173011044
  Tool = -> Fusion103077013004017008011034
FEATURE [Part::Chamfer] Chamfer043  label="gear-4"
  Base = -> Cut173011045
  Edges = 1 edges r=0.2: [Edge11]
FEATURE [Part::Chamfer] Chamfer044  label="gear"
  Base = -> Chamfer043
  Edges = 2 edges r=0.1: [Edge13,Edge15]
note: 2 file-system paths scrubbed to <path> (originals preserved in the JSON sidecar)
